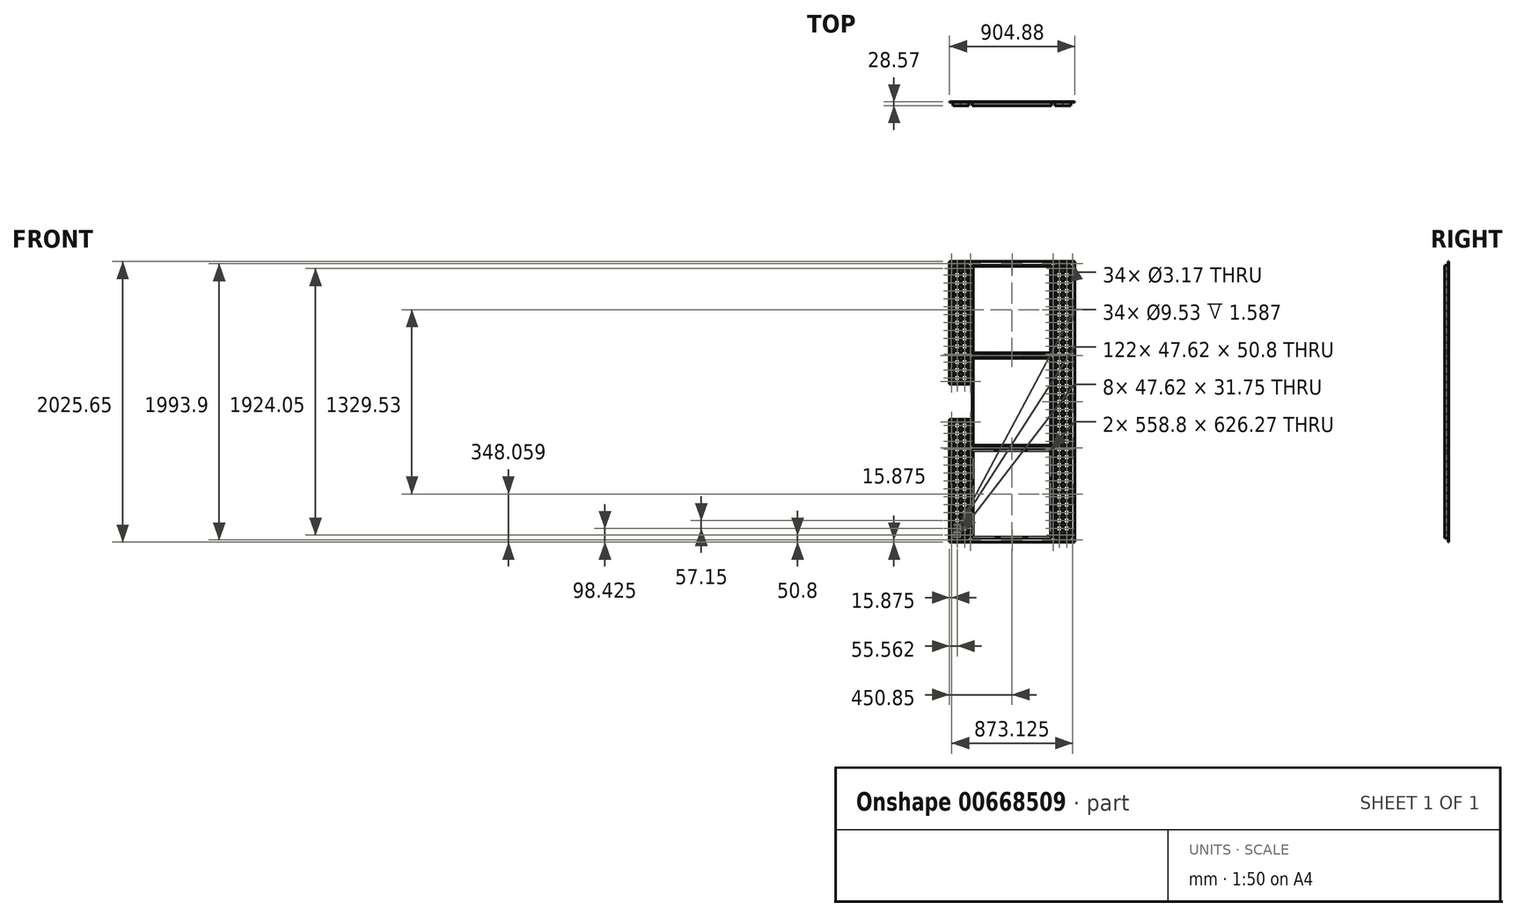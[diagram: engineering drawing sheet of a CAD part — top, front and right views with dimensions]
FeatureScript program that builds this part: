
annotation { "Feature Type Name" : "Feature", "Feature Type Description" : "" }
export const myFeature = defineFeature(function(context is Context, id is Id, definition is map)
    precondition{}
    {
        {
            var Q0;
            Q0=qCreatedBy(makeId("Front.planeOp"),FACE);
            var sketch = newSketch(context, id + "F0", { "sketchPlane" : qUnion([Q0])});
            skLineSegment(sketch, "E0.top", {"start": v(-285.75, 485.77) * mm, "end": v(285.75, 485.77) * mm});
            skPoint(sketch, "E0.middle", {"position": v(0, 0) * mm});
            skLineSegment(sketch, "E1.0", {"start": v(-285.75, -1482.73) * mm, "end": v(285.75, -1482.73) * mm});
            skLineSegment(sketch, "E2", {"start": v(311.15, 485.77) * mm, "end": v(311.15, -1482.73) * mm});
            skLineSegment(sketch, "E3", {"start": v(311.15, -1482.73) * mm, "end": v(425.45, -1482.73) * mm});
            skLineSegment(sketch, "E4", {"start": v(425.45, -1482.73) * mm, "end": v(425.45, 485.77) * mm});
            skLineSegment(sketch, "E5", {"start": v(425.45, 485.77) * mm, "end": v(311.15, 485.77) * mm});
            skLineSegment(sketch, "E6", {"start": v(-311.15, -1482.73) * mm, "end": v(-311.15, -638.18) * mm});
            skLineSegment(sketch, "E7", {"start": v(-311.15, -638.18) * mm, "end": v(-425.45, -638.18) * mm});
            skLineSegment(sketch, "E8", {"start": v(-425.45, -638.18) * mm, "end": v(-425.45, -1482.73) * mm});
            skLineSegment(sketch, "E9", {"start": v(-425.45, -1482.73) * mm, "end": v(-311.15, -1482.73) * mm});
            skLineSegment(sketch, "E10", {"start": v(-311.15, 485.77) * mm, "end": v(-425.45, 485.77) * mm});
            skLineSegment(sketch, "E11", {"start": v(-425.45, 485.77) * mm, "end": v(-425.45, -358.78) * mm});
            skLineSegment(sketch, "E12", {"start": v(-311.15, 485.77) * mm, "end": v(-311.15, -358.78) * mm});
            skLineSegment(sketch, "E13", {"start": v(-311.15, -358.78) * mm, "end": v(-425.45, -358.78) * mm});
            skLineSegment(sketch, "E14.0", {"start": v(450.85, -1508.13) * mm, "end": v(450.85, 511.17) * mm});
            skLineSegment(sketch, "E15", {"start": v(450.85, 511.17) * mm, "end": v(-450.85, 511.17) * mm});
            skLineSegment(sketch, "E16", {"start": v(-450.85, 511.17) * mm, "end": v(-450.85, -371.48) * mm});
            skLineSegment(sketch, "E17", {"start": v(-450.85, -371.48) * mm, "end": v(-298.45, -371.48) * mm});
            skLineSegment(sketch, "E18", {"start": v(-298.45, -371.48) * mm, "end": v(-298.45, -625.48) * mm});
            skLineSegment(sketch, "E19", {"start": v(-298.45, -625.48) * mm, "end": v(-450.85, -625.48) * mm});
            skLineSegment(sketch, "E20", {"start": v(-450.85, -625.48) * mm, "end": v(-450.85, -1508.13) * mm});
            skLineSegment(sketch, "E21", {"start": v(-450.85, -1508.13) * mm, "end": v(450.85, -1508.13) * mm});
            skLineSegment(sketch, "E22", {"start": v(-285.75, 485.77) * mm, "end": v(-285.75, -1482.73) * mm});
            skLineSegment(sketch, "E23", {"start": v(285.75, -1482.73) * mm, "end": v(285.75, 485.77) * mm});
            skLineSegment(sketch, "E24", {"start": v(-285.75, -818.36) * mm, "end": v(285.75, -818.36) * mm});
            skLineSegment(sketch, "E25", {"start": v(-285.75, -153.2) * mm, "end": v(285.75, -153.2) * mm});
            skLineSegment(sketch, "E26", {"start": v(-285.75, -178.6) * mm, "end": v(285.75, -178.6) * mm});
            skLineSegment(sketch, "E27", {"start": v(-285.75, -843.76) * mm, "end": v(285.75, -843.76) * mm});
            skLineSegment(sketch, "E28.2", {"start": v(-450.85, -1511.3) * mm, "end": v(454.02, -1511.3) * mm});
            skLineSegment(sketch, "E28.3", {"start": v(454.02, -1511.3) * mm, "end": v(454.02, 514.35) * mm});
            skLineSegment(sketch, "E28.4", {"start": v(454.02, 514.35) * mm, "end": v(-450.85, 514.35) * mm});
            skLineSegment(sketch, "E29", {"start": v(-450.85, 511.17) * mm, "end": v(-450.85, 514.35) * mm});
            skLineSegment(sketch, "E30", {"start": v(-450.85, -1511.3) * mm, "end": v(-450.85, -1508.13) * mm});
            skSolve(sketch);
        }
        {
            var Q0;
            Q0 = qSketchRegion(id + "F0", true);
            var Q1;
            {var subQ0=sQuery(id+"F0.wireOp",EDGE,"E24");Q1=makeQuery(id+"F0.imprint","IMPRINT",FACE,{"disambiguationData":[TD([[makeQuery(id+"F0.imprint","IMPRINT",EDGE,{"derivedFrom":subQ0}),-1.0]])]});}
            var Q2;
            {var subQ0=sQuery(id+"F0.wireOp",EDGE,"E25");Q2=makeQuery(id+"F0.imprint","IMPRINT",FACE,{"disambiguationData":[TD([[makeQuery(id+"F0.imprint","IMPRINT",EDGE,{"derivedFrom":subQ0}),-1.0]])]});}
            extrude(context, id + "F1", {"entities" : qUnion([Q0, Q1, Q2]), "depth" : 3.17 * mm, "offsetDistance" : 25.4 * mm});
        }
        {
            var Q0;
            Q0=qCreatedBy(makeId("Front.planeOp"),FACE);
            var sketch = newSketch(context, id + "F2", { "sketchPlane" : qUnion([Q0])});
            skLineSegment(sketch, "E31.0", {"start": v(-425.45, 485.77) * mm, "end": v(-425.45, -358.78) * mm});
            skLineSegment(sketch, "E32.0", {"start": v(-311.15, 485.77) * mm, "end": v(-425.45, 485.77) * mm});
            skLineSegment(sketch, "E33.0", {"start": v(-311.15, 485.77) * mm, "end": v(-311.15, -358.78) * mm});
            skLineSegment(sketch, "E34.0", {"start": v(-311.15, -358.78) * mm, "end": v(-425.45, -358.78) * mm});
            skLineSegment(sketch, "E35.0", {"start": v(-285.75, 485.77) * mm, "end": v(-285.75, 485.77) * mm});
            skPoint(sketch, "E36.0", {"position": v(368.3, 485.77) * mm});
            skLineSegment(sketch, "E37.0", {"start": v(425.45, 485.77) * mm, "end": v(311.15, 485.77) * mm});
            skLineSegment(sketch, "E38.0", {"start": v(-425.45, -1482.73) * mm, "end": v(-311.15, -1482.73) * mm});
            skLineSegment(sketch, "E39.0", {"start": v(-311.15, -1482.73) * mm, "end": v(-311.15, -638.18) * mm});
            skLineSegment(sketch, "E40.0", {"start": v(-425.45, -638.18) * mm, "end": v(-425.45, -1482.73) * mm});
            skLineSegment(sketch, "E41.0", {"start": v(-311.15, -638.18) * mm, "end": v(-425.45, -638.18) * mm});
            skLineSegment(sketch, "E42.0", {"start": v(-419.1, 479.42) * mm, "end": v(-419.1, -352.42) * mm});
            skLineSegment(sketch, "E42.1", {"start": v(-317.5, 479.42) * mm, "end": v(-419.1, 479.42) * mm});
            skLineSegment(sketch, "E42.2", {"start": v(-317.5, 479.42) * mm, "end": v(-317.5, -352.42) * mm});
            skLineSegment(sketch, "E42.3", {"start": v(-317.5, -352.42) * mm, "end": v(-419.1, -352.42) * mm});
            skLineSegment(sketch, "E43.0", {"start": v(-317.5, -644.52) * mm, "end": v(-419.1, -644.52) * mm});
            skLineSegment(sketch, "E43.1", {"start": v(-317.5, -1476.38) * mm, "end": v(-317.5, -644.52) * mm});
            skLineSegment(sketch, "E43.2", {"start": v(-419.1, -1476.38) * mm, "end": v(-317.5, -1476.38) * mm});
            skLineSegment(sketch, "E43.3", {"start": v(-419.1, -644.52) * mm, "end": v(-419.1, -1476.38) * mm});
            skLineSegment(sketch, "E44.0", {"start": v(-285.75, 485.77) * mm, "end": v(-285.75, -153.2) * mm});
            skLineSegment(sketch, "E45.0", {"start": v(-285.75, 485.77) * mm, "end": v(285.75, 485.77) * mm});
            skLineSegment(sketch, "E46.0", {"start": v(285.75, -153.2) * mm, "end": v(285.75, 485.77) * mm});
            skLineSegment(sketch, "E47.0", {"start": v(-285.75, -153.2) * mm, "end": v(285.75, -153.2) * mm});
            skLineSegment(sketch, "E48.0", {"start": v(-285.75, -178.6) * mm, "end": v(285.75, -178.6) * mm});
            skLineSegment(sketch, "E49.0", {"start": v(-285.75, -178.6) * mm, "end": v(-285.75, -818.36) * mm});
            skLineSegment(sketch, "E50.0", {"start": v(285.75, -818.36) * mm, "end": v(285.75, -178.6) * mm});
            skLineSegment(sketch, "E51.0", {"start": v(-285.75, -818.36) * mm, "end": v(285.75, -818.36) * mm});
            skLineSegment(sketch, "E52.0", {"start": v(-285.75, -843.76) * mm, "end": v(285.75, -843.76) * mm});
            skLineSegment(sketch, "E53.0", {"start": v(-285.75, -843.76) * mm, "end": v(-285.75, -1482.73) * mm});
            skLineSegment(sketch, "E54.0", {"start": v(285.75, -1482.73) * mm, "end": v(285.75, -843.76) * mm});
            skLineSegment(sketch, "E55.0", {"start": v(-285.75, -1482.73) * mm, "end": v(285.75, -1482.73) * mm});
            skLineSegment(sketch, "E56.0", {"start": v(-279.4, 479.43) * mm, "end": v(279.4, 479.43) * mm});
            skLineSegment(sketch, "E56.1", {"start": v(-279.4, 479.43) * mm, "end": v(-279.4, -146.84) * mm});
            skLineSegment(sketch, "E56.2", {"start": v(-279.4, -146.84) * mm, "end": v(279.4, -146.84) * mm});
            skLineSegment(sketch, "E56.3", {"start": v(279.4, -146.84) * mm, "end": v(279.4, 479.43) * mm});
            skLineSegment(sketch, "E57.0", {"start": v(-279.4, -184.94) * mm, "end": v(279.4, -184.94) * mm});
            skLineSegment(sketch, "E57.1", {"start": v(-279.4, -184.94) * mm, "end": v(-279.4, -812) * mm});
            skLineSegment(sketch, "E57.2", {"start": v(-279.4, -812) * mm, "end": v(279.4, -812) * mm});
            skLineSegment(sketch, "E57.3", {"start": v(279.4, -812) * mm, "end": v(279.4, -184.94) * mm});
            skLineSegment(sketch, "E58.0", {"start": v(-279.4, -850.1) * mm, "end": v(279.4, -850.1) * mm});
            skLineSegment(sketch, "E58.1", {"start": v(-279.4, -850.1) * mm, "end": v(-279.4, -1476.38) * mm});
            skLineSegment(sketch, "E58.2", {"start": v(-279.4, -1476.38) * mm, "end": v(279.4, -1476.38) * mm});
            skLineSegment(sketch, "E58.3", {"start": v(279.4, -1476.38) * mm, "end": v(279.4, -850.1) * mm});
            skLineSegment(sketch, "E59.0", {"start": v(425.45, -1482.73) * mm, "end": v(425.45, 485.77) * mm});
            skLineSegment(sketch, "E60.0", {"start": v(311.15, -1482.73) * mm, "end": v(425.45, -1482.73) * mm});
            skLineSegment(sketch, "E61.0", {"start": v(311.15, 485.77) * mm, "end": v(311.15, -1482.73) * mm});
            skLineSegment(sketch, "E62.0", {"start": v(419.1, 479.43) * mm, "end": v(317.5, 479.43) * mm});
            skLineSegment(sketch, "E62.1", {"start": v(419.1, -1476.38) * mm, "end": v(419.1, 479.43) * mm});
            skLineSegment(sketch, "E62.2", {"start": v(317.5, -1476.38) * mm, "end": v(419.1, -1476.38) * mm});
            skLineSegment(sketch, "E62.3", {"start": v(317.5, 479.43) * mm, "end": v(317.5, -1476.38) * mm});
            skSolve(sketch);
        }
        {
            var Q0;
            Q0=makeQuery(id+"F2.imprint","IMPRINT",FACE,{"disambiguationData":[TD([[makeQuery(id+"F2.imprint","IMPRINT",EDGE,{"derivedFrom":sQuery(id+"F2.wireOp",EDGE,"E37.0")}),1.0]])]});
            var Q1;
            Q1=makeQuery(id+"F2.imprint","IMPRINT",FACE,{"disambiguationData":[TD([[makeQuery(id+"F2.imprint","IMPRINT",EDGE,{"derivedFrom":sQuery(id+"F2.wireOp",EDGE,"E52.0")}),-1.0]])]});
            var Q2;
            Q2=makeQuery(id+"F2.imprint","IMPRINT",FACE,{"disambiguationData":[TD([[makeQuery(id+"F2.imprint","IMPRINT",EDGE,{"derivedFrom":sQuery(id+"F2.wireOp",EDGE,"E48.0")}),-1.0]])]});
            var Q3;
            Q3=makeQuery(id+"F2.imprint","IMPRINT",FACE,{"disambiguationData":[TD([[makeQuery(id+"F2.imprint","IMPRINT",EDGE,{"derivedFrom":sQuery(id+"F2.wireOp",EDGE,"E38.0")}),1.0]])]});
            var Q4;
            Q4=makeQuery(id+"F2.imprint","IMPRINT",FACE,{"disambiguationData":[TD([[makeQuery(id+"F2.imprint","IMPRINT",EDGE,{"derivedFrom":sQuery(id+"F2.wireOp",EDGE,"E31.0")}),1.0]])]});
            var Q5;
            Q5=makeQuery(id+"F2.imprint","IMPRINT",FACE,{"disambiguationData":[TD([[makeQuery(id+"F2.imprint","IMPRINT",EDGE,{"derivedFrom":sQuery(id+"F2.wireOp",EDGE,"E44.0")}),1.0]])]});
            extrude(context, id + "F3", {"entities" : qUnion([Q0, Q1, Q2, Q3, Q4, Q5]), "operationType" : NewBodyOperationType.ADD, "depth" : 28.57 * mm, "offsetDistance" : 25.4 * mm});
        }
        {
            var Q0;
            Q0=qCreatedBy(makeId("Front.planeOp"),FACE);
            var sketch = newSketch(context, id + "F4", { "sketchPlane" : qUnion([Q0])});
            skLineSegment(sketch, "E63.0", {"start": v(-279.4, -184.94) * mm, "end": v(-279.4, -812) * mm});
            skLineSegment(sketch, "E64.0", {"start": v(279.4, -812) * mm, "end": v(279.4, -184.94) * mm});
            skLineSegment(sketch, "E65.0", {"start": v(-279.4, -812) * mm, "end": v(279.4, -812) * mm});
            skLineSegment(sketch, "E66.0", {"start": v(-317.5, 479.42) * mm, "end": v(-419.1, 479.42) * mm});
            skLineSegment(sketch, "E67.0", {"start": v(-419.1, 479.42) * mm, "end": v(-419.1, -352.42) * mm});
            skLineSegment(sketch, "E68.0", {"start": v(-317.5, 479.42) * mm, "end": v(-317.5, -352.42) * mm});
            skLineSegment(sketch, "E69.0", {"start": v(-317.5, -352.42) * mm, "end": v(-419.1, -352.42) * mm});
            skLineSegment(sketch, "E70.0", {"start": v(-419.1, -644.52) * mm, "end": v(-419.1, -1476.38) * mm});
            skLineSegment(sketch, "E71.0", {"start": v(-317.5, -644.52) * mm, "end": v(-419.1, -644.52) * mm});
            skLineSegment(sketch, "E72.0", {"start": v(-317.5, -1476.38) * mm, "end": v(-317.5, -644.52) * mm});
            skLineSegment(sketch, "E73.0", {"start": v(-419.1, -1476.38) * mm, "end": v(-317.5, -1476.38) * mm});
            skLineSegment(sketch, "E74.0", {"start": v(317.5, -1476.38) * mm, "end": v(419.1, -1476.38) * mm});
            skLineSegment(sketch, "E75.0", {"start": v(317.5, 479.43) * mm, "end": v(317.5, -1476.38) * mm});
            skLineSegment(sketch, "E76.0", {"start": v(419.1, -1476.38) * mm, "end": v(419.1, 479.43) * mm});
            skLineSegment(sketch, "E77.0", {"start": v(419.1, 479.43) * mm, "end": v(317.5, 479.43) * mm});
            skLineSegment(sketch, "E78", {"start": v(-419.1, -1444.63) * mm, "end": v(-317.5, -1444.63) * mm});
            skLineSegment(sketch, "E79.0", {"start": v(-419.1, -1438.27) * mm, "end": v(-317.5, -1438.27) * mm});
            skLineSegment(sketch, "E80.0", {"start": v(-419.1, -1387.47) * mm, "end": v(-317.5, -1387.47) * mm});
            skLineSegment(sketch, "E81.0", {"start": v(-419.1, -1381.12) * mm, "end": v(-317.5, -1381.12) * mm});
            skLineSegment(sketch, "E82.0", {"start": v(-419.1, -1330.32) * mm, "end": v(-371.47, -1330.32) * mm});
            skLineSegment(sketch, "E83.0", {"start": v(-419.1, -1323.97) * mm, "end": v(-317.5, -1323.97) * mm});
            skLineSegment(sketch, "E84.0", {"start": v(-419.1, -1273.17) * mm, "end": v(-317.5, -1273.17) * mm});
            skLineSegment(sketch, "E85.0", {"start": v(-419.1, -1266.82) * mm, "end": v(-317.5, -1266.82) * mm});
            skLineSegment(sketch, "E86.0", {"start": v(-419.1, -1216.02) * mm, "end": v(-317.5, -1216.02) * mm});
            skLineSegment(sketch, "E87.0", {"start": v(-419.1, -1209.67) * mm, "end": v(-317.5, -1209.67) * mm});
            skLineSegment(sketch, "E88.0", {"start": v(-419.1, -1158.87) * mm, "end": v(-317.5, -1158.87) * mm});
            skLineSegment(sketch, "E89.0", {"start": v(-419.1, -1152.52) * mm, "end": v(-317.5, -1152.52) * mm});
            skLineSegment(sketch, "E90.0", {"start": v(-419.1, -1101.72) * mm, "end": v(-317.5, -1101.72) * mm});
            skLineSegment(sketch, "E91.0", {"start": v(-419.1, -1095.37) * mm, "end": v(-317.5, -1095.37) * mm});
            skLineSegment(sketch, "E92.0", {"start": v(-419.1, -1044.57) * mm, "end": v(-317.5, -1044.57) * mm});
            skLineSegment(sketch, "E93.0", {"start": v(-419.1, -1038.22) * mm, "end": v(-317.5, -1038.22) * mm});
            skLineSegment(sketch, "E94.0", {"start": v(-419.1, -987.42) * mm, "end": v(-317.5, -987.42) * mm});
            skLineSegment(sketch, "E95.0", {"start": v(-419.1, -981.07) * mm, "end": v(-317.5, -981.07) * mm});
            skLineSegment(sketch, "E96.0", {"start": v(-419.1, -930.27) * mm, "end": v(-317.5, -930.27) * mm});
            skLineSegment(sketch, "E97.0", {"start": v(-419.1, -923.92) * mm, "end": v(-317.5, -923.92) * mm});
            skLineSegment(sketch, "E98.0", {"start": v(-419.1, -873.12) * mm, "end": v(-317.5, -873.12) * mm});
            skLineSegment(sketch, "E99.0", {"start": v(-419.1, -866.77) * mm, "end": v(-317.5, -866.77) * mm});
            skLineSegment(sketch, "E100.0", {"start": v(-419.1, -815.97) * mm, "end": v(-317.5, -815.97) * mm});
            skLineSegment(sketch, "E101.0", {"start": v(-419.1, -809.62) * mm, "end": v(-279.4, -809.62) * mm});
            skLineSegment(sketch, "E102.0", {"start": v(-419.1, -758.82) * mm, "end": v(-279.4, -758.82) * mm});
            skLineSegment(sketch, "E103.0", {"start": v(-419.1, -752.47) * mm, "end": v(-279.4, -752.47) * mm});
            skLineSegment(sketch, "E104.0", {"start": v(-419.1, -701.67) * mm, "end": v(-317.5, -701.67) * mm});
            skLineSegment(sketch, "E105.0", {"start": v(-419.1, -695.32) * mm, "end": v(-317.5, -695.32) * mm});
            skLineSegment(sketch, "E106.0", {"start": v(-419.1, -644.52) * mm, "end": v(-279.4, -644.52) * mm});
            skLineSegment(sketch, "E107.0", {"start": v(-419.1, -638.17) * mm, "end": v(-279.4, -638.17) * mm});
            skLineSegment(sketch, "E108.0", {"start": v(-419.1, -587.37) * mm, "end": v(-279.4, -587.37) * mm});
            skLineSegment(sketch, "E109.0", {"start": v(-419.1, -581.02) * mm, "end": v(-279.4, -581.02) * mm});
            skLineSegment(sketch, "E110.0", {"start": v(-419.1, -530.22) * mm, "end": v(-279.4, -530.22) * mm});
            skLineSegment(sketch, "E111.0", {"start": v(-419.1, -523.87) * mm, "end": v(-279.4, -523.87) * mm});
            skLineSegment(sketch, "E112.0", {"start": v(-419.1, -473.07) * mm, "end": v(-279.4, -473.07) * mm});
            skLineSegment(sketch, "E113.0", {"start": v(-419.1, -466.72) * mm, "end": v(-279.4, -466.72) * mm});
            skLineSegment(sketch, "E114.0", {"start": v(-419.1, -415.92) * mm, "end": v(-279.4, -415.92) * mm});
            skLineSegment(sketch, "E115.0", {"start": v(-419.1, -409.57) * mm, "end": v(-279.4, -409.57) * mm});
            skLineSegment(sketch, "E116.0", {"start": v(-419.1, -358.77) * mm, "end": v(-279.4, -358.77) * mm});
            skLineSegment(sketch, "E117.0", {"start": v(-419.1, -352.42) * mm, "end": v(-279.4, -352.42) * mm});
            skLineSegment(sketch, "E118.0", {"start": v(-419.1, -301.62) * mm, "end": v(-279.4, -301.62) * mm});
            skLineSegment(sketch, "E119.trimOffspring", {"start": v(279.4, -695.32) * mm, "end": v(419.1, -695.32) * mm});
            skLineSegment(sketch, "E120.trimOffspring", {"start": v(279.4, -701.67) * mm, "end": v(419.1, -701.67) * mm});
            skLineSegment(sketch, "E121.0", {"start": v(-419.1, -295.27) * mm, "end": v(-279.4, -295.27) * mm});
            skLineSegment(sketch, "E122.0", {"start": v(-419.1, -244.47) * mm, "end": v(-279.4, -244.47) * mm});
            skLineSegment(sketch, "E123.0", {"start": v(-419.1, -238.12) * mm, "end": v(-279.4, -238.12) * mm});
            skLineSegment(sketch, "E124.0", {"start": v(-419.1, -187.32) * mm, "end": v(279.4, -187.32) * mm});
            skLineSegment(sketch, "E125.0", {"start": v(-419.1, -180.97) * mm, "end": v(-317.5, -180.97) * mm});
            skLineSegment(sketch, "E126.0", {"start": v(-419.1, -130.17) * mm, "end": v(-317.5, -130.17) * mm});
            skLineSegment(sketch, "E127.0", {"start": v(-419.1, -123.82) * mm, "end": v(-317.5, -123.82) * mm});
            skLineSegment(sketch, "E128.0", {"start": v(-419.1, -73.02) * mm, "end": v(-317.5, -73.02) * mm});
            skLineSegment(sketch, "E129.0", {"start": v(-419.1, -66.67) * mm, "end": v(-317.5, -66.67) * mm});
            skLineSegment(sketch, "E130.0", {"start": v(-419.1, -15.87) * mm, "end": v(-317.5, -15.87) * mm});
            skLineSegment(sketch, "E131.0", {"start": v(-419.1, -9.52) * mm, "end": v(-317.5, -9.52) * mm});
            skLineSegment(sketch, "E132.0", {"start": v(-419.1, 41.28) * mm, "end": v(-317.5, 41.28) * mm});
            skLineSegment(sketch, "E133.0", {"start": v(-419.1, 47.63) * mm, "end": v(-317.5, 47.63) * mm});
            skLineSegment(sketch, "E134.0", {"start": v(-419.1, 98.43) * mm, "end": v(-317.5, 98.43) * mm});
            skLineSegment(sketch, "E135.0", {"start": v(-419.1, 104.78) * mm, "end": v(-317.5, 104.78) * mm});
            skLineSegment(sketch, "E136.0", {"start": v(-419.1, 155.58) * mm, "end": v(-317.5, 155.58) * mm});
            skLineSegment(sketch, "E137.0", {"start": v(-419.1, 161.93) * mm, "end": v(-317.5, 161.93) * mm});
            skLineSegment(sketch, "E138.0", {"start": v(-419.1, 212.73) * mm, "end": v(-317.5, 212.73) * mm});
            skLineSegment(sketch, "E139.0", {"start": v(-419.1, 219.08) * mm, "end": v(-317.5, 219.08) * mm});
            skLineSegment(sketch, "E140.0", {"start": v(-419.1, 269.88) * mm, "end": v(-317.5, 269.88) * mm});
            skLineSegment(sketch, "E141.0", {"start": v(-419.1, 276.23) * mm, "end": v(-317.5, 276.23) * mm});
            skLineSegment(sketch, "E142.0", {"start": v(-419.1, 327.03) * mm, "end": v(-317.5, 327.03) * mm});
            skLineSegment(sketch, "E143.0", {"start": v(-419.1, 333.38) * mm, "end": v(-317.5, 333.38) * mm});
            skLineSegment(sketch, "E144.0", {"start": v(-419.1, 384.18) * mm, "end": v(-317.5, 384.18) * mm});
            skLineSegment(sketch, "E145.0", {"start": v(-419.1, 390.53) * mm, "end": v(-317.5, 390.53) * mm});
            skLineSegment(sketch, "E146.0", {"start": v(-419.1, 441.33) * mm, "end": v(-317.5, 441.33) * mm});
            skLineSegment(sketch, "E147.0", {"start": v(-419.1, 447.68) * mm, "end": v(-317.5, 447.68) * mm});
            skLineSegment(sketch, "E148.trimOffspring", {"start": v(317.5, -1444.63) * mm, "end": v(419.1, -1444.63) * mm});
            skLineSegment(sketch, "E149.trimOffspring", {"start": v(317.5, -1438.27) * mm, "end": v(419.1, -1438.27) * mm});
            skLineSegment(sketch, "E150.trimOffspring", {"start": v(317.5, -1387.47) * mm, "end": v(419.1, -1387.47) * mm});
            skLineSegment(sketch, "E151.trimOffspring", {"start": v(317.5, -1381.12) * mm, "end": v(419.1, -1381.12) * mm});
            skLineSegment(sketch, "E152.trimOffspring", {"start": v(317.5, -1330.32) * mm, "end": v(419.1, -1330.32) * mm});
            skLineSegment(sketch, "E153.trimOffspring", {"start": v(317.5, -1323.97) * mm, "end": v(419.1, -1323.97) * mm});
            skLineSegment(sketch, "E154.trimOffspring", {"start": v(317.5, -1273.17) * mm, "end": v(419.1, -1273.17) * mm});
            skLineSegment(sketch, "E155.trimOffspring", {"start": v(317.5, -1266.82) * mm, "end": v(419.1, -1266.82) * mm});
            skLineSegment(sketch, "E156.trimOffspring", {"start": v(317.5, -1216.02) * mm, "end": v(419.1, -1216.02) * mm});
            skLineSegment(sketch, "E157.trimOffspring", {"start": v(317.5, -1209.67) * mm, "end": v(419.1, -1209.67) * mm});
            skLineSegment(sketch, "E158.trimOffspring", {"start": v(317.5, -1152.52) * mm, "end": v(419.1, -1152.52) * mm});
            skLineSegment(sketch, "E159.trimOffspring", {"start": v(317.5, -1158.87) * mm, "end": v(419.1, -1158.87) * mm});
            skLineSegment(sketch, "E160.trimOffspring", {"start": v(317.5, -1095.37) * mm, "end": v(419.1, -1095.37) * mm});
            skLineSegment(sketch, "E161.trimOffspring", {"start": v(317.5, -1101.72) * mm, "end": v(419.1, -1101.72) * mm});
            skLineSegment(sketch, "E162.trimOffspring", {"start": v(317.5, -1044.57) * mm, "end": v(419.1, -1044.57) * mm});
            skLineSegment(sketch, "E163.trimOffspring", {"start": v(317.5, -1038.22) * mm, "end": v(419.1, -1038.22) * mm});
            skLineSegment(sketch, "E164.trimOffspring", {"start": v(317.5, -987.42) * mm, "end": v(419.1, -987.42) * mm});
            skLineSegment(sketch, "E165.trimOffspring", {"start": v(317.5, -981.07) * mm, "end": v(419.1, -981.07) * mm});
            skLineSegment(sketch, "E166.trimOffspring", {"start": v(317.5, -930.27) * mm, "end": v(419.1, -930.27) * mm});
            skLineSegment(sketch, "E167.trimOffspring", {"start": v(317.5, -923.92) * mm, "end": v(419.1, -923.92) * mm});
            skLineSegment(sketch, "E168.trimOffspring", {"start": v(317.5, -873.12) * mm, "end": v(419.1, -873.12) * mm});
            skLineSegment(sketch, "E169.trimOffspring", {"start": v(317.5, -866.77) * mm, "end": v(419.1, -866.77) * mm});
            skLineSegment(sketch, "E170.trimOffspring", {"start": v(317.5, -815.97) * mm, "end": v(419.1, -815.97) * mm});
            skLineSegment(sketch, "E171.trimOffspring", {"start": v(279.4, -809.62) * mm, "end": v(419.1, -809.62) * mm});
            skLineSegment(sketch, "E172.trimOffspring", {"start": v(279.4, -758.82) * mm, "end": v(419.1, -758.82) * mm});
            skLineSegment(sketch, "E173.trimOffspring", {"start": v(279.4, -752.47) * mm, "end": v(419.1, -752.47) * mm});
            skLineSegment(sketch, "E174.trimOffspring", {"start": v(279.4, -644.52) * mm, "end": v(419.1, -644.52) * mm});
            skLineSegment(sketch, "E175.trimOffspring", {"start": v(279.4, -638.17) * mm, "end": v(419.1, -638.17) * mm});
            skLineSegment(sketch, "E176.trimOffspring", {"start": v(279.4, -587.37) * mm, "end": v(419.1, -587.37) * mm});
            skLineSegment(sketch, "E177.trimOffspring", {"start": v(279.4, -581.02) * mm, "end": v(419.1, -581.02) * mm});
            skLineSegment(sketch, "E178.trimOffspring", {"start": v(279.4, -530.22) * mm, "end": v(419.1, -530.22) * mm});
            skLineSegment(sketch, "E179.trimOffspring", {"start": v(279.4, -523.87) * mm, "end": v(419.1, -523.87) * mm});
            skLineSegment(sketch, "E180.trimOffspring", {"start": v(279.4, -473.07) * mm, "end": v(419.1, -473.07) * mm});
            skLineSegment(sketch, "E181.trimOffspring", {"start": v(279.4, -466.72) * mm, "end": v(419.1, -466.72) * mm});
            skLineSegment(sketch, "E182.trimOffspring", {"start": v(279.4, -415.92) * mm, "end": v(419.1, -415.92) * mm});
            skLineSegment(sketch, "E183.trimOffspring", {"start": v(279.4, -409.57) * mm, "end": v(419.1, -409.57) * mm});
            skLineSegment(sketch, "E184.trimOffspring", {"start": v(279.4, -358.77) * mm, "end": v(419.1, -358.77) * mm});
            skLineSegment(sketch, "E185.trimOffspring", {"start": v(279.4, -352.42) * mm, "end": v(419.1, -352.42) * mm});
            skLineSegment(sketch, "E186.trimOffspring", {"start": v(279.4, -301.62) * mm, "end": v(419.1, -301.62) * mm});
            skLineSegment(sketch, "E187.trimOffspring", {"start": v(279.4, -295.27) * mm, "end": v(419.1, -295.27) * mm});
            skLineSegment(sketch, "E188.trimOffspring", {"start": v(279.4, -244.47) * mm, "end": v(419.1, -244.47) * mm});
            skLineSegment(sketch, "E189.trimOffspring", {"start": v(279.4, -238.12) * mm, "end": v(419.1, -238.12) * mm});
            skLineSegment(sketch, "E190.trimOffspring", {"start": v(317.5, -180.97) * mm, "end": v(419.1, -180.97) * mm});
            skLineSegment(sketch, "E191.trimOffspring", {"start": v(317.5, -187.32) * mm, "end": v(419.1, -187.32) * mm});
            skLineSegment(sketch, "E192.trimOffspring", {"start": v(317.5, -130.17) * mm, "end": v(419.1, -130.17) * mm});
            skLineSegment(sketch, "E193.trimOffspring", {"start": v(317.5, -123.82) * mm, "end": v(419.1, -123.82) * mm});
            skLineSegment(sketch, "E194.trimOffspring", {"start": v(317.5, -73.02) * mm, "end": v(419.1, -73.02) * mm});
            skLineSegment(sketch, "E195.trimOffspring", {"start": v(317.5, -66.67) * mm, "end": v(419.1, -66.67) * mm});
            skLineSegment(sketch, "E196.trimOffspring", {"start": v(317.5, -9.52) * mm, "end": v(419.1, -9.52) * mm});
            skLineSegment(sketch, "E197.trimOffspring", {"start": v(317.5, -15.87) * mm, "end": v(419.1, -15.87) * mm});
            skLineSegment(sketch, "E198.trimOffspring", {"start": v(317.5, 47.63) * mm, "end": v(419.1, 47.63) * mm});
            skLineSegment(sketch, "E199.trimOffspring", {"start": v(317.5, 41.28) * mm, "end": v(419.1, 41.28) * mm});
            skLineSegment(sketch, "E200.trimOffspring", {"start": v(317.5, 104.78) * mm, "end": v(419.1, 104.78) * mm});
            skLineSegment(sketch, "E201.trimOffspring", {"start": v(317.5, 98.43) * mm, "end": v(419.1, 98.43) * mm});
            skLineSegment(sketch, "E202.trimOffspring", {"start": v(317.5, 155.58) * mm, "end": v(419.1, 155.58) * mm});
            skLineSegment(sketch, "E203.trimOffspring", {"start": v(317.5, 161.93) * mm, "end": v(419.1, 161.93) * mm});
            skLineSegment(sketch, "E204.trimOffspring", {"start": v(317.5, 212.73) * mm, "end": v(419.1, 212.73) * mm});
            skLineSegment(sketch, "E205.trimOffspring", {"start": v(317.5, 219.08) * mm, "end": v(419.1, 219.08) * mm});
            skLineSegment(sketch, "E206.trimOffspring", {"start": v(317.5, 276.23) * mm, "end": v(419.1, 276.23) * mm});
            skLineSegment(sketch, "E207.trimOffspring", {"start": v(317.5, 269.88) * mm, "end": v(419.1, 269.88) * mm});
            skLineSegment(sketch, "E208.trimOffspring", {"start": v(317.5, 327.03) * mm, "end": v(419.1, 327.03) * mm});
            skLineSegment(sketch, "E209.trimOffspring", {"start": v(317.5, 333.38) * mm, "end": v(419.1, 333.38) * mm});
            skLineSegment(sketch, "E210.trimOffspring", {"start": v(317.5, 384.18) * mm, "end": v(419.1, 384.18) * mm});
            skLineSegment(sketch, "E211.trimOffspring", {"start": v(317.5, 390.53) * mm, "end": v(419.1, 390.53) * mm});
            skLineSegment(sketch, "E212.trimOffspring", {"start": v(317.5, 447.68) * mm, "end": v(419.1, 447.68) * mm});
            skLineSegment(sketch, "E213.trimOffspring", {"start": v(317.5, 441.33) * mm, "end": v(419.1, 441.33) * mm});
            skLineSegment(sketch, "E214", {"start": v(-368.3, -1476.38) * mm, "end": v(-368.3, -1209.67) * mm, "construction": true});
            skLineSegment(sketch, "E215.0", {"start": v(-365.12, -1476.38) * mm, "end": v(-365.12, -1438.27) * mm});
            skLineSegment(sketch, "E216.0", {"start": v(-371.47, -1476.38) * mm, "end": v(-371.47, -1438.27) * mm});
            skLineSegment(sketch, "E217.trimOffspring", {"start": v(-365.13, -695.32) * mm, "end": v(-365.13, -638.17) * mm});
            skLineSegment(sketch, "E218.trimOffspring", {"start": v(-371.47, -1381.12) * mm, "end": v(-371.47, -1330.32) * mm});
            skLineSegment(sketch, "E219.trimOffspring", {"start": v(-365.12, -1381.12) * mm, "end": v(-365.12, -1330.32) * mm});
            skLineSegment(sketch, "E220.trimOffspring", {"start": v(-371.48, -1273.17) * mm, "end": v(-371.48, -1209.67) * mm});
            skLineSegment(sketch, "E221.trimOffspring", {"start": v(-365.13, -1273.17) * mm, "end": v(-365.13, -1209.67) * mm});
            skLineSegment(sketch, "E222.trimOffspring", {"start": v(-365.12, -1330.32) * mm, "end": v(-317.5, -1330.32) * mm});
            skLineSegment(sketch, "E223", {"start": v(-371.47, -1330.32) * mm, "end": v(-365.12, -1330.32) * mm});
            skLineSegment(sketch, "E224.trimOffspring", {"start": v(-371.48, -1158.87) * mm, "end": v(-371.48, -1095.37) * mm});
            skLineSegment(sketch, "E225.trimOffspring", {"start": v(-368.3, -1158.87) * mm, "end": v(-368.3, 479.42) * mm, "construction": true});
            skLineSegment(sketch, "E226.trimOffspring", {"start": v(-365.13, -1158.87) * mm, "end": v(-365.13, -1095.37) * mm});
            skLineSegment(sketch, "E227.trimOffspring", {"start": v(-371.48, -1044.57) * mm, "end": v(-371.48, -981.07) * mm});
            skLineSegment(sketch, "E228.trimOffspring", {"start": v(-365.13, -1044.57) * mm, "end": v(-365.13, -981.07) * mm});
            skLineSegment(sketch, "E229.trimOffspring", {"start": v(-371.48, -930.27) * mm, "end": v(-371.48, -866.77) * mm});
            skLineSegment(sketch, "E230.trimOffspring", {"start": v(-365.13, -930.27) * mm, "end": v(-365.13, -866.77) * mm});
            skLineSegment(sketch, "E231.trimOffspring", {"start": v(-371.48, -815.97) * mm, "end": v(-371.48, -752.47) * mm});
            skLineSegment(sketch, "E232.trimOffspring", {"start": v(-365.13, -815.97) * mm, "end": v(-365.13, -752.47) * mm});
            skLineSegment(sketch, "E233.trimOffspring", {"start": v(-371.48, -695.32) * mm, "end": v(-371.48, -638.17) * mm});
            skLineSegment(sketch, "E234.trimOffspring", {"start": v(-365.13, -587.37) * mm, "end": v(-365.13, -409.57) * mm});
            skLineSegment(sketch, "E235.trimOffspring", {"start": v(-371.48, -587.37) * mm, "end": v(-371.48, -409.57) * mm});
            skLineSegment(sketch, "E236.trimOffspring", {"start": v(-365.13, -358.77) * mm, "end": v(-365.13, -295.27) * mm});
            skLineSegment(sketch, "E237.trimOffspring", {"start": v(-371.48, -358.77) * mm, "end": v(-371.48, -295.27) * mm});
            skLineSegment(sketch, "E238.trimOffspring", {"start": v(-371.48, -244.47) * mm, "end": v(-371.48, -180.97) * mm});
            skLineSegment(sketch, "E239.trimOffspring", {"start": v(-365.13, -244.47) * mm, "end": v(-365.13, -180.97) * mm});
            skLineSegment(sketch, "E240.trimOffspring", {"start": v(-371.48, -130.17) * mm, "end": v(-371.48, -66.67) * mm});
            skLineSegment(sketch, "E241.trimOffspring", {"start": v(-365.13, -130.17) * mm, "end": v(-365.13, -66.67) * mm});
            skLineSegment(sketch, "E242.trimOffspring", {"start": v(-371.48, -15.87) * mm, "end": v(-371.48, 47.63) * mm});
            skLineSegment(sketch, "E243.trimOffspring", {"start": v(-365.13, -15.87) * mm, "end": v(-365.13, 47.63) * mm});
            skLineSegment(sketch, "E244.trimOffspring", {"start": v(-371.48, 98.43) * mm, "end": v(-371.48, 161.93) * mm});
            skLineSegment(sketch, "E245.trimOffspring", {"start": v(-365.13, 98.43) * mm, "end": v(-365.13, 161.93) * mm});
            skLineSegment(sketch, "E246.trimOffspring", {"start": v(-371.48, 212.73) * mm, "end": v(-371.48, 276.23) * mm});
            skLineSegment(sketch, "E247.trimOffspring", {"start": v(-365.13, 212.73) * mm, "end": v(-365.13, 276.23) * mm});
            skLineSegment(sketch, "E248.trimOffspring", {"start": v(-371.48, 327.03) * mm, "end": v(-371.48, 390.53) * mm});
            skLineSegment(sketch, "E249.trimOffspring", {"start": v(-365.13, 327.03) * mm, "end": v(-365.13, 390.53) * mm});
            skLineSegment(sketch, "E250.trimOffspring", {"start": v(-371.48, 441.33) * mm, "end": v(-371.48, 479.42) * mm});
            skLineSegment(sketch, "E251.trimOffspring", {"start": v(-365.13, 441.33) * mm, "end": v(-365.13, 479.42) * mm});
            skLineSegment(sketch, "E252", {"start": v(368.3, -1476.38) * mm, "end": v(368.3, 479.43) * mm, "construction": true});
            skLineSegment(sketch, "E253.0", {"start": v(371.48, -1476.38) * mm, "end": v(371.48, -1438.27) * mm});
            skLineSegment(sketch, "E254.0", {"start": v(365.13, -1476.38) * mm, "end": v(365.13, -1438.27) * mm});
            skLineSegment(sketch, "E255.trimOffspring", {"start": v(371.48, -1387.47) * mm, "end": v(371.48, -1323.97) * mm});
            skLineSegment(sketch, "E256.trimOffspring", {"start": v(365.13, -1387.47) * mm, "end": v(365.13, -1323.97) * mm});
            skLineSegment(sketch, "E257.trimOffspring", {"start": v(371.48, -1273.17) * mm, "end": v(371.48, -1209.67) * mm});
            skLineSegment(sketch, "E258.trimOffspring", {"start": v(365.13, -1273.17) * mm, "end": v(365.13, -1209.67) * mm});
            skLineSegment(sketch, "E259.trimOffspring", {"start": v(365.13, -1158.87) * mm, "end": v(365.13, -1095.37) * mm});
            skLineSegment(sketch, "E260.trimOffspring", {"start": v(371.48, -1158.87) * mm, "end": v(371.48, -1095.37) * mm});
            skLineSegment(sketch, "E261.trimOffspring", {"start": v(371.48, -1044.57) * mm, "end": v(371.48, -981.07) * mm});
            skLineSegment(sketch, "E262.trimOffspring", {"start": v(365.13, -1044.57) * mm, "end": v(365.13, -981.07) * mm});
            skLineSegment(sketch, "E263.trimOffspring", {"start": v(365.13, -930.27) * mm, "end": v(365.13, -866.77) * mm});
            skLineSegment(sketch, "E264.trimOffspring", {"start": v(371.48, -930.27) * mm, "end": v(371.48, -866.77) * mm});
            skLineSegment(sketch, "E265.trimOffspring", {"start": v(365.13, -815.97) * mm, "end": v(365.13, -752.47) * mm});
            skLineSegment(sketch, "E266.trimOffspring", {"start": v(371.48, -815.97) * mm, "end": v(371.48, -752.47) * mm});
            skLineSegment(sketch, "E267.trimOffspring", {"start": v(365.13, -701.67) * mm, "end": v(365.13, -638.17) * mm});
            skLineSegment(sketch, "E268.trimOffspring", {"start": v(371.48, -701.67) * mm, "end": v(371.48, -638.17) * mm});
            skLineSegment(sketch, "E269.trimOffspring", {"start": v(371.48, -587.37) * mm, "end": v(371.48, -523.87) * mm});
            skLineSegment(sketch, "E270.trimOffspring", {"start": v(365.13, -587.37) * mm, "end": v(365.13, -523.87) * mm});
            skLineSegment(sketch, "E271.trimOffspring", {"start": v(365.13, -473.07) * mm, "end": v(365.13, -409.57) * mm});
            skLineSegment(sketch, "E272.trimOffspring", {"start": v(371.48, -473.07) * mm, "end": v(371.48, -409.57) * mm});
            skLineSegment(sketch, "E273.trimOffspring", {"start": v(365.13, -358.77) * mm, "end": v(365.13, -295.27) * mm});
            skLineSegment(sketch, "E274.trimOffspring", {"start": v(371.48, -358.77) * mm, "end": v(371.48, -295.27) * mm});
            skLineSegment(sketch, "E275.trimOffspring", {"start": v(365.13, -244.47) * mm, "end": v(365.13, -180.97) * mm});
            skLineSegment(sketch, "E276.trimOffspring", {"start": v(371.48, -244.47) * mm, "end": v(371.48, -180.97) * mm});
            skLineSegment(sketch, "E277.trimOffspring", {"start": v(365.13, -130.17) * mm, "end": v(365.13, -66.67) * mm});
            skLineSegment(sketch, "E278.trimOffspring", {"start": v(371.48, -130.17) * mm, "end": v(371.48, -66.67) * mm});
            skLineSegment(sketch, "E279.trimOffspring", {"start": v(365.13, -15.87) * mm, "end": v(365.13, 47.63) * mm});
            skLineSegment(sketch, "E280.trimOffspring", {"start": v(371.48, -15.87) * mm, "end": v(371.48, 47.63) * mm});
            skLineSegment(sketch, "E281.trimOffspring", {"start": v(365.13, 98.43) * mm, "end": v(365.13, 161.93) * mm});
            skLineSegment(sketch, "E282.trimOffspring", {"start": v(371.48, 98.43) * mm, "end": v(371.48, 161.93) * mm});
            skLineSegment(sketch, "E283.trimOffspring", {"start": v(365.13, 212.73) * mm, "end": v(365.13, 276.23) * mm});
            skLineSegment(sketch, "E284.trimOffspring", {"start": v(371.48, 212.73) * mm, "end": v(371.48, 276.23) * mm});
            skLineSegment(sketch, "E285.trimOffspring", {"start": v(365.13, 327.03) * mm, "end": v(365.13, 390.53) * mm});
            skLineSegment(sketch, "E286.trimOffspring", {"start": v(371.48, 327.03) * mm, "end": v(371.48, 390.53) * mm});
            skLineSegment(sketch, "E287.trimOffspring", {"start": v(365.13, 441.33) * mm, "end": v(365.13, 479.43) * mm});
            skLineSegment(sketch, "E288.trimOffspring", {"start": v(371.48, 441.33) * mm, "end": v(371.48, 479.43) * mm});
            skLineSegment(sketch, "E289", {"start": v(-371.47, -1438.27) * mm, "end": v(-371.48, -1387.47) * mm});
            skLineSegment(sketch, "E290", {"start": v(-365.12, -1438.27) * mm, "end": v(-365.12, -1387.47) * mm});
            skLineSegment(sketch, "E291", {"start": v(-371.48, -1323.97) * mm, "end": v(-371.48, -1273.17) * mm});
            skLineSegment(sketch, "E292", {"start": v(-365.13, -1273.17) * mm, "end": v(-365.13, -1323.97) * mm});
            skLineSegment(sketch, "E293", {"start": v(-371.48, -1209.67) * mm, "end": v(-371.48, -1158.87) * mm});
            skLineSegment(sketch, "E294", {"start": v(-365.13, -1158.87) * mm, "end": v(-365.13, -1209.67) * mm});
            skLineSegment(sketch, "E295", {"start": v(-371.48, -1095.37) * mm, "end": v(-371.48, -1044.57) * mm});
            skLineSegment(sketch, "E296", {"start": v(-365.13, -1044.57) * mm, "end": v(-365.13, -1095.37) * mm});
            skLineSegment(sketch, "E297", {"start": v(-365.13, -930.27) * mm, "end": v(-365.13, -981.07) * mm});
            skLineSegment(sketch, "E298", {"start": v(-371.48, -981.07) * mm, "end": v(-371.48, -930.27) * mm});
            skLineSegment(sketch, "E299", {"start": v(-371.48, -815.97) * mm, "end": v(-371.48, -866.77) * mm});
            skLineSegment(sketch, "E300", {"start": v(-365.13, -815.97) * mm, "end": v(-365.13, -866.77) * mm});
            skLineSegment(sketch, "E301", {"start": v(-371.48, -752.47) * mm, "end": v(-371.48, -701.67) * mm});
            skLineSegment(sketch, "E302", {"start": v(-371.48, -701.67) * mm, "end": v(-365.13, -701.67) * mm});
            skLineSegment(sketch, "E303", {"start": v(-365.13, -701.67) * mm, "end": v(-365.13, -752.47) * mm});
            skLineSegment(sketch, "E304", {"start": v(365.13, -1387.47) * mm, "end": v(365.13, -1438.27) * mm});
            skLineSegment(sketch, "E305", {"start": v(371.48, -1387.47) * mm, "end": v(371.48, -1438.27) * mm});
            skLineSegment(sketch, "E306", {"start": v(365.13, -1273.17) * mm, "end": v(365.13, -1323.97) * mm});
            skLineSegment(sketch, "E307", {"start": v(371.48, -1273.17) * mm, "end": v(371.48, -1323.97) * mm});
            skLineSegment(sketch, "E308", {"start": v(365.13, -1158.87) * mm, "end": v(365.13, -1209.67) * mm});
            skLineSegment(sketch, "E309", {"start": v(371.48, -1158.87) * mm, "end": v(371.48, -1209.67) * mm});
            skLineSegment(sketch, "E310", {"start": v(365.13, -1044.57) * mm, "end": v(365.13, -1095.37) * mm});
            skLineSegment(sketch, "E311", {"start": v(371.48, -1044.57) * mm, "end": v(371.48, -1095.37) * mm});
            skLineSegment(sketch, "E312", {"start": v(365.13, -930.27) * mm, "end": v(365.13, -981.07) * mm});
            skLineSegment(sketch, "E313", {"start": v(371.48, -930.27) * mm, "end": v(371.48, -981.07) * mm});
            skLineSegment(sketch, "E314", {"start": v(365.13, -815.97) * mm, "end": v(365.13, -866.77) * mm});
            skLineSegment(sketch, "E315", {"start": v(371.48, -815.97) * mm, "end": v(371.48, -866.77) * mm});
            skLineSegment(sketch, "E316", {"start": v(365.13, -701.67) * mm, "end": v(365.13, -752.47) * mm});
            skLineSegment(sketch, "E317", {"start": v(371.48, -701.67) * mm, "end": v(371.48, -752.47) * mm});
            skLineSegment(sketch, "E318", {"start": v(365.13, -587.37) * mm, "end": v(365.13, -638.17) * mm});
            skLineSegment(sketch, "E319", {"start": v(371.48, -587.37) * mm, "end": v(371.48, -638.17) * mm});
            skLineSegment(sketch, "E320", {"start": v(365.13, -473.07) * mm, "end": v(365.13, -523.87) * mm});
            skLineSegment(sketch, "E321", {"start": v(371.48, -473.07) * mm, "end": v(371.48, -523.87) * mm});
            skLineSegment(sketch, "E322", {"start": v(365.13, -358.77) * mm, "end": v(365.13, -409.57) * mm});
            skLineSegment(sketch, "E323", {"start": v(371.48, -358.77) * mm, "end": v(371.48, -409.57) * mm});
            skLineSegment(sketch, "E324", {"start": v(365.13, -244.47) * mm, "end": v(365.13, -295.27) * mm});
            skLineSegment(sketch, "E325", {"start": v(371.48, -244.47) * mm, "end": v(371.48, -295.27) * mm});
            skLineSegment(sketch, "E326", {"start": v(365.13, -130.17) * mm, "end": v(365.13, -180.97) * mm});
            skLineSegment(sketch, "E327", {"start": v(371.48, -130.17) * mm, "end": v(371.48, -180.97) * mm});
            skLineSegment(sketch, "E328", {"start": v(365.13, -15.87) * mm, "end": v(365.13, -66.67) * mm});
            skLineSegment(sketch, "E329", {"start": v(371.48, -15.87) * mm, "end": v(371.48, -66.67) * mm});
            skLineSegment(sketch, "E330", {"start": v(365.13, 98.43) * mm, "end": v(365.13, 47.63) * mm});
            skLineSegment(sketch, "E331", {"start": v(371.48, 98.43) * mm, "end": v(371.48, 47.63) * mm});
            skLineSegment(sketch, "E332", {"start": v(365.13, 161.93) * mm, "end": v(365.13, 212.73) * mm});
            skLineSegment(sketch, "E333", {"start": v(371.48, 212.73) * mm, "end": v(371.48, 161.93) * mm});
            skLineSegment(sketch, "E334", {"start": v(365.13, 276.23) * mm, "end": v(365.13, 327.03) * mm});
            skLineSegment(sketch, "E335", {"start": v(371.48, 276.23) * mm, "end": v(371.48, 327.03) * mm});
            skLineSegment(sketch, "E336", {"start": v(365.13, 390.53) * mm, "end": v(365.13, 441.33) * mm});
            skLineSegment(sketch, "E337", {"start": v(371.48, 390.53) * mm, "end": v(371.48, 441.33) * mm});
            skLineSegment(sketch, "E338", {"start": v(-371.48, -295.27) * mm, "end": v(-371.48, -244.47) * mm});
            skLineSegment(sketch, "E339", {"start": v(-365.13, -295.27) * mm, "end": v(-365.13, -244.47) * mm});
            skLineSegment(sketch, "E340", {"start": v(-371.48, -180.97) * mm, "end": v(-371.48, -130.17) * mm});
            skLineSegment(sketch, "E341", {"start": v(-365.13, -180.97) * mm, "end": v(-365.13, -130.17) * mm});
            skLineSegment(sketch, "E342", {"start": v(-371.48, -66.67) * mm, "end": v(-371.48, -15.87) * mm});
            skLineSegment(sketch, "E343", {"start": v(-365.13, -66.67) * mm, "end": v(-365.13, -15.87) * mm});
            skLineSegment(sketch, "E344", {"start": v(-371.48, 47.63) * mm, "end": v(-371.48, 98.43) * mm});
            skLineSegment(sketch, "E345", {"start": v(-365.13, 98.43) * mm, "end": v(-365.13, 47.63) * mm});
            skLineSegment(sketch, "E346", {"start": v(-371.48, 161.93) * mm, "end": v(-371.48, 212.73) * mm});
            skLineSegment(sketch, "E347", {"start": v(-365.13, 161.93) * mm, "end": v(-365.13, 212.73) * mm});
            skLineSegment(sketch, "E348", {"start": v(-371.48, 276.23) * mm, "end": v(-371.48, 327.03) * mm});
            skLineSegment(sketch, "E349", {"start": v(-365.13, 276.23) * mm, "end": v(-365.13, 327.03) * mm});
            skLineSegment(sketch, "E350", {"start": v(-371.48, 441.33) * mm, "end": v(-371.48, 390.53) * mm});
            skLineSegment(sketch, "E351", {"start": v(-365.13, 390.53) * mm, "end": v(-365.13, 441.33) * mm});
            skSolve(sketch);
        }
        {
            var Q0;
            {var subQ0=sQuery(id+"F4.wireOp",EDGE,"E90.0");var subQ1=sQuery(id+"F4.wireOp",EDGE,"E72.0");var subQ2=makeQuery(id+"F4.imprint","INTERSECT",VERTEX,{"derivedFrom":[subQ1,subQ0]});Q0=makeQuery(id+"F4.imprint","IMPRINT",FACE,{"disambiguationData":[TD([[makeQuery(id+"F4.imprint","IMPRINT",EDGE,{"disambiguationData":[TD([[subQ2,-1.0]])],"derivedFrom":subQ1}),1.0]])]});}
            var Q1;
            {var subQ0=sQuery(id+"F4.wireOp",EDGE,"E224.trimOffspring");var subQ1=sQuery(id+"F4.wireOp",EDGE,"E90.0");var subQ2=makeQuery(id+"F4.imprint","INTERSECT",VERTEX,{"derivedFrom":[subQ1,subQ0]});Q1=makeQuery(id+"F4.imprint","IMPRINT",FACE,{"disambiguationData":[TD([[makeQuery(id+"F4.imprint","IMPRINT",EDGE,{"disambiguationData":[TD([[subQ2,-1.0]])],"derivedFrom":subQ1}),1.0]])]});}
            var Q2;
            {var subQ0=sQuery(id+"F4.wireOp",EDGE,"E90.0");var subQ1=sQuery(id+"F4.wireOp",EDGE,"E70.0");var subQ2=makeQuery(id+"F4.imprint","INTERSECT",VERTEX,{"derivedFrom":[subQ1,subQ0]});Q2=makeQuery(id+"F4.imprint","IMPRINT",FACE,{"disambiguationData":[TD([[makeQuery(id+"F4.imprint","IMPRINT",EDGE,{"disambiguationData":[TD([[subQ2,1.0]])],"derivedFrom":subQ1}),1.0]])]});}
            var Q3;
            {var subQ0=sQuery(id+"F4.wireOp",EDGE,"E224.trimOffspring");var subQ1=sQuery(id+"F4.wireOp",EDGE,"E89.0");var subQ2=makeQuery(id+"F4.imprint","INTERSECT",VERTEX,{"derivedFrom":[subQ1,subQ0]});Q3=makeQuery(id+"F4.imprint","IMPRINT",FACE,{"disambiguationData":[TD([[makeQuery(id+"F4.imprint","IMPRINT",EDGE,{"disambiguationData":[TD([[subQ2,-1.0]])],"derivedFrom":subQ1}),1.0]])]});}
            var Q4;
            {var subQ0=sQuery(id+"F4.wireOp",EDGE,"E88.0");var subQ1=sQuery(id+"F4.wireOp",EDGE,"E70.0");var subQ2=makeQuery(id+"F4.imprint","INTERSECT",VERTEX,{"derivedFrom":[subQ1,subQ0]});Q4=makeQuery(id+"F4.imprint","IMPRINT",FACE,{"disambiguationData":[TD([[makeQuery(id+"F4.imprint","IMPRINT",EDGE,{"disambiguationData":[TD([[subQ2,1.0]])],"derivedFrom":subQ1}),1.0]])]});}
            var Q5;
            {var subQ0=sQuery(id+"F4.wireOp",EDGE,"E224.trimOffspring");var subQ1=sQuery(id+"F4.wireOp",EDGE,"E88.0");var subQ2=makeQuery(id+"F4.imprint","INTERSECT",VERTEX,{"derivedFrom":[subQ1,subQ0]});Q5=makeQuery(id+"F4.imprint","IMPRINT",FACE,{"disambiguationData":[TD([[makeQuery(id+"F4.imprint","IMPRINT",EDGE,{"disambiguationData":[TD([[subQ2,-1.0]])],"derivedFrom":subQ1}),1.0]])]});}
            var Q6;
            {var subQ0=sQuery(id+"F4.wireOp",EDGE,"E88.0");var subQ1=sQuery(id+"F4.wireOp",EDGE,"E72.0");var subQ2=makeQuery(id+"F4.imprint","INTERSECT",VERTEX,{"derivedFrom":[subQ1,subQ0]});Q6=makeQuery(id+"F4.imprint","IMPRINT",FACE,{"disambiguationData":[TD([[makeQuery(id+"F4.imprint","IMPRINT",EDGE,{"disambiguationData":[TD([[subQ2,-1.0]])],"derivedFrom":subQ1}),1.0]])]});}
            var Q7;
            {var subQ0=sQuery(id+"F4.wireOp",EDGE,"E86.0");var subQ1=sQuery(id+"F4.wireOp",EDGE,"E70.0");var subQ2=makeQuery(id+"F4.imprint","INTERSECT",VERTEX,{"derivedFrom":[subQ1,subQ0]});Q7=makeQuery(id+"F4.imprint","IMPRINT",FACE,{"disambiguationData":[TD([[makeQuery(id+"F4.imprint","IMPRINT",EDGE,{"disambiguationData":[TD([[subQ2,1.0]])],"derivedFrom":subQ1}),1.0]])]});}
            var Q8;
            {var subQ0=sQuery(id+"F4.wireOp",EDGE,"E220.trimOffspring");var subQ1=sQuery(id+"F4.wireOp",EDGE,"E86.0");var subQ2=makeQuery(id+"F4.imprint","INTERSECT",VERTEX,{"derivedFrom":[subQ1,subQ0]});Q8=makeQuery(id+"F4.imprint","IMPRINT",FACE,{"disambiguationData":[TD([[makeQuery(id+"F4.imprint","IMPRINT",EDGE,{"disambiguationData":[TD([[subQ2,-1.0]])],"derivedFrom":subQ1}),1.0]])]});}
            var Q9;
            {var subQ0=sQuery(id+"F4.wireOp",EDGE,"E86.0");var subQ1=sQuery(id+"F4.wireOp",EDGE,"E72.0");var subQ2=makeQuery(id+"F4.imprint","INTERSECT",VERTEX,{"derivedFrom":[subQ1,subQ0]});Q9=makeQuery(id+"F4.imprint","IMPRINT",FACE,{"disambiguationData":[TD([[makeQuery(id+"F4.imprint","IMPRINT",EDGE,{"disambiguationData":[TD([[subQ2,-1.0]])],"derivedFrom":subQ1}),1.0]])]});}
            var Q10;
            {var subQ0=sQuery(id+"F4.wireOp",EDGE,"E220.trimOffspring");var subQ1=sQuery(id+"F4.wireOp",EDGE,"E85.0");var subQ2=makeQuery(id+"F4.imprint","INTERSECT",VERTEX,{"derivedFrom":[subQ1,subQ0]});Q10=makeQuery(id+"F4.imprint","IMPRINT",FACE,{"disambiguationData":[TD([[makeQuery(id+"F4.imprint","IMPRINT",EDGE,{"disambiguationData":[TD([[subQ2,-1.0]])],"derivedFrom":subQ1}),1.0]])]});}
            var Q11;
            {var subQ0=sQuery(id+"F4.wireOp",EDGE,"E220.trimOffspring");var subQ1=sQuery(id+"F4.wireOp",EDGE,"E84.0");var subQ2=makeQuery(id+"F4.imprint","INTERSECT",VERTEX,{"derivedFrom":[subQ1,subQ0]});Q11=makeQuery(id+"F4.imprint","IMPRINT",FACE,{"disambiguationData":[TD([[makeQuery(id+"F4.imprint","IMPRINT",EDGE,{"disambiguationData":[TD([[subQ2,-1.0]])],"derivedFrom":subQ1}),1.0]])]});}
            var Q12;
            {var subQ0=sQuery(id+"F4.wireOp",EDGE,"E84.0");var subQ1=sQuery(id+"F4.wireOp",EDGE,"E70.0");var subQ2=makeQuery(id+"F4.imprint","INTERSECT",VERTEX,{"derivedFrom":[subQ1,subQ0]});Q12=makeQuery(id+"F4.imprint","IMPRINT",FACE,{"disambiguationData":[TD([[makeQuery(id+"F4.imprint","IMPRINT",EDGE,{"disambiguationData":[TD([[subQ2,1.0]])],"derivedFrom":subQ1}),1.0]])]});}
            var Q13;
            {var subQ0=sQuery(id+"F4.wireOp",EDGE,"E84.0");var subQ1=sQuery(id+"F4.wireOp",EDGE,"E72.0");var subQ2=makeQuery(id+"F4.imprint","INTERSECT",VERTEX,{"derivedFrom":[subQ1,subQ0]});Q13=makeQuery(id+"F4.imprint","IMPRINT",FACE,{"disambiguationData":[TD([[makeQuery(id+"F4.imprint","IMPRINT",EDGE,{"disambiguationData":[TD([[subQ2,-1.0]])],"derivedFrom":subQ1}),1.0]])]});}
            var Q14;
            {var subQ3=sQuery(id+"F4.wireOp",EDGE,"E82.0");Q14=makeQuery(id+"F4.imprint","IMPRINT",FACE,{"disambiguationData":[TD([[makeQuery(id+"F4.imprint","IMPRINT",EDGE,{"derivedFrom":subQ3}),1.0]])]});}
            var Q15;
            {var subQ0=sQuery(id+"F4.wireOp",EDGE,"E218.trimOffspring");Q15=makeQuery(id+"F4.imprint","IMPRINT",FACE,{"disambiguationData":[TD([[makeQuery(id+"F4.imprint","IMPRINT",EDGE,{"derivedFrom":subQ0}),-1.0]])]});}
            var Q16;
            {var subQ0=sQuery(id+"F4.wireOp",EDGE,"E80.0");Q16=makeQuery(id+"F4.imprint","IMPRINT",FACE,{"disambiguationData":[TD([[makeQuery(id+"F4.imprint","IMPRINT",EDGE,{"derivedFrom":subQ0}),1.0]])]});}
            var Q17;
            {var subQ0=sQuery(id+"F4.wireOp",EDGE,"E78");var subQ1=sQuery(id+"F4.wireOp",EDGE,"E70.0");var subQ2=makeQuery(id+"F4.imprint","INTERSECT",VERTEX,{"derivedFrom":[subQ1,subQ0]});Q17=makeQuery(id+"F4.imprint","IMPRINT",FACE,{"disambiguationData":[TD([[makeQuery(id+"F4.imprint","IMPRINT",EDGE,{"disambiguationData":[TD([[subQ2,1.0]])],"derivedFrom":subQ1}),1.0]])]});}
            var Q18;
            {var subQ0=sQuery(id+"F4.wireOp",EDGE,"E78");var subQ1=sQuery(id+"F4.wireOp",EDGE,"E72.0");var subQ2=makeQuery(id+"F4.imprint","INTERSECT",VERTEX,{"derivedFrom":[subQ1,subQ0]});Q18=makeQuery(id+"F4.imprint","IMPRINT",FACE,{"disambiguationData":[TD([[makeQuery(id+"F4.imprint","IMPRINT",EDGE,{"disambiguationData":[TD([[subQ2,-1.0]])],"derivedFrom":subQ1}),1.0]])]});}
            var Q19;
            {var subQ0=sQuery(id+"F4.wireOp",EDGE,"E216.0");var subQ1=sQuery(id+"F4.wireOp",EDGE,"E78");var subQ2=makeQuery(id+"F4.imprint","INTERSECT",VERTEX,{"derivedFrom":[subQ1,subQ0]});Q19=makeQuery(id+"F4.imprint","IMPRINT",FACE,{"disambiguationData":[TD([[makeQuery(id+"F4.imprint","IMPRINT",EDGE,{"disambiguationData":[TD([[subQ2,-1.0]])],"derivedFrom":subQ1}),1.0]])]});}
            var Q20;
            {var subQ0=sQuery(id+"F4.wireOp",EDGE,"E215.0");var subQ1=sQuery(id+"F4.wireOp",EDGE,"E73.0");var subQ2=makeQuery(id+"F4.imprint","INTERSECT",VERTEX,{"derivedFrom":[subQ1,subQ0]});Q20=makeQuery(id+"F4.imprint","IMPRINT",FACE,{"disambiguationData":[TD([[makeQuery(id+"F4.imprint","IMPRINT",EDGE,{"disambiguationData":[TD([[subQ2,1.0]])],"derivedFrom":subQ1}),1.0]])]});}
            var Q21;
            {var subQ0=sQuery(id+"F4.wireOp",EDGE,"E227.trimOffspring");var subQ1=sQuery(id+"F4.wireOp",EDGE,"E92.0");var subQ2=makeQuery(id+"F4.imprint","INTERSECT",VERTEX,{"derivedFrom":[subQ1,subQ0]});Q21=makeQuery(id+"F4.imprint","IMPRINT",FACE,{"disambiguationData":[TD([[makeQuery(id+"F4.imprint","IMPRINT",EDGE,{"disambiguationData":[TD([[subQ2,-1.0]])],"derivedFrom":subQ1}),1.0]])]});}
            var Q22;
            {var subQ0=sQuery(id+"F4.wireOp",EDGE,"E92.0");var subQ1=sQuery(id+"F4.wireOp",EDGE,"E70.0");var subQ2=makeQuery(id+"F4.imprint","INTERSECT",VERTEX,{"derivedFrom":[subQ1,subQ0]});Q22=makeQuery(id+"F4.imprint","IMPRINT",FACE,{"disambiguationData":[TD([[makeQuery(id+"F4.imprint","IMPRINT",EDGE,{"disambiguationData":[TD([[subQ2,1.0]])],"derivedFrom":subQ1}),1.0]])]});}
            var Q23;
            {var subQ0=sQuery(id+"F4.wireOp",EDGE,"E92.0");var subQ1=sQuery(id+"F4.wireOp",EDGE,"E72.0");var subQ2=makeQuery(id+"F4.imprint","INTERSECT",VERTEX,{"derivedFrom":[subQ1,subQ0]});Q23=makeQuery(id+"F4.imprint","IMPRINT",FACE,{"disambiguationData":[TD([[makeQuery(id+"F4.imprint","IMPRINT",EDGE,{"disambiguationData":[TD([[subQ2,-1.0]])],"derivedFrom":subQ1}),1.0]])]});}
            var Q24;
            {var subQ0=sQuery(id+"F4.wireOp",EDGE,"E227.trimOffspring");var subQ1=sQuery(id+"F4.wireOp",EDGE,"E93.0");var subQ2=makeQuery(id+"F4.imprint","INTERSECT",VERTEX,{"derivedFrom":[subQ1,subQ0]});Q24=makeQuery(id+"F4.imprint","IMPRINT",FACE,{"disambiguationData":[TD([[makeQuery(id+"F4.imprint","IMPRINT",EDGE,{"disambiguationData":[TD([[subQ2,-1.0]])],"derivedFrom":subQ1}),1.0]])]});}
            var Q25;
            {var subQ0=sQuery(id+"F4.wireOp",EDGE,"E94.0");var subQ1=sQuery(id+"F4.wireOp",EDGE,"E70.0");var subQ2=makeQuery(id+"F4.imprint","INTERSECT",VERTEX,{"derivedFrom":[subQ1,subQ0]});Q25=makeQuery(id+"F4.imprint","IMPRINT",FACE,{"disambiguationData":[TD([[makeQuery(id+"F4.imprint","IMPRINT",EDGE,{"disambiguationData":[TD([[subQ2,1.0]])],"derivedFrom":subQ1}),1.0]])]});}
            var Q26;
            {var subQ0=sQuery(id+"F4.wireOp",EDGE,"E227.trimOffspring");var subQ1=sQuery(id+"F4.wireOp",EDGE,"E94.0");var subQ2=makeQuery(id+"F4.imprint","INTERSECT",VERTEX,{"derivedFrom":[subQ1,subQ0]});Q26=makeQuery(id+"F4.imprint","IMPRINT",FACE,{"disambiguationData":[TD([[makeQuery(id+"F4.imprint","IMPRINT",EDGE,{"disambiguationData":[TD([[subQ2,-1.0]])],"derivedFrom":subQ1}),1.0]])]});}
            var Q27;
            {var subQ0=sQuery(id+"F4.wireOp",EDGE,"E94.0");var subQ1=sQuery(id+"F4.wireOp",EDGE,"E72.0");var subQ2=makeQuery(id+"F4.imprint","INTERSECT",VERTEX,{"derivedFrom":[subQ1,subQ0]});Q27=makeQuery(id+"F4.imprint","IMPRINT",FACE,{"disambiguationData":[TD([[makeQuery(id+"F4.imprint","IMPRINT",EDGE,{"disambiguationData":[TD([[subQ2,-1.0]])],"derivedFrom":subQ1}),1.0]])]});}
            var Q28;
            {var subQ0=sQuery(id+"F4.wireOp",EDGE,"E98.0");var subQ1=sQuery(id+"F4.wireOp",EDGE,"E72.0");var subQ2=makeQuery(id+"F4.imprint","INTERSECT",VERTEX,{"derivedFrom":[subQ1,subQ0]});Q28=makeQuery(id+"F4.imprint","IMPRINT",FACE,{"disambiguationData":[TD([[makeQuery(id+"F4.imprint","IMPRINT",EDGE,{"disambiguationData":[TD([[subQ2,-1.0]])],"derivedFrom":subQ1}),1.0]])]});}
            var Q29;
            {var subQ0=sQuery(id+"F4.wireOp",EDGE,"E98.0");var subQ1=sQuery(id+"F4.wireOp",EDGE,"E70.0");var subQ2=makeQuery(id+"F4.imprint","INTERSECT",VERTEX,{"derivedFrom":[subQ1,subQ0]});Q29=makeQuery(id+"F4.imprint","IMPRINT",FACE,{"disambiguationData":[TD([[makeQuery(id+"F4.imprint","IMPRINT",EDGE,{"disambiguationData":[TD([[subQ2,1.0]])],"derivedFrom":subQ1}),1.0]])]});}
            var Q30;
            {var subQ0=sQuery(id+"F4.wireOp",EDGE,"E229.trimOffspring");var subQ1=sQuery(id+"F4.wireOp",EDGE,"E98.0");var subQ2=makeQuery(id+"F4.imprint","INTERSECT",VERTEX,{"derivedFrom":[subQ1,subQ0]});Q30=makeQuery(id+"F4.imprint","IMPRINT",FACE,{"disambiguationData":[TD([[makeQuery(id+"F4.imprint","IMPRINT",EDGE,{"disambiguationData":[TD([[subQ2,-1.0]])],"derivedFrom":subQ1}),1.0]])]});}
            var Q31;
            {var subQ0=sQuery(id+"F4.wireOp",EDGE,"E229.trimOffspring");var subQ1=sQuery(id+"F4.wireOp",EDGE,"E96.0");var subQ2=makeQuery(id+"F4.imprint","INTERSECT",VERTEX,{"derivedFrom":[subQ1,subQ0]});Q31=makeQuery(id+"F4.imprint","IMPRINT",FACE,{"disambiguationData":[TD([[makeQuery(id+"F4.imprint","IMPRINT",EDGE,{"disambiguationData":[TD([[subQ2,-1.0]])],"derivedFrom":subQ1}),1.0]])]});}
            var Q32;
            {var subQ0=sQuery(id+"F4.wireOp",EDGE,"E96.0");var subQ1=sQuery(id+"F4.wireOp",EDGE,"E72.0");var subQ2=makeQuery(id+"F4.imprint","INTERSECT",VERTEX,{"derivedFrom":[subQ1,subQ0]});Q32=makeQuery(id+"F4.imprint","IMPRINT",FACE,{"disambiguationData":[TD([[makeQuery(id+"F4.imprint","IMPRINT",EDGE,{"disambiguationData":[TD([[subQ2,-1.0]])],"derivedFrom":subQ1}),1.0]])]});}
            var Q33;
            {var subQ0=sQuery(id+"F4.wireOp",EDGE,"E229.trimOffspring");var subQ1=sQuery(id+"F4.wireOp",EDGE,"E97.0");var subQ2=makeQuery(id+"F4.imprint","INTERSECT",VERTEX,{"derivedFrom":[subQ1,subQ0]});Q33=makeQuery(id+"F4.imprint","IMPRINT",FACE,{"disambiguationData":[TD([[makeQuery(id+"F4.imprint","IMPRINT",EDGE,{"disambiguationData":[TD([[subQ2,-1.0]])],"derivedFrom":subQ1}),1.0]])]});}
            var Q34;
            {var subQ0=sQuery(id+"F4.wireOp",EDGE,"E96.0");var subQ1=sQuery(id+"F4.wireOp",EDGE,"E70.0");var subQ2=makeQuery(id+"F4.imprint","INTERSECT",VERTEX,{"derivedFrom":[subQ1,subQ0]});Q34=makeQuery(id+"F4.imprint","IMPRINT",FACE,{"disambiguationData":[TD([[makeQuery(id+"F4.imprint","IMPRINT",EDGE,{"disambiguationData":[TD([[subQ2,1.0]])],"derivedFrom":subQ1}),1.0]])]});}
            var Q35;
            {var subQ0=sQuery(id+"F4.wireOp",EDGE,"E231.trimOffspring");var subQ1=sQuery(id+"F4.wireOp",EDGE,"E100.0");var subQ2=makeQuery(id+"F4.imprint","INTERSECT",VERTEX,{"derivedFrom":[subQ1,subQ0]});Q35=makeQuery(id+"F4.imprint","IMPRINT",FACE,{"disambiguationData":[TD([[makeQuery(id+"F4.imprint","IMPRINT",EDGE,{"disambiguationData":[TD([[subQ2,-1.0]])],"derivedFrom":subQ1}),1.0]])]});}
            var Q36;
            {var subQ0=sQuery(id+"F4.wireOp",EDGE,"E100.0");var subQ1=sQuery(id+"F4.wireOp",EDGE,"E70.0");var subQ2=makeQuery(id+"F4.imprint","INTERSECT",VERTEX,{"derivedFrom":[subQ1,subQ0]});Q36=makeQuery(id+"F4.imprint","IMPRINT",FACE,{"disambiguationData":[TD([[makeQuery(id+"F4.imprint","IMPRINT",EDGE,{"disambiguationData":[TD([[subQ2,1.0]])],"derivedFrom":subQ1}),1.0]])]});}
            var Q37;
            {var subQ0=sQuery(id+"F4.wireOp",EDGE,"E100.0");var subQ1=sQuery(id+"F4.wireOp",EDGE,"E72.0");var subQ2=makeQuery(id+"F4.imprint","INTERSECT",VERTEX,{"derivedFrom":[subQ1,subQ0]});Q37=makeQuery(id+"F4.imprint","IMPRINT",FACE,{"disambiguationData":[TD([[makeQuery(id+"F4.imprint","IMPRINT",EDGE,{"disambiguationData":[TD([[subQ2,-1.0]])],"derivedFrom":subQ1}),1.0]])]});}
            var Q38;
            {var subQ0=sQuery(id+"F4.wireOp",EDGE,"E231.trimOffspring");var subQ1=sQuery(id+"F4.wireOp",EDGE,"E101.0");var subQ2=makeQuery(id+"F4.imprint","INTERSECT",VERTEX,{"derivedFrom":[subQ1,subQ0]});Q38=makeQuery(id+"F4.imprint","IMPRINT",FACE,{"disambiguationData":[TD([[makeQuery(id+"F4.imprint","IMPRINT",EDGE,{"disambiguationData":[TD([[subQ2,-1.0]])],"derivedFrom":subQ1}),1.0]])]});}
            var Q39;
            {var subQ0=sQuery(id+"F4.wireOp",EDGE,"E231.trimOffspring");var subQ1=sQuery(id+"F4.wireOp",EDGE,"E102.0");var subQ2=makeQuery(id+"F4.imprint","INTERSECT",VERTEX,{"derivedFrom":[subQ1,subQ0]});Q39=makeQuery(id+"F4.imprint","IMPRINT",FACE,{"disambiguationData":[TD([[makeQuery(id+"F4.imprint","IMPRINT",EDGE,{"disambiguationData":[TD([[subQ2,-1.0]])],"derivedFrom":subQ1}),1.0]])]});}
            var Q40;
            {var subQ0=sQuery(id+"F4.wireOp",EDGE,"E102.0");var subQ1=sQuery(id+"F4.wireOp",EDGE,"E70.0");var subQ2=makeQuery(id+"F4.imprint","INTERSECT",VERTEX,{"derivedFrom":[subQ1,subQ0]});Q40=makeQuery(id+"F4.imprint","IMPRINT",FACE,{"disambiguationData":[TD([[makeQuery(id+"F4.imprint","IMPRINT",EDGE,{"disambiguationData":[TD([[subQ2,1.0]])],"derivedFrom":subQ1}),1.0]])]});}
            var Q41;
            {var subQ0=sQuery(id+"F4.wireOp",EDGE,"E102.0");var subQ1=sQuery(id+"F4.wireOp",EDGE,"E72.0");var subQ2=makeQuery(id+"F4.imprint","INTERSECT",VERTEX,{"derivedFrom":[subQ1,subQ0]});Q41=makeQuery(id+"F4.imprint","IMPRINT",FACE,{"disambiguationData":[TD([[makeQuery(id+"F4.imprint","IMPRINT",EDGE,{"disambiguationData":[TD([[subQ2,-1.0]])],"derivedFrom":subQ1}),1.0]])]});}
            var Q42;
            {var subQ0=sQuery(id+"F4.wireOp",EDGE,"E104.0");Q42=makeQuery(id+"F4.imprint","IMPRINT",FACE,{"disambiguationData":[TD([[makeQuery(id+"F4.imprint","IMPRINT",EDGE,{"derivedFrom":subQ0}),1.0]])]});}
            var Q43;
            {var subQ0=sQuery(id+"F4.wireOp",EDGE,"E217.trimOffspring");var subQ1=sQuery(id+"F4.wireOp",EDGE,"E71.0");var subQ2=makeQuery(id+"F4.imprint","INTERSECT",VERTEX,{"derivedFrom":[subQ1,subQ0]});Q43=makeQuery(id+"F4.imprint","IMPRINT",FACE,{"disambiguationData":[TD([[makeQuery(id+"F4.imprint","IMPRINT",EDGE,{"disambiguationData":[TD([[subQ2,-1.0]])],"derivedFrom":subQ1}),1.0]])]});}
            extrude(context, id + "F5", {"entities" : qUnion([Q0, Q1, Q2, Q3, Q4, Q5, Q6, Q7, Q8, Q9, Q10, Q11, Q12, Q13, Q14, Q15, Q16, Q17, Q18, Q19, Q20, Q21, Q22, Q23, Q24, Q25, Q26, Q27, Q28, Q29, Q30, Q31, Q32, Q33, Q34, Q35, Q36, Q37, Q38, Q39, Q40, Q41, Q42, Q43]), "operationType" : NewBodyOperationType.ADD, "depth" : 28.57 * mm, "offsetDistance" : 25.4 * mm});
        }
        {
            var Q0;
            {var subQ0=sQuery(id+"F4.wireOp",EDGE,"E237.trimOffspring");var subQ1=sQuery(id+"F4.wireOp",EDGE,"E117.0");var subQ2=makeQuery(id+"F4.imprint","INTERSECT",VERTEX,{"derivedFrom":[subQ1,subQ0]});Q0=makeQuery(id+"F4.imprint","IMPRINT",FACE,{"disambiguationData":[TD([[makeQuery(id+"F4.imprint","IMPRINT",EDGE,{"disambiguationData":[TD([[subQ2,-1.0]])],"derivedFrom":subQ1}),1.0]])]});}
            var Q1;
            {var subQ0=sQuery(id+"F4.wireOp",EDGE,"E237.trimOffspring");var subQ1=sQuery(id+"F4.wireOp",EDGE,"E118.0");var subQ2=makeQuery(id+"F4.imprint","INTERSECT",VERTEX,{"derivedFrom":[subQ1,subQ0]});Q1=makeQuery(id+"F4.imprint","IMPRINT",FACE,{"disambiguationData":[TD([[makeQuery(id+"F4.imprint","IMPRINT",EDGE,{"disambiguationData":[TD([[subQ2,-1.0]])],"derivedFrom":subQ1}),1.0]])]});}
            var Q2;
            {var subQ0=sQuery(id+"F4.wireOp",EDGE,"E118.0");var subQ1=sQuery(id+"F4.wireOp",EDGE,"E67.0");var subQ2=makeQuery(id+"F4.imprint","INTERSECT",VERTEX,{"derivedFrom":[subQ1,subQ0]});Q2=makeQuery(id+"F4.imprint","IMPRINT",FACE,{"disambiguationData":[TD([[makeQuery(id+"F4.imprint","IMPRINT",EDGE,{"disambiguationData":[TD([[subQ2,1.0]])],"derivedFrom":subQ1}),1.0]])]});}
            var Q3;
            {var subQ0=sQuery(id+"F4.wireOp",EDGE,"E121.0");var subQ1=sQuery(id+"F4.wireOp",EDGE,"E68.0");var subQ2=makeQuery(id+"F4.imprint","INTERSECT",VERTEX,{"derivedFrom":[subQ1,subQ0]});Q3=makeQuery(id+"F4.imprint","IMPRINT",FACE,{"disambiguationData":[TD([[makeQuery(id+"F4.imprint","IMPRINT",EDGE,{"disambiguationData":[TD([[subQ2,-1.0]])],"derivedFrom":subQ1}),-1.0]])]});}
            var Q4;
            {var subQ0=sQuery(id+"F4.wireOp",EDGE,"E123.0");var subQ1=sQuery(id+"F4.wireOp",EDGE,"E68.0");var subQ2=makeQuery(id+"F4.imprint","INTERSECT",VERTEX,{"derivedFrom":[subQ1,subQ0]});Q4=makeQuery(id+"F4.imprint","IMPRINT",FACE,{"disambiguationData":[TD([[makeQuery(id+"F4.imprint","IMPRINT",EDGE,{"disambiguationData":[TD([[subQ2,-1.0]])],"derivedFrom":subQ1}),-1.0]])]});}
            var Q5;
            {var subQ0=sQuery(id+"F4.wireOp",EDGE,"E238.trimOffspring");var subQ1=sQuery(id+"F4.wireOp",EDGE,"E122.0");var subQ2=makeQuery(id+"F4.imprint","INTERSECT",VERTEX,{"derivedFrom":[subQ1,subQ0]});Q5=makeQuery(id+"F4.imprint","IMPRINT",FACE,{"disambiguationData":[TD([[makeQuery(id+"F4.imprint","IMPRINT",EDGE,{"disambiguationData":[TD([[subQ2,-1.0]])],"derivedFrom":subQ1}),1.0]])]});}
            var Q6;
            {var subQ0=sQuery(id+"F4.wireOp",EDGE,"E122.0");var subQ1=sQuery(id+"F4.wireOp",EDGE,"E67.0");var subQ2=makeQuery(id+"F4.imprint","INTERSECT",VERTEX,{"derivedFrom":[subQ1,subQ0]});Q6=makeQuery(id+"F4.imprint","IMPRINT",FACE,{"disambiguationData":[TD([[makeQuery(id+"F4.imprint","IMPRINT",EDGE,{"disambiguationData":[TD([[subQ2,1.0]])],"derivedFrom":subQ1}),1.0]])]});}
            var Q7;
            {var subQ0=sQuery(id+"F4.wireOp",EDGE,"E238.trimOffspring");var subQ1=sQuery(id+"F4.wireOp",EDGE,"E123.0");var subQ2=makeQuery(id+"F4.imprint","INTERSECT",VERTEX,{"derivedFrom":[subQ1,subQ0]});Q7=makeQuery(id+"F4.imprint","IMPRINT",FACE,{"disambiguationData":[TD([[makeQuery(id+"F4.imprint","IMPRINT",EDGE,{"disambiguationData":[TD([[subQ2,-1.0]])],"derivedFrom":subQ1}),1.0]])]});}
            var Q8;
            {var subQ0=sQuery(id+"F4.wireOp",EDGE,"E238.trimOffspring");var subQ1=sQuery(id+"F4.wireOp",EDGE,"E124.0");var subQ2=makeQuery(id+"F4.imprint","INTERSECT",VERTEX,{"derivedFrom":[subQ1,subQ0]});Q8=makeQuery(id+"F4.imprint","IMPRINT",FACE,{"disambiguationData":[TD([[makeQuery(id+"F4.imprint","IMPRINT",EDGE,{"disambiguationData":[TD([[subQ2,-1.0]])],"derivedFrom":subQ1}),1.0]])]});}
            var Q9;
            {var subQ0=sQuery(id+"F4.wireOp",EDGE,"E124.0");var subQ1=sQuery(id+"F4.wireOp",EDGE,"E67.0");var subQ2=makeQuery(id+"F4.imprint","INTERSECT",VERTEX,{"derivedFrom":[subQ1,subQ0]});Q9=makeQuery(id+"F4.imprint","IMPRINT",FACE,{"disambiguationData":[TD([[makeQuery(id+"F4.imprint","IMPRINT",EDGE,{"disambiguationData":[TD([[subQ2,1.0]])],"derivedFrom":subQ1}),1.0]])]});}
            var Q10;
            {var subQ0=sQuery(id+"F4.wireOp",EDGE,"E125.0");var subQ1=sQuery(id+"F4.wireOp",EDGE,"E68.0");var subQ2=makeQuery(id+"F4.imprint","INTERSECT",VERTEX,{"derivedFrom":[subQ1,subQ0]});Q10=makeQuery(id+"F4.imprint","IMPRINT",FACE,{"disambiguationData":[TD([[makeQuery(id+"F4.imprint","IMPRINT",EDGE,{"disambiguationData":[TD([[subQ2,-1.0]])],"derivedFrom":subQ1}),-1.0]])]});}
            var Q11;
            {var subQ0=sQuery(id+"F4.wireOp",EDGE,"E126.0");var subQ1=sQuery(id+"F4.wireOp",EDGE,"E67.0");var subQ2=makeQuery(id+"F4.imprint","INTERSECT",VERTEX,{"derivedFrom":[subQ1,subQ0]});Q11=makeQuery(id+"F4.imprint","IMPRINT",FACE,{"disambiguationData":[TD([[makeQuery(id+"F4.imprint","IMPRINT",EDGE,{"disambiguationData":[TD([[subQ2,1.0]])],"derivedFrom":subQ1}),1.0]])]});}
            var Q12;
            {var subQ0=sQuery(id+"F4.wireOp",EDGE,"E126.0");var subQ1=sQuery(id+"F4.wireOp",EDGE,"E68.0");var subQ2=makeQuery(id+"F4.imprint","INTERSECT",VERTEX,{"derivedFrom":[subQ1,subQ0]});Q12=makeQuery(id+"F4.imprint","IMPRINT",FACE,{"disambiguationData":[TD([[makeQuery(id+"F4.imprint","IMPRINT",EDGE,{"disambiguationData":[TD([[subQ2,1.0]])],"derivedFrom":subQ1}),-1.0]])]});}
            var Q13;
            {var subQ0=sQuery(id+"F4.wireOp",EDGE,"E240.trimOffspring");var subQ1=sQuery(id+"F4.wireOp",EDGE,"E127.0");var subQ2=makeQuery(id+"F4.imprint","INTERSECT",VERTEX,{"derivedFrom":[subQ1,subQ0]});Q13=makeQuery(id+"F4.imprint","IMPRINT",FACE,{"disambiguationData":[TD([[makeQuery(id+"F4.imprint","IMPRINT",EDGE,{"disambiguationData":[TD([[subQ2,-1.0]])],"derivedFrom":subQ1}),1.0]])]});}
            var Q14;
            {var subQ0=sQuery(id+"F4.wireOp",EDGE,"E240.trimOffspring");var subQ1=sQuery(id+"F4.wireOp",EDGE,"E126.0");var subQ2=makeQuery(id+"F4.imprint","INTERSECT",VERTEX,{"derivedFrom":[subQ1,subQ0]});Q14=makeQuery(id+"F4.imprint","IMPRINT",FACE,{"disambiguationData":[TD([[makeQuery(id+"F4.imprint","IMPRINT",EDGE,{"disambiguationData":[TD([[subQ2,-1.0]])],"derivedFrom":subQ1}),1.0]])]});}
            var Q15;
            {var subQ0=sQuery(id+"F4.wireOp",EDGE,"E240.trimOffspring");var subQ1=sQuery(id+"F4.wireOp",EDGE,"E128.0");var subQ2=makeQuery(id+"F4.imprint","INTERSECT",VERTEX,{"derivedFrom":[subQ1,subQ0]});Q15=makeQuery(id+"F4.imprint","IMPRINT",FACE,{"disambiguationData":[TD([[makeQuery(id+"F4.imprint","IMPRINT",EDGE,{"disambiguationData":[TD([[subQ2,-1.0]])],"derivedFrom":subQ1}),1.0]])]});}
            var Q16;
            {var subQ0=sQuery(id+"F4.wireOp",EDGE,"E128.0");var subQ1=sQuery(id+"F4.wireOp",EDGE,"E67.0");var subQ2=makeQuery(id+"F4.imprint","INTERSECT",VERTEX,{"derivedFrom":[subQ1,subQ0]});Q16=makeQuery(id+"F4.imprint","IMPRINT",FACE,{"disambiguationData":[TD([[makeQuery(id+"F4.imprint","IMPRINT",EDGE,{"disambiguationData":[TD([[subQ2,1.0]])],"derivedFrom":subQ1}),1.0]])]});}
            var Q17;
            {var subQ0=sQuery(id+"F4.wireOp",EDGE,"E128.0");var subQ1=sQuery(id+"F4.wireOp",EDGE,"E68.0");var subQ2=makeQuery(id+"F4.imprint","INTERSECT",VERTEX,{"derivedFrom":[subQ1,subQ0]});Q17=makeQuery(id+"F4.imprint","IMPRINT",FACE,{"disambiguationData":[TD([[makeQuery(id+"F4.imprint","IMPRINT",EDGE,{"disambiguationData":[TD([[subQ2,1.0]])],"derivedFrom":subQ1}),-1.0]])]});}
            var Q18;
            {var subQ0=sQuery(id+"F4.wireOp",EDGE,"E130.0");var subQ1=sQuery(id+"F4.wireOp",EDGE,"E67.0");var subQ2=makeQuery(id+"F4.imprint","INTERSECT",VERTEX,{"derivedFrom":[subQ1,subQ0]});Q18=makeQuery(id+"F4.imprint","IMPRINT",FACE,{"disambiguationData":[TD([[makeQuery(id+"F4.imprint","IMPRINT",EDGE,{"disambiguationData":[TD([[subQ2,1.0]])],"derivedFrom":subQ1}),1.0]])]});}
            var Q19;
            {var subQ0=sQuery(id+"F4.wireOp",EDGE,"E242.trimOffspring");var subQ1=sQuery(id+"F4.wireOp",EDGE,"E130.0");var subQ2=makeQuery(id+"F4.imprint","INTERSECT",VERTEX,{"derivedFrom":[subQ1,subQ0]});Q19=makeQuery(id+"F4.imprint","IMPRINT",FACE,{"disambiguationData":[TD([[makeQuery(id+"F4.imprint","IMPRINT",EDGE,{"disambiguationData":[TD([[subQ2,-1.0]])],"derivedFrom":subQ1}),1.0]])]});}
            var Q20;
            {var subQ0=sQuery(id+"F4.wireOp",EDGE,"E130.0");var subQ1=sQuery(id+"F4.wireOp",EDGE,"E68.0");var subQ2=makeQuery(id+"F4.imprint","INTERSECT",VERTEX,{"derivedFrom":[subQ1,subQ0]});Q20=makeQuery(id+"F4.imprint","IMPRINT",FACE,{"disambiguationData":[TD([[makeQuery(id+"F4.imprint","IMPRINT",EDGE,{"disambiguationData":[TD([[subQ2,1.0]])],"derivedFrom":subQ1}),-1.0]])]});}
            var Q21;
            {var subQ0=sQuery(id+"F4.wireOp",EDGE,"E242.trimOffspring");var subQ1=sQuery(id+"F4.wireOp",EDGE,"E131.0");var subQ2=makeQuery(id+"F4.imprint","INTERSECT",VERTEX,{"derivedFrom":[subQ1,subQ0]});Q21=makeQuery(id+"F4.imprint","IMPRINT",FACE,{"disambiguationData":[TD([[makeQuery(id+"F4.imprint","IMPRINT",EDGE,{"disambiguationData":[TD([[subQ2,-1.0]])],"derivedFrom":subQ1}),1.0]])]});}
            var Q22;
            {var subQ0=sQuery(id+"F4.wireOp",EDGE,"E242.trimOffspring");var subQ1=sQuery(id+"F4.wireOp",EDGE,"E132.0");var subQ2=makeQuery(id+"F4.imprint","INTERSECT",VERTEX,{"derivedFrom":[subQ1,subQ0]});Q22=makeQuery(id+"F4.imprint","IMPRINT",FACE,{"disambiguationData":[TD([[makeQuery(id+"F4.imprint","IMPRINT",EDGE,{"disambiguationData":[TD([[subQ2,-1.0]])],"derivedFrom":subQ1}),1.0]])]});}
            var Q23;
            {var subQ0=sQuery(id+"F4.wireOp",EDGE,"E132.0");var subQ1=sQuery(id+"F4.wireOp",EDGE,"E67.0");var subQ2=makeQuery(id+"F4.imprint","INTERSECT",VERTEX,{"derivedFrom":[subQ1,subQ0]});Q23=makeQuery(id+"F4.imprint","IMPRINT",FACE,{"disambiguationData":[TD([[makeQuery(id+"F4.imprint","IMPRINT",EDGE,{"disambiguationData":[TD([[subQ2,1.0]])],"derivedFrom":subQ1}),1.0]])]});}
            var Q24;
            {var subQ0=sQuery(id+"F4.wireOp",EDGE,"E132.0");var subQ1=sQuery(id+"F4.wireOp",EDGE,"E68.0");var subQ2=makeQuery(id+"F4.imprint","INTERSECT",VERTEX,{"derivedFrom":[subQ1,subQ0]});Q24=makeQuery(id+"F4.imprint","IMPRINT",FACE,{"disambiguationData":[TD([[makeQuery(id+"F4.imprint","IMPRINT",EDGE,{"disambiguationData":[TD([[subQ2,1.0]])],"derivedFrom":subQ1}),-1.0]])]});}
            var Q25;
            {var subQ0=sQuery(id+"F4.wireOp",EDGE,"E134.0");var subQ1=sQuery(id+"F4.wireOp",EDGE,"E67.0");var subQ2=makeQuery(id+"F4.imprint","INTERSECT",VERTEX,{"derivedFrom":[subQ1,subQ0]});Q25=makeQuery(id+"F4.imprint","IMPRINT",FACE,{"disambiguationData":[TD([[makeQuery(id+"F4.imprint","IMPRINT",EDGE,{"disambiguationData":[TD([[subQ2,1.0]])],"derivedFrom":subQ1}),1.0]])]});}
            var Q26;
            {var subQ0=sQuery(id+"F4.wireOp",EDGE,"E244.trimOffspring");var subQ1=sQuery(id+"F4.wireOp",EDGE,"E134.0");var subQ2=makeQuery(id+"F4.imprint","INTERSECT",VERTEX,{"derivedFrom":[subQ1,subQ0]});Q26=makeQuery(id+"F4.imprint","IMPRINT",FACE,{"disambiguationData":[TD([[makeQuery(id+"F4.imprint","IMPRINT",EDGE,{"disambiguationData":[TD([[subQ2,-1.0]])],"derivedFrom":subQ1}),1.0]])]});}
            var Q27;
            {var subQ0=sQuery(id+"F4.wireOp",EDGE,"E134.0");var subQ1=sQuery(id+"F4.wireOp",EDGE,"E68.0");var subQ2=makeQuery(id+"F4.imprint","INTERSECT",VERTEX,{"derivedFrom":[subQ1,subQ0]});Q27=makeQuery(id+"F4.imprint","IMPRINT",FACE,{"disambiguationData":[TD([[makeQuery(id+"F4.imprint","IMPRINT",EDGE,{"disambiguationData":[TD([[subQ2,1.0]])],"derivedFrom":subQ1}),-1.0]])]});}
            var Q28;
            {var subQ0=sQuery(id+"F4.wireOp",EDGE,"E244.trimOffspring");var subQ1=sQuery(id+"F4.wireOp",EDGE,"E135.0");var subQ2=makeQuery(id+"F4.imprint","INTERSECT",VERTEX,{"derivedFrom":[subQ1,subQ0]});Q28=makeQuery(id+"F4.imprint","IMPRINT",FACE,{"disambiguationData":[TD([[makeQuery(id+"F4.imprint","IMPRINT",EDGE,{"disambiguationData":[TD([[subQ2,-1.0]])],"derivedFrom":subQ1}),1.0]])]});}
            var Q29;
            {var subQ0=sQuery(id+"F4.wireOp",EDGE,"E244.trimOffspring");var subQ1=sQuery(id+"F4.wireOp",EDGE,"E136.0");var subQ2=makeQuery(id+"F4.imprint","INTERSECT",VERTEX,{"derivedFrom":[subQ1,subQ0]});Q29=makeQuery(id+"F4.imprint","IMPRINT",FACE,{"disambiguationData":[TD([[makeQuery(id+"F4.imprint","IMPRINT",EDGE,{"disambiguationData":[TD([[subQ2,-1.0]])],"derivedFrom":subQ1}),1.0]])]});}
            var Q30;
            {var subQ0=sQuery(id+"F4.wireOp",EDGE,"E136.0");var subQ1=sQuery(id+"F4.wireOp",EDGE,"E67.0");var subQ2=makeQuery(id+"F4.imprint","INTERSECT",VERTEX,{"derivedFrom":[subQ1,subQ0]});Q30=makeQuery(id+"F4.imprint","IMPRINT",FACE,{"disambiguationData":[TD([[makeQuery(id+"F4.imprint","IMPRINT",EDGE,{"disambiguationData":[TD([[subQ2,1.0]])],"derivedFrom":subQ1}),1.0]])]});}
            var Q31;
            {var subQ0=sQuery(id+"F4.wireOp",EDGE,"E136.0");var subQ1=sQuery(id+"F4.wireOp",EDGE,"E68.0");var subQ2=makeQuery(id+"F4.imprint","INTERSECT",VERTEX,{"derivedFrom":[subQ1,subQ0]});Q31=makeQuery(id+"F4.imprint","IMPRINT",FACE,{"disambiguationData":[TD([[makeQuery(id+"F4.imprint","IMPRINT",EDGE,{"disambiguationData":[TD([[subQ2,1.0]])],"derivedFrom":subQ1}),-1.0]])]});}
            var Q32;
            {var subQ0=sQuery(id+"F4.wireOp",EDGE,"E246.trimOffspring");var subQ1=sQuery(id+"F4.wireOp",EDGE,"E138.0");var subQ2=makeQuery(id+"F4.imprint","INTERSECT",VERTEX,{"derivedFrom":[subQ1,subQ0]});Q32=makeQuery(id+"F4.imprint","IMPRINT",FACE,{"disambiguationData":[TD([[makeQuery(id+"F4.imprint","IMPRINT",EDGE,{"disambiguationData":[TD([[subQ2,-1.0]])],"derivedFrom":subQ1}),1.0]])]});}
            var Q33;
            {var subQ0=sQuery(id+"F4.wireOp",EDGE,"E138.0");var subQ1=sQuery(id+"F4.wireOp",EDGE,"E67.0");var subQ2=makeQuery(id+"F4.imprint","INTERSECT",VERTEX,{"derivedFrom":[subQ1,subQ0]});Q33=makeQuery(id+"F4.imprint","IMPRINT",FACE,{"disambiguationData":[TD([[makeQuery(id+"F4.imprint","IMPRINT",EDGE,{"disambiguationData":[TD([[subQ2,1.0]])],"derivedFrom":subQ1}),1.0]])]});}
            var Q34;
            {var subQ0=sQuery(id+"F4.wireOp",EDGE,"E138.0");var subQ1=sQuery(id+"F4.wireOp",EDGE,"E68.0");var subQ2=makeQuery(id+"F4.imprint","INTERSECT",VERTEX,{"derivedFrom":[subQ1,subQ0]});Q34=makeQuery(id+"F4.imprint","IMPRINT",FACE,{"disambiguationData":[TD([[makeQuery(id+"F4.imprint","IMPRINT",EDGE,{"disambiguationData":[TD([[subQ2,1.0]])],"derivedFrom":subQ1}),-1.0]])]});}
            var Q35;
            {var subQ0=sQuery(id+"F4.wireOp",EDGE,"E246.trimOffspring");var subQ1=sQuery(id+"F4.wireOp",EDGE,"E139.0");var subQ2=makeQuery(id+"F4.imprint","INTERSECT",VERTEX,{"derivedFrom":[subQ1,subQ0]});Q35=makeQuery(id+"F4.imprint","IMPRINT",FACE,{"disambiguationData":[TD([[makeQuery(id+"F4.imprint","IMPRINT",EDGE,{"disambiguationData":[TD([[subQ2,-1.0]])],"derivedFrom":subQ1}),1.0]])]});}
            var Q36;
            {var subQ0=sQuery(id+"F4.wireOp",EDGE,"E246.trimOffspring");var subQ1=sQuery(id+"F4.wireOp",EDGE,"E140.0");var subQ2=makeQuery(id+"F4.imprint","INTERSECT",VERTEX,{"derivedFrom":[subQ1,subQ0]});Q36=makeQuery(id+"F4.imprint","IMPRINT",FACE,{"disambiguationData":[TD([[makeQuery(id+"F4.imprint","IMPRINT",EDGE,{"disambiguationData":[TD([[subQ2,-1.0]])],"derivedFrom":subQ1}),1.0]])]});}
            var Q37;
            {var subQ0=sQuery(id+"F4.wireOp",EDGE,"E140.0");var subQ1=sQuery(id+"F4.wireOp",EDGE,"E67.0");var subQ2=makeQuery(id+"F4.imprint","INTERSECT",VERTEX,{"derivedFrom":[subQ1,subQ0]});Q37=makeQuery(id+"F4.imprint","IMPRINT",FACE,{"disambiguationData":[TD([[makeQuery(id+"F4.imprint","IMPRINT",EDGE,{"disambiguationData":[TD([[subQ2,1.0]])],"derivedFrom":subQ1}),1.0]])]});}
            var Q38;
            {var subQ0=sQuery(id+"F4.wireOp",EDGE,"E140.0");var subQ1=sQuery(id+"F4.wireOp",EDGE,"E68.0");var subQ2=makeQuery(id+"F4.imprint","INTERSECT",VERTEX,{"derivedFrom":[subQ1,subQ0]});Q38=makeQuery(id+"F4.imprint","IMPRINT",FACE,{"disambiguationData":[TD([[makeQuery(id+"F4.imprint","IMPRINT",EDGE,{"disambiguationData":[TD([[subQ2,1.0]])],"derivedFrom":subQ1}),-1.0]])]});}
            var Q39;
            {var subQ0=sQuery(id+"F4.wireOp",EDGE,"E248.trimOffspring");var subQ1=sQuery(id+"F4.wireOp",EDGE,"E142.0");var subQ2=makeQuery(id+"F4.imprint","INTERSECT",VERTEX,{"derivedFrom":[subQ1,subQ0]});Q39=makeQuery(id+"F4.imprint","IMPRINT",FACE,{"disambiguationData":[TD([[makeQuery(id+"F4.imprint","IMPRINT",EDGE,{"disambiguationData":[TD([[subQ2,-1.0]])],"derivedFrom":subQ1}),1.0]])]});}
            var Q40;
            {var subQ0=sQuery(id+"F4.wireOp",EDGE,"E142.0");var subQ1=sQuery(id+"F4.wireOp",EDGE,"E67.0");var subQ2=makeQuery(id+"F4.imprint","INTERSECT",VERTEX,{"derivedFrom":[subQ1,subQ0]});Q40=makeQuery(id+"F4.imprint","IMPRINT",FACE,{"disambiguationData":[TD([[makeQuery(id+"F4.imprint","IMPRINT",EDGE,{"disambiguationData":[TD([[subQ2,1.0]])],"derivedFrom":subQ1}),1.0]])]});}
            var Q41;
            {var subQ0=sQuery(id+"F4.wireOp",EDGE,"E142.0");var subQ1=sQuery(id+"F4.wireOp",EDGE,"E68.0");var subQ2=makeQuery(id+"F4.imprint","INTERSECT",VERTEX,{"derivedFrom":[subQ1,subQ0]});Q41=makeQuery(id+"F4.imprint","IMPRINT",FACE,{"disambiguationData":[TD([[makeQuery(id+"F4.imprint","IMPRINT",EDGE,{"disambiguationData":[TD([[subQ2,1.0]])],"derivedFrom":subQ1}),-1.0]])]});}
            var Q42;
            {var subQ0=sQuery(id+"F4.wireOp",EDGE,"E248.trimOffspring");var subQ1=sQuery(id+"F4.wireOp",EDGE,"E143.0");var subQ2=makeQuery(id+"F4.imprint","INTERSECT",VERTEX,{"derivedFrom":[subQ1,subQ0]});Q42=makeQuery(id+"F4.imprint","IMPRINT",FACE,{"disambiguationData":[TD([[makeQuery(id+"F4.imprint","IMPRINT",EDGE,{"disambiguationData":[TD([[subQ2,-1.0]])],"derivedFrom":subQ1}),1.0]])]});}
            var Q43;
            {var subQ0=sQuery(id+"F4.wireOp",EDGE,"E248.trimOffspring");var subQ1=sQuery(id+"F4.wireOp",EDGE,"E144.0");var subQ2=makeQuery(id+"F4.imprint","INTERSECT",VERTEX,{"derivedFrom":[subQ1,subQ0]});Q43=makeQuery(id+"F4.imprint","IMPRINT",FACE,{"disambiguationData":[TD([[makeQuery(id+"F4.imprint","IMPRINT",EDGE,{"disambiguationData":[TD([[subQ2,-1.0]])],"derivedFrom":subQ1}),1.0]])]});}
            var Q44;
            {var subQ0=sQuery(id+"F4.wireOp",EDGE,"E144.0");var subQ1=sQuery(id+"F4.wireOp",EDGE,"E67.0");var subQ2=makeQuery(id+"F4.imprint","INTERSECT",VERTEX,{"derivedFrom":[subQ1,subQ0]});Q44=makeQuery(id+"F4.imprint","IMPRINT",FACE,{"disambiguationData":[TD([[makeQuery(id+"F4.imprint","IMPRINT",EDGE,{"disambiguationData":[TD([[subQ2,1.0]])],"derivedFrom":subQ1}),1.0]])]});}
            var Q45;
            {var subQ0=sQuery(id+"F4.wireOp",EDGE,"E144.0");var subQ1=sQuery(id+"F4.wireOp",EDGE,"E68.0");var subQ2=makeQuery(id+"F4.imprint","INTERSECT",VERTEX,{"derivedFrom":[subQ1,subQ0]});Q45=makeQuery(id+"F4.imprint","IMPRINT",FACE,{"disambiguationData":[TD([[makeQuery(id+"F4.imprint","IMPRINT",EDGE,{"disambiguationData":[TD([[subQ2,1.0]])],"derivedFrom":subQ1}),-1.0]])]});}
            var Q46;
            {var subQ0=sQuery(id+"F4.wireOp",EDGE,"E146.0");var subQ1=sQuery(id+"F4.wireOp",EDGE,"E67.0");var subQ2=makeQuery(id+"F4.imprint","INTERSECT",VERTEX,{"derivedFrom":[subQ1,subQ0]});Q46=makeQuery(id+"F4.imprint","IMPRINT",FACE,{"disambiguationData":[TD([[makeQuery(id+"F4.imprint","IMPRINT",EDGE,{"disambiguationData":[TD([[subQ2,1.0]])],"derivedFrom":subQ1}),1.0]])]});}
            var Q47;
            {var subQ0=sQuery(id+"F4.wireOp",EDGE,"E250.trimOffspring");var subQ1=sQuery(id+"F4.wireOp",EDGE,"E146.0");var subQ2=makeQuery(id+"F4.imprint","INTERSECT",VERTEX,{"derivedFrom":[subQ1,subQ0]});Q47=makeQuery(id+"F4.imprint","IMPRINT",FACE,{"disambiguationData":[TD([[makeQuery(id+"F4.imprint","IMPRINT",EDGE,{"disambiguationData":[TD([[subQ2,-1.0]])],"derivedFrom":subQ1}),1.0]])]});}
            var Q48;
            {var subQ0=sQuery(id+"F4.wireOp",EDGE,"E146.0");var subQ1=sQuery(id+"F4.wireOp",EDGE,"E68.0");var subQ2=makeQuery(id+"F4.imprint","INTERSECT",VERTEX,{"derivedFrom":[subQ1,subQ0]});Q48=makeQuery(id+"F4.imprint","IMPRINT",FACE,{"disambiguationData":[TD([[makeQuery(id+"F4.imprint","IMPRINT",EDGE,{"disambiguationData":[TD([[subQ2,1.0]])],"derivedFrom":subQ1}),-1.0]])]});}
            var Q49;
            {var subQ0=sQuery(id+"F4.wireOp",EDGE,"E250.trimOffspring");var subQ1=sQuery(id+"F4.wireOp",EDGE,"E66.0");var subQ2=makeQuery(id+"F4.imprint","INTERSECT",VERTEX,{"derivedFrom":[subQ1,subQ0]});Q49=makeQuery(id+"F4.imprint","IMPRINT",FACE,{"disambiguationData":[TD([[makeQuery(id+"F4.imprint","IMPRINT",EDGE,{"disambiguationData":[TD([[subQ2,1.0]])],"derivedFrom":subQ1}),1.0]])]});}
            extrude(context, id + "F6", {"entities" : qUnion([Q0, Q1, Q2, Q3, Q4, Q5, Q6, Q7, Q8, Q9, Q10, Q11, Q12, Q13, Q14, Q15, Q16, Q17, Q18, Q19, Q20, Q21, Q22, Q23, Q24, Q25, Q26, Q27, Q28, Q29, Q30, Q31, Q32, Q33, Q34, Q35, Q36, Q37, Q38, Q39, Q40, Q41, Q42, Q43, Q44, Q45, Q46, Q47, Q48, Q49]), "operationType" : NewBodyOperationType.ADD, "depth" : 28.57 * mm, "offsetDistance" : 25.4 * mm});
        }
        {
            var Q0;
            {var subQ0=sQuery(id+"F4.wireOp",EDGE,"E253.0");var subQ1=sQuery(id+"F4.wireOp",EDGE,"E74.0");var subQ2=makeQuery(id+"F4.imprint","INTERSECT",VERTEX,{"derivedFrom":[subQ1,subQ0]});Q0=makeQuery(id+"F4.imprint","IMPRINT",FACE,{"disambiguationData":[TD([[makeQuery(id+"F4.imprint","IMPRINT",EDGE,{"disambiguationData":[TD([[subQ2,1.0]])],"derivedFrom":subQ1}),1.0]])]});}
            var Q1;
            {var subQ0=sQuery(id+"F4.wireOp",EDGE,"E254.0");var subQ1=sQuery(id+"F4.wireOp",EDGE,"E148.trimOffspring");var subQ2=makeQuery(id+"F4.imprint","INTERSECT",VERTEX,{"derivedFrom":[subQ1,subQ0]});Q1=makeQuery(id+"F4.imprint","IMPRINT",FACE,{"disambiguationData":[TD([[makeQuery(id+"F4.imprint","IMPRINT",EDGE,{"disambiguationData":[TD([[subQ2,-1.0]])],"derivedFrom":subQ1}),1.0]])]});}
            var Q2;
            {var subQ0=sQuery(id+"F4.wireOp",EDGE,"E148.trimOffspring");var subQ1=sQuery(id+"F4.wireOp",EDGE,"E75.0");var subQ2=makeQuery(id+"F4.imprint","INTERSECT",VERTEX,{"derivedFrom":[subQ1,subQ0]});Q2=makeQuery(id+"F4.imprint","IMPRINT",FACE,{"disambiguationData":[TD([[makeQuery(id+"F4.imprint","IMPRINT",EDGE,{"disambiguationData":[TD([[subQ2,1.0]])],"derivedFrom":subQ1}),1.0]])]});}
            var Q3;
            {var subQ0=sQuery(id+"F4.wireOp",EDGE,"E148.trimOffspring");var subQ1=sQuery(id+"F4.wireOp",EDGE,"E76.0");var subQ2=makeQuery(id+"F4.imprint","INTERSECT",VERTEX,{"derivedFrom":[subQ1,subQ0]});Q3=makeQuery(id+"F4.imprint","IMPRINT",FACE,{"disambiguationData":[TD([[makeQuery(id+"F4.imprint","IMPRINT",EDGE,{"disambiguationData":[TD([[subQ2,-1.0]])],"derivedFrom":subQ1}),1.0]])]});}
            var Q4;
            {var subQ0=sQuery(id+"F4.wireOp",EDGE,"E255.trimOffspring");var subQ1=sQuery(id+"F4.wireOp",EDGE,"E150.trimOffspring");var subQ2=makeQuery(id+"F4.imprint","INTERSECT",VERTEX,{"derivedFrom":[subQ1,subQ0]});Q4=makeQuery(id+"F4.imprint","IMPRINT",FACE,{"disambiguationData":[TD([[makeQuery(id+"F4.imprint","IMPRINT",EDGE,{"disambiguationData":[TD([[subQ2,1.0]])],"derivedFrom":subQ1}),1.0]])]});}
            var Q5;
            {var subQ0=sQuery(id+"F4.wireOp",EDGE,"E150.trimOffspring");var subQ1=sQuery(id+"F4.wireOp",EDGE,"E75.0");var subQ2=makeQuery(id+"F4.imprint","INTERSECT",VERTEX,{"derivedFrom":[subQ1,subQ0]});Q5=makeQuery(id+"F4.imprint","IMPRINT",FACE,{"disambiguationData":[TD([[makeQuery(id+"F4.imprint","IMPRINT",EDGE,{"disambiguationData":[TD([[subQ2,1.0]])],"derivedFrom":subQ1}),1.0]])]});}
            var Q6;
            {var subQ0=sQuery(id+"F4.wireOp",EDGE,"E150.trimOffspring");var subQ1=sQuery(id+"F4.wireOp",EDGE,"E76.0");var subQ2=makeQuery(id+"F4.imprint","INTERSECT",VERTEX,{"derivedFrom":[subQ1,subQ0]});Q6=makeQuery(id+"F4.imprint","IMPRINT",FACE,{"disambiguationData":[TD([[makeQuery(id+"F4.imprint","IMPRINT",EDGE,{"disambiguationData":[TD([[subQ2,-1.0]])],"derivedFrom":subQ1}),1.0]])]});}
            var Q7;
            {var subQ0=sQuery(id+"F4.wireOp",EDGE,"E256.trimOffspring");var subQ1=sQuery(id+"F4.wireOp",EDGE,"E151.trimOffspring");var subQ2=makeQuery(id+"F4.imprint","INTERSECT",VERTEX,{"derivedFrom":[subQ1,subQ0]});Q7=makeQuery(id+"F4.imprint","IMPRINT",FACE,{"disambiguationData":[TD([[makeQuery(id+"F4.imprint","IMPRINT",EDGE,{"disambiguationData":[TD([[subQ2,-1.0]])],"derivedFrom":subQ1}),1.0]])]});}
            var Q8;
            {var subQ0=sQuery(id+"F4.wireOp",EDGE,"E152.trimOffspring");var subQ1=sQuery(id+"F4.wireOp",EDGE,"E75.0");var subQ2=makeQuery(id+"F4.imprint","INTERSECT",VERTEX,{"derivedFrom":[subQ1,subQ0]});Q8=makeQuery(id+"F4.imprint","IMPRINT",FACE,{"disambiguationData":[TD([[makeQuery(id+"F4.imprint","IMPRINT",EDGE,{"disambiguationData":[TD([[subQ2,1.0]])],"derivedFrom":subQ1}),1.0]])]});}
            var Q9;
            {var subQ0=sQuery(id+"F4.wireOp",EDGE,"E256.trimOffspring");var subQ1=sQuery(id+"F4.wireOp",EDGE,"E152.trimOffspring");var subQ2=makeQuery(id+"F4.imprint","INTERSECT",VERTEX,{"derivedFrom":[subQ1,subQ0]});Q9=makeQuery(id+"F4.imprint","IMPRINT",FACE,{"disambiguationData":[TD([[makeQuery(id+"F4.imprint","IMPRINT",EDGE,{"disambiguationData":[TD([[subQ2,-1.0]])],"derivedFrom":subQ1}),1.0]])]});}
            var Q10;
            {var subQ0=sQuery(id+"F4.wireOp",EDGE,"E152.trimOffspring");var subQ1=sQuery(id+"F4.wireOp",EDGE,"E76.0");var subQ2=makeQuery(id+"F4.imprint","INTERSECT",VERTEX,{"derivedFrom":[subQ1,subQ0]});Q10=makeQuery(id+"F4.imprint","IMPRINT",FACE,{"disambiguationData":[TD([[makeQuery(id+"F4.imprint","IMPRINT",EDGE,{"disambiguationData":[TD([[subQ2,-1.0]])],"derivedFrom":subQ1}),1.0]])]});}
            var Q11;
            {var subQ0=sQuery(id+"F4.wireOp",EDGE,"E257.trimOffspring");var subQ1=sQuery(id+"F4.wireOp",EDGE,"E154.trimOffspring");var subQ2=makeQuery(id+"F4.imprint","INTERSECT",VERTEX,{"derivedFrom":[subQ1,subQ0]});Q11=makeQuery(id+"F4.imprint","IMPRINT",FACE,{"disambiguationData":[TD([[makeQuery(id+"F4.imprint","IMPRINT",EDGE,{"disambiguationData":[TD([[subQ2,1.0]])],"derivedFrom":subQ1}),1.0]])]});}
            var Q12;
            {var subQ0=sQuery(id+"F4.wireOp",EDGE,"E154.trimOffspring");var subQ1=sQuery(id+"F4.wireOp",EDGE,"E75.0");var subQ2=makeQuery(id+"F4.imprint","INTERSECT",VERTEX,{"derivedFrom":[subQ1,subQ0]});Q12=makeQuery(id+"F4.imprint","IMPRINT",FACE,{"disambiguationData":[TD([[makeQuery(id+"F4.imprint","IMPRINT",EDGE,{"disambiguationData":[TD([[subQ2,1.0]])],"derivedFrom":subQ1}),1.0]])]});}
            var Q13;
            {var subQ0=sQuery(id+"F4.wireOp",EDGE,"E154.trimOffspring");var subQ1=sQuery(id+"F4.wireOp",EDGE,"E76.0");var subQ2=makeQuery(id+"F4.imprint","INTERSECT",VERTEX,{"derivedFrom":[subQ1,subQ0]});Q13=makeQuery(id+"F4.imprint","IMPRINT",FACE,{"disambiguationData":[TD([[makeQuery(id+"F4.imprint","IMPRINT",EDGE,{"disambiguationData":[TD([[subQ2,-1.0]])],"derivedFrom":subQ1}),1.0]])]});}
            var Q14;
            {var subQ0=sQuery(id+"F4.wireOp",EDGE,"E258.trimOffspring");var subQ1=sQuery(id+"F4.wireOp",EDGE,"E155.trimOffspring");var subQ2=makeQuery(id+"F4.imprint","INTERSECT",VERTEX,{"derivedFrom":[subQ1,subQ0]});Q14=makeQuery(id+"F4.imprint","IMPRINT",FACE,{"disambiguationData":[TD([[makeQuery(id+"F4.imprint","IMPRINT",EDGE,{"disambiguationData":[TD([[subQ2,-1.0]])],"derivedFrom":subQ1}),1.0]])]});}
            var Q15;
            {var subQ0=sQuery(id+"F4.wireOp",EDGE,"E258.trimOffspring");var subQ1=sQuery(id+"F4.wireOp",EDGE,"E156.trimOffspring");var subQ2=makeQuery(id+"F4.imprint","INTERSECT",VERTEX,{"derivedFrom":[subQ1,subQ0]});Q15=makeQuery(id+"F4.imprint","IMPRINT",FACE,{"disambiguationData":[TD([[makeQuery(id+"F4.imprint","IMPRINT",EDGE,{"disambiguationData":[TD([[subQ2,-1.0]])],"derivedFrom":subQ1}),1.0]])]});}
            var Q16;
            {var subQ0=sQuery(id+"F4.wireOp",EDGE,"E156.trimOffspring");var subQ1=sQuery(id+"F4.wireOp",EDGE,"E75.0");var subQ2=makeQuery(id+"F4.imprint","INTERSECT",VERTEX,{"derivedFrom":[subQ1,subQ0]});Q16=makeQuery(id+"F4.imprint","IMPRINT",FACE,{"disambiguationData":[TD([[makeQuery(id+"F4.imprint","IMPRINT",EDGE,{"disambiguationData":[TD([[subQ2,1.0]])],"derivedFrom":subQ1}),1.0]])]});}
            var Q17;
            {var subQ0=sQuery(id+"F4.wireOp",EDGE,"E156.trimOffspring");var subQ1=sQuery(id+"F4.wireOp",EDGE,"E76.0");var subQ2=makeQuery(id+"F4.imprint","INTERSECT",VERTEX,{"derivedFrom":[subQ1,subQ0]});Q17=makeQuery(id+"F4.imprint","IMPRINT",FACE,{"disambiguationData":[TD([[makeQuery(id+"F4.imprint","IMPRINT",EDGE,{"disambiguationData":[TD([[subQ2,-1.0]])],"derivedFrom":subQ1}),1.0]])]});}
            var Q18;
            {var subQ0=sQuery(id+"F4.wireOp",EDGE,"E259.trimOffspring");var subQ1=sQuery(id+"F4.wireOp",EDGE,"E158.trimOffspring");var subQ2=makeQuery(id+"F4.imprint","INTERSECT",VERTEX,{"derivedFrom":[subQ1,subQ0]});Q18=makeQuery(id+"F4.imprint","IMPRINT",FACE,{"disambiguationData":[TD([[makeQuery(id+"F4.imprint","IMPRINT",EDGE,{"disambiguationData":[TD([[subQ2,-1.0]])],"derivedFrom":subQ1}),1.0]])]});}
            var Q19;
            {var subQ0=sQuery(id+"F4.wireOp",EDGE,"E259.trimOffspring");var subQ1=sQuery(id+"F4.wireOp",EDGE,"E160.trimOffspring");var subQ2=makeQuery(id+"F4.imprint","INTERSECT",VERTEX,{"derivedFrom":[subQ1,subQ0]});Q19=makeQuery(id+"F4.imprint","IMPRINT",FACE,{"disambiguationData":[TD([[makeQuery(id+"F4.imprint","IMPRINT",EDGE,{"disambiguationData":[TD([[subQ2,-1.0]])],"derivedFrom":subQ1}),-1.0]])]});}
            var Q20;
            {var subQ0=sQuery(id+"F4.wireOp",EDGE,"E160.trimOffspring");var subQ1=sQuery(id+"F4.wireOp",EDGE,"E75.0");var subQ2=makeQuery(id+"F4.imprint","INTERSECT",VERTEX,{"derivedFrom":[subQ1,subQ0]});Q20=makeQuery(id+"F4.imprint","IMPRINT",FACE,{"disambiguationData":[TD([[makeQuery(id+"F4.imprint","IMPRINT",EDGE,{"disambiguationData":[TD([[subQ2,-1.0]])],"derivedFrom":subQ1}),1.0]])]});}
            var Q21;
            {var subQ0=sQuery(id+"F4.wireOp",EDGE,"E160.trimOffspring");var subQ1=sQuery(id+"F4.wireOp",EDGE,"E76.0");var subQ2=makeQuery(id+"F4.imprint","INTERSECT",VERTEX,{"derivedFrom":[subQ1,subQ0]});Q21=makeQuery(id+"F4.imprint","IMPRINT",FACE,{"disambiguationData":[TD([[makeQuery(id+"F4.imprint","IMPRINT",EDGE,{"disambiguationData":[TD([[subQ2,1.0]])],"derivedFrom":subQ1}),1.0]])]});}
            var Q22;
            {var subQ0=sQuery(id+"F4.wireOp",EDGE,"E158.trimOffspring");var subQ1=sQuery(id+"F4.wireOp",EDGE,"E76.0");var subQ2=makeQuery(id+"F4.imprint","INTERSECT",VERTEX,{"derivedFrom":[subQ1,subQ0]});Q22=makeQuery(id+"F4.imprint","IMPRINT",FACE,{"disambiguationData":[TD([[makeQuery(id+"F4.imprint","IMPRINT",EDGE,{"disambiguationData":[TD([[subQ2,1.0]])],"derivedFrom":subQ1}),1.0]])]});}
            var Q23;
            {var subQ0=sQuery(id+"F4.wireOp",EDGE,"E259.trimOffspring");var subQ1=sQuery(id+"F4.wireOp",EDGE,"E158.trimOffspring");var subQ2=makeQuery(id+"F4.imprint","INTERSECT",VERTEX,{"derivedFrom":[subQ1,subQ0]});Q23=makeQuery(id+"F4.imprint","IMPRINT",FACE,{"disambiguationData":[TD([[makeQuery(id+"F4.imprint","IMPRINT",EDGE,{"disambiguationData":[TD([[subQ2,-1.0]])],"derivedFrom":subQ1}),-1.0]])]});}
            var Q24;
            {var subQ0=sQuery(id+"F4.wireOp",EDGE,"E158.trimOffspring");var subQ1=sQuery(id+"F4.wireOp",EDGE,"E75.0");var subQ2=makeQuery(id+"F4.imprint","INTERSECT",VERTEX,{"derivedFrom":[subQ1,subQ0]});Q24=makeQuery(id+"F4.imprint","IMPRINT",FACE,{"disambiguationData":[TD([[makeQuery(id+"F4.imprint","IMPRINT",EDGE,{"disambiguationData":[TD([[subQ2,-1.0]])],"derivedFrom":subQ1}),1.0]])]});}
            var Q25;
            {var subQ0=sQuery(id+"F4.wireOp",EDGE,"E162.trimOffspring");var subQ1=sQuery(id+"F4.wireOp",EDGE,"E75.0");var subQ2=makeQuery(id+"F4.imprint","INTERSECT",VERTEX,{"derivedFrom":[subQ1,subQ0]});Q25=makeQuery(id+"F4.imprint","IMPRINT",FACE,{"disambiguationData":[TD([[makeQuery(id+"F4.imprint","IMPRINT",EDGE,{"disambiguationData":[TD([[subQ2,1.0]])],"derivedFrom":subQ1}),1.0]])]});}
            var Q26;
            {var subQ0=sQuery(id+"F4.wireOp",EDGE,"E162.trimOffspring");var subQ1=sQuery(id+"F4.wireOp",EDGE,"E76.0");var subQ2=makeQuery(id+"F4.imprint","INTERSECT",VERTEX,{"derivedFrom":[subQ1,subQ0]});Q26=makeQuery(id+"F4.imprint","IMPRINT",FACE,{"disambiguationData":[TD([[makeQuery(id+"F4.imprint","IMPRINT",EDGE,{"disambiguationData":[TD([[subQ2,-1.0]])],"derivedFrom":subQ1}),1.0]])]});}
            var Q27;
            {var subQ0=sQuery(id+"F4.wireOp",EDGE,"E261.trimOffspring");var subQ1=sQuery(id+"F4.wireOp",EDGE,"E162.trimOffspring");var subQ2=makeQuery(id+"F4.imprint","INTERSECT",VERTEX,{"derivedFrom":[subQ1,subQ0]});Q27=makeQuery(id+"F4.imprint","IMPRINT",FACE,{"disambiguationData":[TD([[makeQuery(id+"F4.imprint","IMPRINT",EDGE,{"disambiguationData":[TD([[subQ2,1.0]])],"derivedFrom":subQ1}),1.0]])]});}
            var Q28;
            {var subQ0=sQuery(id+"F4.wireOp",EDGE,"E262.trimOffspring");var subQ1=sQuery(id+"F4.wireOp",EDGE,"E163.trimOffspring");var subQ2=makeQuery(id+"F4.imprint","INTERSECT",VERTEX,{"derivedFrom":[subQ1,subQ0]});Q28=makeQuery(id+"F4.imprint","IMPRINT",FACE,{"disambiguationData":[TD([[makeQuery(id+"F4.imprint","IMPRINT",EDGE,{"disambiguationData":[TD([[subQ2,-1.0]])],"derivedFrom":subQ1}),1.0]])]});}
            var Q29;
            {var subQ0=sQuery(id+"F4.wireOp",EDGE,"E262.trimOffspring");var subQ1=sQuery(id+"F4.wireOp",EDGE,"E164.trimOffspring");var subQ2=makeQuery(id+"F4.imprint","INTERSECT",VERTEX,{"derivedFrom":[subQ1,subQ0]});Q29=makeQuery(id+"F4.imprint","IMPRINT",FACE,{"disambiguationData":[TD([[makeQuery(id+"F4.imprint","IMPRINT",EDGE,{"disambiguationData":[TD([[subQ2,-1.0]])],"derivedFrom":subQ1}),1.0]])]});}
            var Q30;
            {var subQ0=sQuery(id+"F4.wireOp",EDGE,"E164.trimOffspring");var subQ1=sQuery(id+"F4.wireOp",EDGE,"E75.0");var subQ2=makeQuery(id+"F4.imprint","INTERSECT",VERTEX,{"derivedFrom":[subQ1,subQ0]});Q30=makeQuery(id+"F4.imprint","IMPRINT",FACE,{"disambiguationData":[TD([[makeQuery(id+"F4.imprint","IMPRINT",EDGE,{"disambiguationData":[TD([[subQ2,1.0]])],"derivedFrom":subQ1}),1.0]])]});}
            var Q31;
            {var subQ0=sQuery(id+"F4.wireOp",EDGE,"E164.trimOffspring");var subQ1=sQuery(id+"F4.wireOp",EDGE,"E76.0");var subQ2=makeQuery(id+"F4.imprint","INTERSECT",VERTEX,{"derivedFrom":[subQ1,subQ0]});Q31=makeQuery(id+"F4.imprint","IMPRINT",FACE,{"disambiguationData":[TD([[makeQuery(id+"F4.imprint","IMPRINT",EDGE,{"disambiguationData":[TD([[subQ2,-1.0]])],"derivedFrom":subQ1}),1.0]])]});}
            var Q32;
            {var subQ0=sQuery(id+"F4.wireOp",EDGE,"E263.trimOffspring");var subQ1=sQuery(id+"F4.wireOp",EDGE,"E166.trimOffspring");var subQ2=makeQuery(id+"F4.imprint","INTERSECT",VERTEX,{"derivedFrom":[subQ1,subQ0]});Q32=makeQuery(id+"F4.imprint","IMPRINT",FACE,{"disambiguationData":[TD([[makeQuery(id+"F4.imprint","IMPRINT",EDGE,{"disambiguationData":[TD([[subQ2,-1.0]])],"derivedFrom":subQ1}),1.0]])]});}
            var Q33;
            {var subQ0=sQuery(id+"F4.wireOp",EDGE,"E166.trimOffspring");var subQ1=sQuery(id+"F4.wireOp",EDGE,"E75.0");var subQ2=makeQuery(id+"F4.imprint","INTERSECT",VERTEX,{"derivedFrom":[subQ1,subQ0]});Q33=makeQuery(id+"F4.imprint","IMPRINT",FACE,{"disambiguationData":[TD([[makeQuery(id+"F4.imprint","IMPRINT",EDGE,{"disambiguationData":[TD([[subQ2,1.0]])],"derivedFrom":subQ1}),1.0]])]});}
            var Q34;
            {var subQ0=sQuery(id+"F4.wireOp",EDGE,"E263.trimOffspring");var subQ1=sQuery(id+"F4.wireOp",EDGE,"E167.trimOffspring");var subQ2=makeQuery(id+"F4.imprint","INTERSECT",VERTEX,{"derivedFrom":[subQ1,subQ0]});Q34=makeQuery(id+"F4.imprint","IMPRINT",FACE,{"disambiguationData":[TD([[makeQuery(id+"F4.imprint","IMPRINT",EDGE,{"disambiguationData":[TD([[subQ2,-1.0]])],"derivedFrom":subQ1}),1.0]])]});}
            var Q35;
            {var subQ0=sQuery(id+"F4.wireOp",EDGE,"E166.trimOffspring");var subQ1=sQuery(id+"F4.wireOp",EDGE,"E76.0");var subQ2=makeQuery(id+"F4.imprint","INTERSECT",VERTEX,{"derivedFrom":[subQ1,subQ0]});Q35=makeQuery(id+"F4.imprint","IMPRINT",FACE,{"disambiguationData":[TD([[makeQuery(id+"F4.imprint","IMPRINT",EDGE,{"disambiguationData":[TD([[subQ2,-1.0]])],"derivedFrom":subQ1}),1.0]])]});}
            var Q36;
            {var subQ0=sQuery(id+"F4.wireOp",EDGE,"E263.trimOffspring");var subQ1=sQuery(id+"F4.wireOp",EDGE,"E168.trimOffspring");var subQ2=makeQuery(id+"F4.imprint","INTERSECT",VERTEX,{"derivedFrom":[subQ1,subQ0]});Q36=makeQuery(id+"F4.imprint","IMPRINT",FACE,{"disambiguationData":[TD([[makeQuery(id+"F4.imprint","IMPRINT",EDGE,{"disambiguationData":[TD([[subQ2,-1.0]])],"derivedFrom":subQ1}),1.0]])]});}
            var Q37;
            {var subQ0=sQuery(id+"F4.wireOp",EDGE,"E168.trimOffspring");var subQ1=sQuery(id+"F4.wireOp",EDGE,"E76.0");var subQ2=makeQuery(id+"F4.imprint","INTERSECT",VERTEX,{"derivedFrom":[subQ1,subQ0]});Q37=makeQuery(id+"F4.imprint","IMPRINT",FACE,{"disambiguationData":[TD([[makeQuery(id+"F4.imprint","IMPRINT",EDGE,{"disambiguationData":[TD([[subQ2,-1.0]])],"derivedFrom":subQ1}),1.0]])]});}
            var Q38;
            {var subQ0=sQuery(id+"F4.wireOp",EDGE,"E168.trimOffspring");var subQ1=sQuery(id+"F4.wireOp",EDGE,"E75.0");var subQ2=makeQuery(id+"F4.imprint","INTERSECT",VERTEX,{"derivedFrom":[subQ1,subQ0]});Q38=makeQuery(id+"F4.imprint","IMPRINT",FACE,{"disambiguationData":[TD([[makeQuery(id+"F4.imprint","IMPRINT",EDGE,{"disambiguationData":[TD([[subQ2,1.0]])],"derivedFrom":subQ1}),1.0]])]});}
            var Q39;
            {var subQ0=sQuery(id+"F4.wireOp",EDGE,"E170.trimOffspring");var subQ1=sQuery(id+"F4.wireOp",EDGE,"E75.0");var subQ2=makeQuery(id+"F4.imprint","INTERSECT",VERTEX,{"derivedFrom":[subQ1,subQ0]});Q39=makeQuery(id+"F4.imprint","IMPRINT",FACE,{"disambiguationData":[TD([[makeQuery(id+"F4.imprint","IMPRINT",EDGE,{"disambiguationData":[TD([[subQ2,1.0]])],"derivedFrom":subQ1}),1.0]])]});}
            var Q40;
            {var subQ0=sQuery(id+"F4.wireOp",EDGE,"E170.trimOffspring");var subQ1=sQuery(id+"F4.wireOp",EDGE,"E76.0");var subQ2=makeQuery(id+"F4.imprint","INTERSECT",VERTEX,{"derivedFrom":[subQ1,subQ0]});Q40=makeQuery(id+"F4.imprint","IMPRINT",FACE,{"disambiguationData":[TD([[makeQuery(id+"F4.imprint","IMPRINT",EDGE,{"disambiguationData":[TD([[subQ2,-1.0]])],"derivedFrom":subQ1}),1.0]])]});}
            var Q41;
            {var subQ0=sQuery(id+"F4.wireOp",EDGE,"E265.trimOffspring");var subQ1=sQuery(id+"F4.wireOp",EDGE,"E172.trimOffspring");var subQ2=makeQuery(id+"F4.imprint","INTERSECT",VERTEX,{"derivedFrom":[subQ1,subQ0]});Q41=makeQuery(id+"F4.imprint","IMPRINT",FACE,{"disambiguationData":[TD([[makeQuery(id+"F4.imprint","IMPRINT",EDGE,{"disambiguationData":[TD([[subQ2,-1.0]])],"derivedFrom":subQ1}),1.0]])]});}
            var Q42;
            {var subQ0=sQuery(id+"F4.wireOp",EDGE,"E173.trimOffspring");var subQ1=sQuery(id+"F4.wireOp",EDGE,"E75.0");var subQ2=makeQuery(id+"F4.imprint","INTERSECT",VERTEX,{"derivedFrom":[subQ1,subQ0]});Q42=makeQuery(id+"F4.imprint","IMPRINT",FACE,{"disambiguationData":[TD([[makeQuery(id+"F4.imprint","IMPRINT",EDGE,{"disambiguationData":[TD([[subQ2,-1.0]])],"derivedFrom":subQ1}),1.0]])]});}
            var Q43;
            {var subQ0=sQuery(id+"F4.wireOp",EDGE,"E172.trimOffspring");var subQ1=sQuery(id+"F4.wireOp",EDGE,"E76.0");var subQ2=makeQuery(id+"F4.imprint","INTERSECT",VERTEX,{"derivedFrom":[subQ1,subQ0]});Q43=makeQuery(id+"F4.imprint","IMPRINT",FACE,{"disambiguationData":[TD([[makeQuery(id+"F4.imprint","IMPRINT",EDGE,{"disambiguationData":[TD([[subQ2,-1.0]])],"derivedFrom":subQ1}),1.0]])]});}
            var Q44;
            {var subQ0=sQuery(id+"F4.wireOp",EDGE,"E265.trimOffspring");var subQ1=sQuery(id+"F4.wireOp",EDGE,"E171.trimOffspring");var subQ2=makeQuery(id+"F4.imprint","INTERSECT",VERTEX,{"derivedFrom":[subQ1,subQ0]});Q44=makeQuery(id+"F4.imprint","IMPRINT",FACE,{"disambiguationData":[TD([[makeQuery(id+"F4.imprint","IMPRINT",EDGE,{"disambiguationData":[TD([[subQ2,-1.0]])],"derivedFrom":subQ1}),1.0]])]});}
            var Q45;
            {var subQ0=sQuery(id+"F4.wireOp",EDGE,"E265.trimOffspring");var subQ1=sQuery(id+"F4.wireOp",EDGE,"E170.trimOffspring");var subQ2=makeQuery(id+"F4.imprint","INTERSECT",VERTEX,{"derivedFrom":[subQ1,subQ0]});Q45=makeQuery(id+"F4.imprint","IMPRINT",FACE,{"disambiguationData":[TD([[makeQuery(id+"F4.imprint","IMPRINT",EDGE,{"disambiguationData":[TD([[subQ2,-1.0]])],"derivedFrom":subQ1}),1.0]])]});}
            var Q46;
            {var subQ0=sQuery(id+"F4.wireOp",EDGE,"E267.trimOffspring");var subQ1=sQuery(id+"F4.wireOp",EDGE,"E119.trimOffspring");var subQ2=makeQuery(id+"F4.imprint","INTERSECT",VERTEX,{"derivedFrom":[subQ1,subQ0]});Q46=makeQuery(id+"F4.imprint","IMPRINT",FACE,{"disambiguationData":[TD([[makeQuery(id+"F4.imprint","IMPRINT",EDGE,{"disambiguationData":[TD([[subQ2,-1.0]])],"derivedFrom":subQ1}),-1.0]])]});}
            var Q47;
            {var subQ0=sQuery(id+"F4.wireOp",EDGE,"E119.trimOffspring");var subQ1=sQuery(id+"F4.wireOp",EDGE,"E75.0");var subQ2=makeQuery(id+"F4.imprint","INTERSECT",VERTEX,{"derivedFrom":[subQ1,subQ0]});Q47=makeQuery(id+"F4.imprint","IMPRINT",FACE,{"disambiguationData":[TD([[makeQuery(id+"F4.imprint","IMPRINT",EDGE,{"disambiguationData":[TD([[subQ2,-1.0]])],"derivedFrom":subQ1}),1.0]])]});}
            var Q48;
            {var subQ0=sQuery(id+"F4.wireOp",EDGE,"E119.trimOffspring");var subQ1=sQuery(id+"F4.wireOp",EDGE,"E76.0");var subQ2=makeQuery(id+"F4.imprint","INTERSECT",VERTEX,{"derivedFrom":[subQ1,subQ0]});Q48=makeQuery(id+"F4.imprint","IMPRINT",FACE,{"disambiguationData":[TD([[makeQuery(id+"F4.imprint","IMPRINT",EDGE,{"disambiguationData":[TD([[subQ2,1.0]])],"derivedFrom":subQ1}),1.0]])]});}
            var Q49;
            {var subQ0=sQuery(id+"F4.wireOp",EDGE,"E267.trimOffspring");var subQ1=sQuery(id+"F4.wireOp",EDGE,"E119.trimOffspring");var subQ2=makeQuery(id+"F4.imprint","INTERSECT",VERTEX,{"derivedFrom":[subQ1,subQ0]});Q49=makeQuery(id+"F4.imprint","IMPRINT",FACE,{"disambiguationData":[TD([[makeQuery(id+"F4.imprint","IMPRINT",EDGE,{"disambiguationData":[TD([[subQ2,-1.0]])],"derivedFrom":subQ1}),1.0]])]});}
            var Q50;
            {var subQ0=sQuery(id+"F4.wireOp",EDGE,"E267.trimOffspring");var subQ1=sQuery(id+"F4.wireOp",EDGE,"E174.trimOffspring");var subQ2=makeQuery(id+"F4.imprint","INTERSECT",VERTEX,{"derivedFrom":[subQ1,subQ0]});Q50=makeQuery(id+"F4.imprint","IMPRINT",FACE,{"disambiguationData":[TD([[makeQuery(id+"F4.imprint","IMPRINT",EDGE,{"disambiguationData":[TD([[subQ2,-1.0]])],"derivedFrom":subQ1}),1.0]])]});}
            var Q51;
            {var subQ0=sQuery(id+"F4.wireOp",EDGE,"E175.trimOffspring");var subQ1=sQuery(id+"F4.wireOp",EDGE,"E75.0");var subQ2=makeQuery(id+"F4.imprint","INTERSECT",VERTEX,{"derivedFrom":[subQ1,subQ0]});Q51=makeQuery(id+"F4.imprint","IMPRINT",FACE,{"disambiguationData":[TD([[makeQuery(id+"F4.imprint","IMPRINT",EDGE,{"disambiguationData":[TD([[subQ2,-1.0]])],"derivedFrom":subQ1}),1.0]])]});}
            var Q52;
            {var subQ0=sQuery(id+"F4.wireOp",EDGE,"E174.trimOffspring");var subQ1=sQuery(id+"F4.wireOp",EDGE,"E76.0");var subQ2=makeQuery(id+"F4.imprint","INTERSECT",VERTEX,{"derivedFrom":[subQ1,subQ0]});Q52=makeQuery(id+"F4.imprint","IMPRINT",FACE,{"disambiguationData":[TD([[makeQuery(id+"F4.imprint","IMPRINT",EDGE,{"disambiguationData":[TD([[subQ2,-1.0]])],"derivedFrom":subQ1}),1.0]])]});}
            var Q53;
            {var subQ0=sQuery(id+"F4.wireOp",EDGE,"E269.trimOffspring");var subQ1=sQuery(id+"F4.wireOp",EDGE,"E176.trimOffspring");var subQ2=makeQuery(id+"F4.imprint","INTERSECT",VERTEX,{"derivedFrom":[subQ1,subQ0]});Q53=makeQuery(id+"F4.imprint","IMPRINT",FACE,{"disambiguationData":[TD([[makeQuery(id+"F4.imprint","IMPRINT",EDGE,{"disambiguationData":[TD([[subQ2,1.0]])],"derivedFrom":subQ1}),1.0]])]});}
            var Q54;
            {var subQ0=sQuery(id+"F4.wireOp",EDGE,"E176.trimOffspring");var subQ1=sQuery(id+"F4.wireOp",EDGE,"E76.0");var subQ2=makeQuery(id+"F4.imprint","INTERSECT",VERTEX,{"derivedFrom":[subQ1,subQ0]});Q54=makeQuery(id+"F4.imprint","IMPRINT",FACE,{"disambiguationData":[TD([[makeQuery(id+"F4.imprint","IMPRINT",EDGE,{"disambiguationData":[TD([[subQ2,-1.0]])],"derivedFrom":subQ1}),1.0]])]});}
            var Q55;
            {var subQ0=sQuery(id+"F4.wireOp",EDGE,"E270.trimOffspring");var subQ1=sQuery(id+"F4.wireOp",EDGE,"E177.trimOffspring");var subQ2=makeQuery(id+"F4.imprint","INTERSECT",VERTEX,{"derivedFrom":[subQ1,subQ0]});Q55=makeQuery(id+"F4.imprint","IMPRINT",FACE,{"disambiguationData":[TD([[makeQuery(id+"F4.imprint","IMPRINT",EDGE,{"disambiguationData":[TD([[subQ2,-1.0]])],"derivedFrom":subQ1}),1.0]])]});}
            var Q56;
            {var subQ0=sQuery(id+"F4.wireOp",EDGE,"E270.trimOffspring");var subQ1=sQuery(id+"F4.wireOp",EDGE,"E178.trimOffspring");var subQ2=makeQuery(id+"F4.imprint","INTERSECT",VERTEX,{"derivedFrom":[subQ1,subQ0]});Q56=makeQuery(id+"F4.imprint","IMPRINT",FACE,{"disambiguationData":[TD([[makeQuery(id+"F4.imprint","IMPRINT",EDGE,{"disambiguationData":[TD([[subQ2,-1.0]])],"derivedFrom":subQ1}),1.0]])]});}
            var Q57;
            {var subQ0=sQuery(id+"F4.wireOp",EDGE,"E179.trimOffspring");var subQ1=sQuery(id+"F4.wireOp",EDGE,"E75.0");var subQ2=makeQuery(id+"F4.imprint","INTERSECT",VERTEX,{"derivedFrom":[subQ1,subQ0]});Q57=makeQuery(id+"F4.imprint","IMPRINT",FACE,{"disambiguationData":[TD([[makeQuery(id+"F4.imprint","IMPRINT",EDGE,{"disambiguationData":[TD([[subQ2,-1.0]])],"derivedFrom":subQ1}),1.0]])]});}
            var Q58;
            {var subQ0=sQuery(id+"F4.wireOp",EDGE,"E178.trimOffspring");var subQ1=sQuery(id+"F4.wireOp",EDGE,"E76.0");var subQ2=makeQuery(id+"F4.imprint","INTERSECT",VERTEX,{"derivedFrom":[subQ1,subQ0]});Q58=makeQuery(id+"F4.imprint","IMPRINT",FACE,{"disambiguationData":[TD([[makeQuery(id+"F4.imprint","IMPRINT",EDGE,{"disambiguationData":[TD([[subQ2,-1.0]])],"derivedFrom":subQ1}),1.0]])]});}
            var Q59;
            {var subQ0=sQuery(id+"F4.wireOp",EDGE,"E177.trimOffspring");var subQ1=sQuery(id+"F4.wireOp",EDGE,"E75.0");var subQ2=makeQuery(id+"F4.imprint","INTERSECT",VERTEX,{"derivedFrom":[subQ1,subQ0]});Q59=makeQuery(id+"F4.imprint","IMPRINT",FACE,{"disambiguationData":[TD([[makeQuery(id+"F4.imprint","IMPRINT",EDGE,{"disambiguationData":[TD([[subQ2,-1.0]])],"derivedFrom":subQ1}),1.0]])]});}
            var Q60;
            {var subQ0=sQuery(id+"F4.wireOp",EDGE,"E181.trimOffspring");var subQ1=sQuery(id+"F4.wireOp",EDGE,"E75.0");var subQ2=makeQuery(id+"F4.imprint","INTERSECT",VERTEX,{"derivedFrom":[subQ1,subQ0]});Q60=makeQuery(id+"F4.imprint","IMPRINT",FACE,{"disambiguationData":[TD([[makeQuery(id+"F4.imprint","IMPRINT",EDGE,{"disambiguationData":[TD([[subQ2,-1.0]])],"derivedFrom":subQ1}),1.0]])]});}
            var Q61;
            {var subQ0=sQuery(id+"F4.wireOp",EDGE,"E180.trimOffspring");var subQ1=sQuery(id+"F4.wireOp",EDGE,"E76.0");var subQ2=makeQuery(id+"F4.imprint","INTERSECT",VERTEX,{"derivedFrom":[subQ1,subQ0]});Q61=makeQuery(id+"F4.imprint","IMPRINT",FACE,{"disambiguationData":[TD([[makeQuery(id+"F4.imprint","IMPRINT",EDGE,{"disambiguationData":[TD([[subQ2,-1.0]])],"derivedFrom":subQ1}),1.0]])]});}
            var Q62;
            {var subQ0=sQuery(id+"F4.wireOp",EDGE,"E271.trimOffspring");var subQ1=sQuery(id+"F4.wireOp",EDGE,"E181.trimOffspring");var subQ2=makeQuery(id+"F4.imprint","INTERSECT",VERTEX,{"derivedFrom":[subQ1,subQ0]});Q62=makeQuery(id+"F4.imprint","IMPRINT",FACE,{"disambiguationData":[TD([[makeQuery(id+"F4.imprint","IMPRINT",EDGE,{"disambiguationData":[TD([[subQ2,-1.0]])],"derivedFrom":subQ1}),1.0]])]});}
            var Q63;
            {var subQ0=sQuery(id+"F4.wireOp",EDGE,"E271.trimOffspring");var subQ1=sQuery(id+"F4.wireOp",EDGE,"E180.trimOffspring");var subQ2=makeQuery(id+"F4.imprint","INTERSECT",VERTEX,{"derivedFrom":[subQ1,subQ0]});Q63=makeQuery(id+"F4.imprint","IMPRINT",FACE,{"disambiguationData":[TD([[makeQuery(id+"F4.imprint","IMPRINT",EDGE,{"disambiguationData":[TD([[subQ2,-1.0]])],"derivedFrom":subQ1}),1.0]])]});}
            var Q64;
            {var subQ0=sQuery(id+"F4.wireOp",EDGE,"E182.trimOffspring");var subQ1=sQuery(id+"F4.wireOp",EDGE,"E76.0");var subQ2=makeQuery(id+"F4.imprint","INTERSECT",VERTEX,{"derivedFrom":[subQ1,subQ0]});Q64=makeQuery(id+"F4.imprint","IMPRINT",FACE,{"disambiguationData":[TD([[makeQuery(id+"F4.imprint","IMPRINT",EDGE,{"disambiguationData":[TD([[subQ2,-1.0]])],"derivedFrom":subQ1}),1.0]])]});}
            var Q65;
            {var subQ0=sQuery(id+"F4.wireOp",EDGE,"E183.trimOffspring");var subQ1=sQuery(id+"F4.wireOp",EDGE,"E75.0");var subQ2=makeQuery(id+"F4.imprint","INTERSECT",VERTEX,{"derivedFrom":[subQ1,subQ0]});Q65=makeQuery(id+"F4.imprint","IMPRINT",FACE,{"disambiguationData":[TD([[makeQuery(id+"F4.imprint","IMPRINT",EDGE,{"disambiguationData":[TD([[subQ2,-1.0]])],"derivedFrom":subQ1}),1.0]])]});}
            var Q66;
            {var subQ0=sQuery(id+"F4.wireOp",EDGE,"E271.trimOffspring");var subQ1=sQuery(id+"F4.wireOp",EDGE,"E182.trimOffspring");var subQ2=makeQuery(id+"F4.imprint","INTERSECT",VERTEX,{"derivedFrom":[subQ1,subQ0]});Q66=makeQuery(id+"F4.imprint","IMPRINT",FACE,{"disambiguationData":[TD([[makeQuery(id+"F4.imprint","IMPRINT",EDGE,{"disambiguationData":[TD([[subQ2,-1.0]])],"derivedFrom":subQ1}),1.0]])]});}
            var Q67;
            {var subQ0=sQuery(id+"F4.wireOp",EDGE,"E273.trimOffspring");var subQ1=sQuery(id+"F4.wireOp",EDGE,"E184.trimOffspring");var subQ2=makeQuery(id+"F4.imprint","INTERSECT",VERTEX,{"derivedFrom":[subQ1,subQ0]});Q67=makeQuery(id+"F4.imprint","IMPRINT",FACE,{"disambiguationData":[TD([[makeQuery(id+"F4.imprint","IMPRINT",EDGE,{"disambiguationData":[TD([[subQ2,-1.0]])],"derivedFrom":subQ1}),1.0]])]});}
            var Q68;
            {var subQ0=sQuery(id+"F4.wireOp",EDGE,"E185.trimOffspring");var subQ1=sQuery(id+"F4.wireOp",EDGE,"E75.0");var subQ2=makeQuery(id+"F4.imprint","INTERSECT",VERTEX,{"derivedFrom":[subQ1,subQ0]});Q68=makeQuery(id+"F4.imprint","IMPRINT",FACE,{"disambiguationData":[TD([[makeQuery(id+"F4.imprint","IMPRINT",EDGE,{"disambiguationData":[TD([[subQ2,-1.0]])],"derivedFrom":subQ1}),1.0]])]});}
            var Q69;
            {var subQ0=sQuery(id+"F4.wireOp",EDGE,"E184.trimOffspring");var subQ1=sQuery(id+"F4.wireOp",EDGE,"E76.0");var subQ2=makeQuery(id+"F4.imprint","INTERSECT",VERTEX,{"derivedFrom":[subQ1,subQ0]});Q69=makeQuery(id+"F4.imprint","IMPRINT",FACE,{"disambiguationData":[TD([[makeQuery(id+"F4.imprint","IMPRINT",EDGE,{"disambiguationData":[TD([[subQ2,-1.0]])],"derivedFrom":subQ1}),1.0]])]});}
            var Q70;
            {var subQ0=sQuery(id+"F4.wireOp",EDGE,"E273.trimOffspring");var subQ1=sQuery(id+"F4.wireOp",EDGE,"E185.trimOffspring");var subQ2=makeQuery(id+"F4.imprint","INTERSECT",VERTEX,{"derivedFrom":[subQ1,subQ0]});Q70=makeQuery(id+"F4.imprint","IMPRINT",FACE,{"disambiguationData":[TD([[makeQuery(id+"F4.imprint","IMPRINT",EDGE,{"disambiguationData":[TD([[subQ2,-1.0]])],"derivedFrom":subQ1}),1.0]])]});}
            var Q71;
            {var subQ0=sQuery(id+"F4.wireOp",EDGE,"E273.trimOffspring");var subQ1=sQuery(id+"F4.wireOp",EDGE,"E186.trimOffspring");var subQ2=makeQuery(id+"F4.imprint","INTERSECT",VERTEX,{"derivedFrom":[subQ1,subQ0]});Q71=makeQuery(id+"F4.imprint","IMPRINT",FACE,{"disambiguationData":[TD([[makeQuery(id+"F4.imprint","IMPRINT",EDGE,{"disambiguationData":[TD([[subQ2,-1.0]])],"derivedFrom":subQ1}),1.0]])]});}
            var Q72;
            {var subQ0=sQuery(id+"F4.wireOp",EDGE,"E187.trimOffspring");var subQ1=sQuery(id+"F4.wireOp",EDGE,"E75.0");var subQ2=makeQuery(id+"F4.imprint","INTERSECT",VERTEX,{"derivedFrom":[subQ1,subQ0]});Q72=makeQuery(id+"F4.imprint","IMPRINT",FACE,{"disambiguationData":[TD([[makeQuery(id+"F4.imprint","IMPRINT",EDGE,{"disambiguationData":[TD([[subQ2,-1.0]])],"derivedFrom":subQ1}),1.0]])]});}
            var Q73;
            {var subQ0=sQuery(id+"F4.wireOp",EDGE,"E186.trimOffspring");var subQ1=sQuery(id+"F4.wireOp",EDGE,"E76.0");var subQ2=makeQuery(id+"F4.imprint","INTERSECT",VERTEX,{"derivedFrom":[subQ1,subQ0]});Q73=makeQuery(id+"F4.imprint","IMPRINT",FACE,{"disambiguationData":[TD([[makeQuery(id+"F4.imprint","IMPRINT",EDGE,{"disambiguationData":[TD([[subQ2,-1.0]])],"derivedFrom":subQ1}),1.0]])]});}
            var Q74;
            {var subQ0=sQuery(id+"F4.wireOp",EDGE,"E275.trimOffspring");var subQ1=sQuery(id+"F4.wireOp",EDGE,"E188.trimOffspring");var subQ2=makeQuery(id+"F4.imprint","INTERSECT",VERTEX,{"derivedFrom":[subQ1,subQ0]});Q74=makeQuery(id+"F4.imprint","IMPRINT",FACE,{"disambiguationData":[TD([[makeQuery(id+"F4.imprint","IMPRINT",EDGE,{"disambiguationData":[TD([[subQ2,-1.0]])],"derivedFrom":subQ1}),1.0]])]});}
            var Q75;
            {var subQ0=sQuery(id+"F4.wireOp",EDGE,"E189.trimOffspring");var subQ1=sQuery(id+"F4.wireOp",EDGE,"E75.0");var subQ2=makeQuery(id+"F4.imprint","INTERSECT",VERTEX,{"derivedFrom":[subQ1,subQ0]});Q75=makeQuery(id+"F4.imprint","IMPRINT",FACE,{"disambiguationData":[TD([[makeQuery(id+"F4.imprint","IMPRINT",EDGE,{"disambiguationData":[TD([[subQ2,-1.0]])],"derivedFrom":subQ1}),1.0]])]});}
            var Q76;
            {var subQ0=sQuery(id+"F4.wireOp",EDGE,"E188.trimOffspring");var subQ1=sQuery(id+"F4.wireOp",EDGE,"E76.0");var subQ2=makeQuery(id+"F4.imprint","INTERSECT",VERTEX,{"derivedFrom":[subQ1,subQ0]});Q76=makeQuery(id+"F4.imprint","IMPRINT",FACE,{"disambiguationData":[TD([[makeQuery(id+"F4.imprint","IMPRINT",EDGE,{"disambiguationData":[TD([[subQ2,-1.0]])],"derivedFrom":subQ1}),1.0]])]});}
            var Q77;
            {var subQ0=sQuery(id+"F4.wireOp",EDGE,"E275.trimOffspring");var subQ1=sQuery(id+"F4.wireOp",EDGE,"E189.trimOffspring");var subQ2=makeQuery(id+"F4.imprint","INTERSECT",VERTEX,{"derivedFrom":[subQ1,subQ0]});Q77=makeQuery(id+"F4.imprint","IMPRINT",FACE,{"disambiguationData":[TD([[makeQuery(id+"F4.imprint","IMPRINT",EDGE,{"disambiguationData":[TD([[subQ2,-1.0]])],"derivedFrom":subQ1}),1.0]])]});}
            var Q78;
            {var subQ0=sQuery(id+"F4.wireOp",EDGE,"E275.trimOffspring");var subQ1=sQuery(id+"F4.wireOp",EDGE,"E190.trimOffspring");var subQ2=makeQuery(id+"F4.imprint","INTERSECT",VERTEX,{"derivedFrom":[subQ1,subQ0]});Q78=makeQuery(id+"F4.imprint","IMPRINT",FACE,{"disambiguationData":[TD([[makeQuery(id+"F4.imprint","IMPRINT",EDGE,{"disambiguationData":[TD([[subQ2,-1.0]])],"derivedFrom":subQ1}),-1.0]])]});}
            var Q79;
            {var subQ0=sQuery(id+"F4.wireOp",EDGE,"E190.trimOffspring");var subQ1=sQuery(id+"F4.wireOp",EDGE,"E75.0");var subQ2=makeQuery(id+"F4.imprint","INTERSECT",VERTEX,{"derivedFrom":[subQ1,subQ0]});Q79=makeQuery(id+"F4.imprint","IMPRINT",FACE,{"disambiguationData":[TD([[makeQuery(id+"F4.imprint","IMPRINT",EDGE,{"disambiguationData":[TD([[subQ2,-1.0]])],"derivedFrom":subQ1}),1.0]])]});}
            var Q80;
            {var subQ0=sQuery(id+"F4.wireOp",EDGE,"E190.trimOffspring");var subQ1=sQuery(id+"F4.wireOp",EDGE,"E76.0");var subQ2=makeQuery(id+"F4.imprint","INTERSECT",VERTEX,{"derivedFrom":[subQ1,subQ0]});Q80=makeQuery(id+"F4.imprint","IMPRINT",FACE,{"disambiguationData":[TD([[makeQuery(id+"F4.imprint","IMPRINT",EDGE,{"disambiguationData":[TD([[subQ2,1.0]])],"derivedFrom":subQ1}),1.0]])]});}
            var Q81;
            {var subQ0=sQuery(id+"F4.wireOp",EDGE,"E277.trimOffspring");var subQ1=sQuery(id+"F4.wireOp",EDGE,"E192.trimOffspring");var subQ2=makeQuery(id+"F4.imprint","INTERSECT",VERTEX,{"derivedFrom":[subQ1,subQ0]});Q81=makeQuery(id+"F4.imprint","IMPRINT",FACE,{"disambiguationData":[TD([[makeQuery(id+"F4.imprint","IMPRINT",EDGE,{"disambiguationData":[TD([[subQ2,-1.0]])],"derivedFrom":subQ1}),1.0]])]});}
            var Q82;
            {var subQ0=sQuery(id+"F4.wireOp",EDGE,"E192.trimOffspring");var subQ1=sQuery(id+"F4.wireOp",EDGE,"E75.0");var subQ2=makeQuery(id+"F4.imprint","INTERSECT",VERTEX,{"derivedFrom":[subQ1,subQ0]});Q82=makeQuery(id+"F4.imprint","IMPRINT",FACE,{"disambiguationData":[TD([[makeQuery(id+"F4.imprint","IMPRINT",EDGE,{"disambiguationData":[TD([[subQ2,1.0]])],"derivedFrom":subQ1}),1.0]])]});}
            var Q83;
            {var subQ0=sQuery(id+"F4.wireOp",EDGE,"E192.trimOffspring");var subQ1=sQuery(id+"F4.wireOp",EDGE,"E76.0");var subQ2=makeQuery(id+"F4.imprint","INTERSECT",VERTEX,{"derivedFrom":[subQ1,subQ0]});Q83=makeQuery(id+"F4.imprint","IMPRINT",FACE,{"disambiguationData":[TD([[makeQuery(id+"F4.imprint","IMPRINT",EDGE,{"disambiguationData":[TD([[subQ2,-1.0]])],"derivedFrom":subQ1}),1.0]])]});}
            var Q84;
            {var subQ0=sQuery(id+"F4.wireOp",EDGE,"E277.trimOffspring");var subQ1=sQuery(id+"F4.wireOp",EDGE,"E193.trimOffspring");var subQ2=makeQuery(id+"F4.imprint","INTERSECT",VERTEX,{"derivedFrom":[subQ1,subQ0]});Q84=makeQuery(id+"F4.imprint","IMPRINT",FACE,{"disambiguationData":[TD([[makeQuery(id+"F4.imprint","IMPRINT",EDGE,{"disambiguationData":[TD([[subQ2,-1.0]])],"derivedFrom":subQ1}),1.0]])]});}
            var Q85;
            {var subQ0=sQuery(id+"F4.wireOp",EDGE,"E277.trimOffspring");var subQ1=sQuery(id+"F4.wireOp",EDGE,"E194.trimOffspring");var subQ2=makeQuery(id+"F4.imprint","INTERSECT",VERTEX,{"derivedFrom":[subQ1,subQ0]});Q85=makeQuery(id+"F4.imprint","IMPRINT",FACE,{"disambiguationData":[TD([[makeQuery(id+"F4.imprint","IMPRINT",EDGE,{"disambiguationData":[TD([[subQ2,-1.0]])],"derivedFrom":subQ1}),1.0]])]});}
            var Q86;
            {var subQ0=sQuery(id+"F4.wireOp",EDGE,"E194.trimOffspring");var subQ1=sQuery(id+"F4.wireOp",EDGE,"E76.0");var subQ2=makeQuery(id+"F4.imprint","INTERSECT",VERTEX,{"derivedFrom":[subQ1,subQ0]});Q86=makeQuery(id+"F4.imprint","IMPRINT",FACE,{"disambiguationData":[TD([[makeQuery(id+"F4.imprint","IMPRINT",EDGE,{"disambiguationData":[TD([[subQ2,-1.0]])],"derivedFrom":subQ1}),1.0]])]});}
            var Q87;
            {var subQ0=sQuery(id+"F4.wireOp",EDGE,"E194.trimOffspring");var subQ1=sQuery(id+"F4.wireOp",EDGE,"E75.0");var subQ2=makeQuery(id+"F4.imprint","INTERSECT",VERTEX,{"derivedFrom":[subQ1,subQ0]});Q87=makeQuery(id+"F4.imprint","IMPRINT",FACE,{"disambiguationData":[TD([[makeQuery(id+"F4.imprint","IMPRINT",EDGE,{"disambiguationData":[TD([[subQ2,1.0]])],"derivedFrom":subQ1}),1.0]])]});}
            extrude(context, id + "F7", {"entities" : qUnion([Q0, Q1, Q2, Q3, Q4, Q5, Q6, Q7, Q8, Q9, Q10, Q11, Q12, Q13, Q14, Q15, Q16, Q17, Q18, Q19, Q20, Q21, Q22, Q23, Q24, Q25, Q26, Q27, Q28, Q29, Q30, Q31, Q32, Q33, Q34, Q35, Q36, Q37, Q38, Q39, Q40, Q41, Q42, Q43, Q44, Q45, Q46, Q47, Q48, Q49, Q50, Q51, Q52, Q53, Q54, Q55, Q56, Q57, Q58, Q59, Q60, Q61, Q62, Q63, Q64, Q65, Q66, Q67, Q68, Q69, Q70, Q71, Q72, Q73, Q74, Q75, Q76, Q77, Q78, Q79, Q80, Q81, Q82, Q83, Q84, Q85, Q86, Q87]), "operationType" : NewBodyOperationType.ADD, "depth" : 28.57 * mm, "offsetDistance" : 25.4 * mm});
        }
        {
            var Q0;
            {var subQ0=sQuery(id+"F4.wireOp",EDGE,"E279.trimOffspring");var subQ1=sQuery(id+"F4.wireOp",EDGE,"E196.trimOffspring");var subQ2=makeQuery(id+"F4.imprint","INTERSECT",VERTEX,{"derivedFrom":[subQ1,subQ0]});Q0=makeQuery(id+"F4.imprint","IMPRINT",FACE,{"disambiguationData":[TD([[makeQuery(id+"F4.imprint","IMPRINT",EDGE,{"disambiguationData":[TD([[subQ2,-1.0]])],"derivedFrom":subQ1}),-1.0]])]});}
            var Q1;
            {var subQ0=sQuery(id+"F4.wireOp",EDGE,"E196.trimOffspring");var subQ1=sQuery(id+"F4.wireOp",EDGE,"E75.0");var subQ2=makeQuery(id+"F4.imprint","INTERSECT",VERTEX,{"derivedFrom":[subQ1,subQ0]});Q1=makeQuery(id+"F4.imprint","IMPRINT",FACE,{"disambiguationData":[TD([[makeQuery(id+"F4.imprint","IMPRINT",EDGE,{"disambiguationData":[TD([[subQ2,-1.0]])],"derivedFrom":subQ1}),1.0]])]});}
            var Q2;
            {var subQ0=sQuery(id+"F4.wireOp",EDGE,"E196.trimOffspring");var subQ1=sQuery(id+"F4.wireOp",EDGE,"E76.0");var subQ2=makeQuery(id+"F4.imprint","INTERSECT",VERTEX,{"derivedFrom":[subQ1,subQ0]});Q2=makeQuery(id+"F4.imprint","IMPRINT",FACE,{"disambiguationData":[TD([[makeQuery(id+"F4.imprint","IMPRINT",EDGE,{"disambiguationData":[TD([[subQ2,1.0]])],"derivedFrom":subQ1}),1.0]])]});}
            var Q3;
            {var subQ0=sQuery(id+"F4.wireOp",EDGE,"E279.trimOffspring");var subQ1=sQuery(id+"F4.wireOp",EDGE,"E196.trimOffspring");var subQ2=makeQuery(id+"F4.imprint","INTERSECT",VERTEX,{"derivedFrom":[subQ1,subQ0]});Q3=makeQuery(id+"F4.imprint","IMPRINT",FACE,{"disambiguationData":[TD([[makeQuery(id+"F4.imprint","IMPRINT",EDGE,{"disambiguationData":[TD([[subQ2,-1.0]])],"derivedFrom":subQ1}),1.0]])]});}
            var Q4;
            {var subQ0=sQuery(id+"F4.wireOp",EDGE,"E279.trimOffspring");var subQ1=sQuery(id+"F4.wireOp",EDGE,"E198.trimOffspring");var subQ2=makeQuery(id+"F4.imprint","INTERSECT",VERTEX,{"derivedFrom":[subQ1,subQ0]});Q4=makeQuery(id+"F4.imprint","IMPRINT",FACE,{"disambiguationData":[TD([[makeQuery(id+"F4.imprint","IMPRINT",EDGE,{"disambiguationData":[TD([[subQ2,-1.0]])],"derivedFrom":subQ1}),-1.0]])]});}
            var Q5;
            {var subQ0=sQuery(id+"F4.wireOp",EDGE,"E198.trimOffspring");var subQ1=sQuery(id+"F4.wireOp",EDGE,"E75.0");var subQ2=makeQuery(id+"F4.imprint","INTERSECT",VERTEX,{"derivedFrom":[subQ1,subQ0]});Q5=makeQuery(id+"F4.imprint","IMPRINT",FACE,{"disambiguationData":[TD([[makeQuery(id+"F4.imprint","IMPRINT",EDGE,{"disambiguationData":[TD([[subQ2,-1.0]])],"derivedFrom":subQ1}),1.0]])]});}
            var Q6;
            {var subQ0=sQuery(id+"F4.wireOp",EDGE,"E198.trimOffspring");var subQ1=sQuery(id+"F4.wireOp",EDGE,"E76.0");var subQ2=makeQuery(id+"F4.imprint","INTERSECT",VERTEX,{"derivedFrom":[subQ1,subQ0]});Q6=makeQuery(id+"F4.imprint","IMPRINT",FACE,{"disambiguationData":[TD([[makeQuery(id+"F4.imprint","IMPRINT",EDGE,{"disambiguationData":[TD([[subQ2,1.0]])],"derivedFrom":subQ1}),1.0]])]});}
            var Q7;
            {var subQ0=sQuery(id+"F4.wireOp",EDGE,"E281.trimOffspring");var subQ1=sQuery(id+"F4.wireOp",EDGE,"E200.trimOffspring");var subQ2=makeQuery(id+"F4.imprint","INTERSECT",VERTEX,{"derivedFrom":[subQ1,subQ0]});Q7=makeQuery(id+"F4.imprint","IMPRINT",FACE,{"disambiguationData":[TD([[makeQuery(id+"F4.imprint","IMPRINT",EDGE,{"disambiguationData":[TD([[subQ2,-1.0]])],"derivedFrom":subQ1}),-1.0]])]});}
            var Q8;
            {var subQ0=sQuery(id+"F4.wireOp",EDGE,"E200.trimOffspring");var subQ1=sQuery(id+"F4.wireOp",EDGE,"E75.0");var subQ2=makeQuery(id+"F4.imprint","INTERSECT",VERTEX,{"derivedFrom":[subQ1,subQ0]});Q8=makeQuery(id+"F4.imprint","IMPRINT",FACE,{"disambiguationData":[TD([[makeQuery(id+"F4.imprint","IMPRINT",EDGE,{"disambiguationData":[TD([[subQ2,-1.0]])],"derivedFrom":subQ1}),1.0]])]});}
            var Q9;
            {var subQ0=sQuery(id+"F4.wireOp",EDGE,"E200.trimOffspring");var subQ1=sQuery(id+"F4.wireOp",EDGE,"E76.0");var subQ2=makeQuery(id+"F4.imprint","INTERSECT",VERTEX,{"derivedFrom":[subQ1,subQ0]});Q9=makeQuery(id+"F4.imprint","IMPRINT",FACE,{"disambiguationData":[TD([[makeQuery(id+"F4.imprint","IMPRINT",EDGE,{"disambiguationData":[TD([[subQ2,1.0]])],"derivedFrom":subQ1}),1.0]])]});}
            var Q10;
            {var subQ0=sQuery(id+"F4.wireOp",EDGE,"E281.trimOffspring");var subQ1=sQuery(id+"F4.wireOp",EDGE,"E200.trimOffspring");var subQ2=makeQuery(id+"F4.imprint","INTERSECT",VERTEX,{"derivedFrom":[subQ1,subQ0]});Q10=makeQuery(id+"F4.imprint","IMPRINT",FACE,{"disambiguationData":[TD([[makeQuery(id+"F4.imprint","IMPRINT",EDGE,{"disambiguationData":[TD([[subQ2,-1.0]])],"derivedFrom":subQ1}),1.0]])]});}
            var Q11;
            {var subQ0=sQuery(id+"F4.wireOp",EDGE,"E281.trimOffspring");var subQ1=sQuery(id+"F4.wireOp",EDGE,"E202.trimOffspring");var subQ2=makeQuery(id+"F4.imprint","INTERSECT",VERTEX,{"derivedFrom":[subQ1,subQ0]});Q11=makeQuery(id+"F4.imprint","IMPRINT",FACE,{"disambiguationData":[TD([[makeQuery(id+"F4.imprint","IMPRINT",EDGE,{"disambiguationData":[TD([[subQ2,-1.0]])],"derivedFrom":subQ1}),1.0]])]});}
            var Q12;
            {var subQ0=sQuery(id+"F4.wireOp",EDGE,"E202.trimOffspring");var subQ1=sQuery(id+"F4.wireOp",EDGE,"E75.0");var subQ2=makeQuery(id+"F4.imprint","INTERSECT",VERTEX,{"derivedFrom":[subQ1,subQ0]});Q12=makeQuery(id+"F4.imprint","IMPRINT",FACE,{"disambiguationData":[TD([[makeQuery(id+"F4.imprint","IMPRINT",EDGE,{"disambiguationData":[TD([[subQ2,1.0]])],"derivedFrom":subQ1}),1.0]])]});}
            var Q13;
            {var subQ0=sQuery(id+"F4.wireOp",EDGE,"E202.trimOffspring");var subQ1=sQuery(id+"F4.wireOp",EDGE,"E76.0");var subQ2=makeQuery(id+"F4.imprint","INTERSECT",VERTEX,{"derivedFrom":[subQ1,subQ0]});Q13=makeQuery(id+"F4.imprint","IMPRINT",FACE,{"disambiguationData":[TD([[makeQuery(id+"F4.imprint","IMPRINT",EDGE,{"disambiguationData":[TD([[subQ2,-1.0]])],"derivedFrom":subQ1}),1.0]])]});}
            var Q14;
            {var subQ0=sQuery(id+"F4.wireOp",EDGE,"E283.trimOffspring");var subQ1=sQuery(id+"F4.wireOp",EDGE,"E204.trimOffspring");var subQ2=makeQuery(id+"F4.imprint","INTERSECT",VERTEX,{"derivedFrom":[subQ1,subQ0]});Q14=makeQuery(id+"F4.imprint","IMPRINT",FACE,{"disambiguationData":[TD([[makeQuery(id+"F4.imprint","IMPRINT",EDGE,{"disambiguationData":[TD([[subQ2,-1.0]])],"derivedFrom":subQ1}),1.0]])]});}
            var Q15;
            {var subQ0=sQuery(id+"F4.wireOp",EDGE,"E204.trimOffspring");var subQ1=sQuery(id+"F4.wireOp",EDGE,"E75.0");var subQ2=makeQuery(id+"F4.imprint","INTERSECT",VERTEX,{"derivedFrom":[subQ1,subQ0]});Q15=makeQuery(id+"F4.imprint","IMPRINT",FACE,{"disambiguationData":[TD([[makeQuery(id+"F4.imprint","IMPRINT",EDGE,{"disambiguationData":[TD([[subQ2,1.0]])],"derivedFrom":subQ1}),1.0]])]});}
            var Q16;
            {var subQ0=sQuery(id+"F4.wireOp",EDGE,"E283.trimOffspring");var subQ1=sQuery(id+"F4.wireOp",EDGE,"E205.trimOffspring");var subQ2=makeQuery(id+"F4.imprint","INTERSECT",VERTEX,{"derivedFrom":[subQ1,subQ0]});Q16=makeQuery(id+"F4.imprint","IMPRINT",FACE,{"disambiguationData":[TD([[makeQuery(id+"F4.imprint","IMPRINT",EDGE,{"disambiguationData":[TD([[subQ2,-1.0]])],"derivedFrom":subQ1}),1.0]])]});}
            var Q17;
            {var subQ0=sQuery(id+"F4.wireOp",EDGE,"E204.trimOffspring");var subQ1=sQuery(id+"F4.wireOp",EDGE,"E76.0");var subQ2=makeQuery(id+"F4.imprint","INTERSECT",VERTEX,{"derivedFrom":[subQ1,subQ0]});Q17=makeQuery(id+"F4.imprint","IMPRINT",FACE,{"disambiguationData":[TD([[makeQuery(id+"F4.imprint","IMPRINT",EDGE,{"disambiguationData":[TD([[subQ2,-1.0]])],"derivedFrom":subQ1}),1.0]])]});}
            var Q18;
            {var subQ0=sQuery(id+"F4.wireOp",EDGE,"E283.trimOffspring");var subQ1=sQuery(id+"F4.wireOp",EDGE,"E206.trimOffspring");var subQ2=makeQuery(id+"F4.imprint","INTERSECT",VERTEX,{"derivedFrom":[subQ1,subQ0]});Q18=makeQuery(id+"F4.imprint","IMPRINT",FACE,{"disambiguationData":[TD([[makeQuery(id+"F4.imprint","IMPRINT",EDGE,{"disambiguationData":[TD([[subQ2,-1.0]])],"derivedFrom":subQ1}),-1.0]])]});}
            var Q19;
            {var subQ0=sQuery(id+"F4.wireOp",EDGE,"E206.trimOffspring");var subQ1=sQuery(id+"F4.wireOp",EDGE,"E75.0");var subQ2=makeQuery(id+"F4.imprint","INTERSECT",VERTEX,{"derivedFrom":[subQ1,subQ0]});Q19=makeQuery(id+"F4.imprint","IMPRINT",FACE,{"disambiguationData":[TD([[makeQuery(id+"F4.imprint","IMPRINT",EDGE,{"disambiguationData":[TD([[subQ2,-1.0]])],"derivedFrom":subQ1}),1.0]])]});}
            var Q20;
            {var subQ0=sQuery(id+"F4.wireOp",EDGE,"E206.trimOffspring");var subQ1=sQuery(id+"F4.wireOp",EDGE,"E76.0");var subQ2=makeQuery(id+"F4.imprint","INTERSECT",VERTEX,{"derivedFrom":[subQ1,subQ0]});Q20=makeQuery(id+"F4.imprint","IMPRINT",FACE,{"disambiguationData":[TD([[makeQuery(id+"F4.imprint","IMPRINT",EDGE,{"disambiguationData":[TD([[subQ2,1.0]])],"derivedFrom":subQ1}),1.0]])]});}
            var Q21;
            {var subQ0=sQuery(id+"F4.wireOp",EDGE,"E285.trimOffspring");var subQ1=sQuery(id+"F4.wireOp",EDGE,"E208.trimOffspring");var subQ2=makeQuery(id+"F4.imprint","INTERSECT",VERTEX,{"derivedFrom":[subQ1,subQ0]});Q21=makeQuery(id+"F4.imprint","IMPRINT",FACE,{"disambiguationData":[TD([[makeQuery(id+"F4.imprint","IMPRINT",EDGE,{"disambiguationData":[TD([[subQ2,-1.0]])],"derivedFrom":subQ1}),1.0]])]});}
            var Q22;
            {var subQ0=sQuery(id+"F4.wireOp",EDGE,"E208.trimOffspring");var subQ1=sQuery(id+"F4.wireOp",EDGE,"E75.0");var subQ2=makeQuery(id+"F4.imprint","INTERSECT",VERTEX,{"derivedFrom":[subQ1,subQ0]});Q22=makeQuery(id+"F4.imprint","IMPRINT",FACE,{"disambiguationData":[TD([[makeQuery(id+"F4.imprint","IMPRINT",EDGE,{"disambiguationData":[TD([[subQ2,1.0]])],"derivedFrom":subQ1}),1.0]])]});}
            var Q23;
            {var subQ0=sQuery(id+"F4.wireOp",EDGE,"E208.trimOffspring");var subQ1=sQuery(id+"F4.wireOp",EDGE,"E76.0");var subQ2=makeQuery(id+"F4.imprint","INTERSECT",VERTEX,{"derivedFrom":[subQ1,subQ0]});Q23=makeQuery(id+"F4.imprint","IMPRINT",FACE,{"disambiguationData":[TD([[makeQuery(id+"F4.imprint","IMPRINT",EDGE,{"disambiguationData":[TD([[subQ2,-1.0]])],"derivedFrom":subQ1}),1.0]])]});}
            var Q24;
            {var subQ0=sQuery(id+"F4.wireOp",EDGE,"E285.trimOffspring");var subQ1=sQuery(id+"F4.wireOp",EDGE,"E209.trimOffspring");var subQ2=makeQuery(id+"F4.imprint","INTERSECT",VERTEX,{"derivedFrom":[subQ1,subQ0]});Q24=makeQuery(id+"F4.imprint","IMPRINT",FACE,{"disambiguationData":[TD([[makeQuery(id+"F4.imprint","IMPRINT",EDGE,{"disambiguationData":[TD([[subQ2,-1.0]])],"derivedFrom":subQ1}),1.0]])]});}
            var Q25;
            {var subQ0=sQuery(id+"F4.wireOp",EDGE,"E285.trimOffspring");var subQ1=sQuery(id+"F4.wireOp",EDGE,"E210.trimOffspring");var subQ2=makeQuery(id+"F4.imprint","INTERSECT",VERTEX,{"derivedFrom":[subQ1,subQ0]});Q25=makeQuery(id+"F4.imprint","IMPRINT",FACE,{"disambiguationData":[TD([[makeQuery(id+"F4.imprint","IMPRINT",EDGE,{"disambiguationData":[TD([[subQ2,-1.0]])],"derivedFrom":subQ1}),1.0]])]});}
            var Q26;
            {var subQ0=sQuery(id+"F4.wireOp",EDGE,"E210.trimOffspring");var subQ1=sQuery(id+"F4.wireOp",EDGE,"E75.0");var subQ2=makeQuery(id+"F4.imprint","INTERSECT",VERTEX,{"derivedFrom":[subQ1,subQ0]});Q26=makeQuery(id+"F4.imprint","IMPRINT",FACE,{"disambiguationData":[TD([[makeQuery(id+"F4.imprint","IMPRINT",EDGE,{"disambiguationData":[TD([[subQ2,1.0]])],"derivedFrom":subQ1}),1.0]])]});}
            var Q27;
            {var subQ0=sQuery(id+"F4.wireOp",EDGE,"E210.trimOffspring");var subQ1=sQuery(id+"F4.wireOp",EDGE,"E76.0");var subQ2=makeQuery(id+"F4.imprint","INTERSECT",VERTEX,{"derivedFrom":[subQ1,subQ0]});Q27=makeQuery(id+"F4.imprint","IMPRINT",FACE,{"disambiguationData":[TD([[makeQuery(id+"F4.imprint","IMPRINT",EDGE,{"disambiguationData":[TD([[subQ2,-1.0]])],"derivedFrom":subQ1}),1.0]])]});}
            var Q28;
            {var subQ0=sQuery(id+"F4.wireOp",EDGE,"E287.trimOffspring");var subQ1=sQuery(id+"F4.wireOp",EDGE,"E77.0");var subQ2=makeQuery(id+"F4.imprint","INTERSECT",VERTEX,{"derivedFrom":[subQ1,subQ0]});Q28=makeQuery(id+"F4.imprint","IMPRINT",FACE,{"disambiguationData":[TD([[makeQuery(id+"F4.imprint","IMPRINT",EDGE,{"disambiguationData":[TD([[subQ2,1.0]])],"derivedFrom":subQ1}),1.0]])]});}
            var Q29;
            {var subQ0=sQuery(id+"F4.wireOp",EDGE,"E287.trimOffspring");var subQ1=sQuery(id+"F4.wireOp",EDGE,"E212.trimOffspring");var subQ2=makeQuery(id+"F4.imprint","INTERSECT",VERTEX,{"derivedFrom":[subQ1,subQ0]});Q29=makeQuery(id+"F4.imprint","IMPRINT",FACE,{"disambiguationData":[TD([[makeQuery(id+"F4.imprint","IMPRINT",EDGE,{"disambiguationData":[TD([[subQ2,-1.0]])],"derivedFrom":subQ1}),-1.0]])]});}
            var Q30;
            {var subQ0=sQuery(id+"F4.wireOp",EDGE,"E212.trimOffspring");var subQ1=sQuery(id+"F4.wireOp",EDGE,"E75.0");var subQ2=makeQuery(id+"F4.imprint","INTERSECT",VERTEX,{"derivedFrom":[subQ1,subQ0]});Q30=makeQuery(id+"F4.imprint","IMPRINT",FACE,{"disambiguationData":[TD([[makeQuery(id+"F4.imprint","IMPRINT",EDGE,{"disambiguationData":[TD([[subQ2,-1.0]])],"derivedFrom":subQ1}),1.0]])]});}
            var Q31;
            {var subQ0=sQuery(id+"F4.wireOp",EDGE,"E212.trimOffspring");var subQ1=sQuery(id+"F4.wireOp",EDGE,"E76.0");var subQ2=makeQuery(id+"F4.imprint","INTERSECT",VERTEX,{"derivedFrom":[subQ1,subQ0]});Q31=makeQuery(id+"F4.imprint","IMPRINT",FACE,{"disambiguationData":[TD([[makeQuery(id+"F4.imprint","IMPRINT",EDGE,{"disambiguationData":[TD([[subQ2,1.0]])],"derivedFrom":subQ1}),1.0]])]});}
            extrude(context, id + "F8", {"entities" : qUnion([Q0, Q1, Q2, Q3, Q4, Q5, Q6, Q7, Q8, Q9, Q10, Q11, Q12, Q13, Q14, Q15, Q16, Q17, Q18, Q19, Q20, Q21, Q22, Q23, Q24, Q25, Q26, Q27, Q28, Q29, Q30, Q31]), "operationType" : NewBodyOperationType.ADD, "depth" : 28.57 * mm, "offsetDistance" : 25.4 * mm});
        }
        {
            var Q0;
            {var subQ2=sQuery(id+"F4.wireOp",EDGE,"E289");Q0=makeQuery(id+"F4.imprint","IMPRINT",FACE,{"disambiguationData":[TD([[makeQuery(id+"F4.imprint","IMPRINT",EDGE,{"derivedFrom":subQ2}),-1.0]])]});}
            var Q1;
            {var subQ0=sQuery(id+"F4.wireOp",EDGE,"E291");Q1=makeQuery(id+"F4.imprint","IMPRINT",FACE,{"disambiguationData":[TD([[makeQuery(id+"F4.imprint","IMPRINT",EDGE,{"derivedFrom":subQ0}),-1.0]])]});}
            var Q2;
            {var subQ0=sQuery(id+"F4.wireOp",EDGE,"E293");Q2=makeQuery(id+"F4.imprint","IMPRINT",FACE,{"disambiguationData":[TD([[makeQuery(id+"F4.imprint","IMPRINT",EDGE,{"derivedFrom":subQ0}),-1.0]])]});}
            var Q3;
            {var subQ0=sQuery(id+"F4.wireOp",EDGE,"E295");Q3=makeQuery(id+"F4.imprint","IMPRINT",FACE,{"disambiguationData":[TD([[makeQuery(id+"F4.imprint","IMPRINT",EDGE,{"derivedFrom":subQ0}),-1.0]])]});}
            var Q4;
            {var subQ2=sQuery(id+"F4.wireOp",EDGE,"E297");Q4=makeQuery(id+"F4.imprint","IMPRINT",FACE,{"disambiguationData":[TD([[makeQuery(id+"F4.imprint","IMPRINT",EDGE,{"derivedFrom":subQ2}),-1.0]])]});}
            var Q5;
            {var subQ0=sQuery(id+"F4.wireOp",EDGE,"E299");Q5=makeQuery(id+"F4.imprint","IMPRINT",FACE,{"disambiguationData":[TD([[makeQuery(id+"F4.imprint","IMPRINT",EDGE,{"derivedFrom":subQ0}),1.0]])]});}
            var Q6;
            {var subQ0=sQuery(id+"F4.wireOp",EDGE,"E301");Q6=makeQuery(id+"F4.imprint","IMPRINT",FACE,{"disambiguationData":[TD([[makeQuery(id+"F4.imprint","IMPRINT",EDGE,{"derivedFrom":subQ0}),-1.0]])]});}
            var Q7;
            {var subQ2=sQuery(id+"F4.wireOp",EDGE,"E304");Q7=makeQuery(id+"F4.imprint","IMPRINT",FACE,{"disambiguationData":[TD([[makeQuery(id+"F4.imprint","IMPRINT",EDGE,{"derivedFrom":subQ2}),1.0]])]});}
            var Q8;
            {var subQ2=sQuery(id+"F4.wireOp",EDGE,"E306");Q8=makeQuery(id+"F4.imprint","IMPRINT",FACE,{"disambiguationData":[TD([[makeQuery(id+"F4.imprint","IMPRINT",EDGE,{"derivedFrom":subQ2}),1.0]])]});}
            var Q9;
            {var subQ2=sQuery(id+"F4.wireOp",EDGE,"E308");Q9=makeQuery(id+"F4.imprint","IMPRINT",FACE,{"disambiguationData":[TD([[makeQuery(id+"F4.imprint","IMPRINT",EDGE,{"derivedFrom":subQ2}),1.0]])]});}
            var Q10;
            {var subQ0=sQuery(id+"F4.wireOp",EDGE,"E310");Q10=makeQuery(id+"F4.imprint","IMPRINT",FACE,{"disambiguationData":[TD([[makeQuery(id+"F4.imprint","IMPRINT",EDGE,{"derivedFrom":subQ0}),1.0]])]});}
            var Q11;
            {var subQ2=sQuery(id+"F4.wireOp",EDGE,"E312");Q11=makeQuery(id+"F4.imprint","IMPRINT",FACE,{"disambiguationData":[TD([[makeQuery(id+"F4.imprint","IMPRINT",EDGE,{"derivedFrom":subQ2}),1.0]])]});}
            var Q12;
            {var subQ0=sQuery(id+"F4.wireOp",EDGE,"E314");Q12=makeQuery(id+"F4.imprint","IMPRINT",FACE,{"disambiguationData":[TD([[makeQuery(id+"F4.imprint","IMPRINT",EDGE,{"derivedFrom":subQ0}),1.0]])]});}
            var Q13;
            {var subQ0=sQuery(id+"F4.wireOp",EDGE,"E316");Q13=makeQuery(id+"F4.imprint","IMPRINT",FACE,{"disambiguationData":[TD([[makeQuery(id+"F4.imprint","IMPRINT",EDGE,{"derivedFrom":subQ0}),1.0]])]});}
            var Q14;
            {var subQ0=sQuery(id+"F4.wireOp",EDGE,"E318");Q14=makeQuery(id+"F4.imprint","IMPRINT",FACE,{"disambiguationData":[TD([[makeQuery(id+"F4.imprint","IMPRINT",EDGE,{"derivedFrom":subQ0}),1.0]])]});}
            var Q15;
            {var subQ2=sQuery(id+"F4.wireOp",EDGE,"E320");Q15=makeQuery(id+"F4.imprint","IMPRINT",FACE,{"disambiguationData":[TD([[makeQuery(id+"F4.imprint","IMPRINT",EDGE,{"derivedFrom":subQ2}),1.0]])]});}
            var Q16;
            {var subQ0=sQuery(id+"F4.wireOp",EDGE,"E324");Q16=makeQuery(id+"F4.imprint","IMPRINT",FACE,{"disambiguationData":[TD([[makeQuery(id+"F4.imprint","IMPRINT",EDGE,{"derivedFrom":subQ0}),1.0]])]});}
            var Q17;
            {var subQ0=sQuery(id+"F4.wireOp",EDGE,"E322");Q17=makeQuery(id+"F4.imprint","IMPRINT",FACE,{"disambiguationData":[TD([[makeQuery(id+"F4.imprint","IMPRINT",EDGE,{"derivedFrom":subQ0}),1.0]])]});}
            var Q18;
            {var subQ0=sQuery(id+"F4.wireOp",EDGE,"E328");Q18=makeQuery(id+"F4.imprint","IMPRINT",FACE,{"disambiguationData":[TD([[makeQuery(id+"F4.imprint","IMPRINT",EDGE,{"derivedFrom":subQ0}),1.0]])]});}
            var Q19;
            {var subQ0=sQuery(id+"F4.wireOp",EDGE,"E330");Q19=makeQuery(id+"F4.imprint","IMPRINT",FACE,{"disambiguationData":[TD([[makeQuery(id+"F4.imprint","IMPRINT",EDGE,{"derivedFrom":subQ0}),1.0]])]});}
            var Q20;
            {var subQ0=sQuery(id+"F4.wireOp",EDGE,"E326");Q20=makeQuery(id+"F4.imprint","IMPRINT",FACE,{"disambiguationData":[TD([[makeQuery(id+"F4.imprint","IMPRINT",EDGE,{"derivedFrom":subQ0}),1.0]])]});}
            var Q21;
            {var subQ0=sQuery(id+"F4.wireOp",EDGE,"E332");Q21=makeQuery(id+"F4.imprint","IMPRINT",FACE,{"disambiguationData":[TD([[makeQuery(id+"F4.imprint","IMPRINT",EDGE,{"derivedFrom":subQ0}),-1.0]])]});}
            var Q22;
            {var subQ0=sQuery(id+"F4.wireOp",EDGE,"E334");Q22=makeQuery(id+"F4.imprint","IMPRINT",FACE,{"disambiguationData":[TD([[makeQuery(id+"F4.imprint","IMPRINT",EDGE,{"derivedFrom":subQ0}),-1.0]])]});}
            var Q23;
            {var subQ0=sQuery(id+"F4.wireOp",EDGE,"E336");Q23=makeQuery(id+"F4.imprint","IMPRINT",FACE,{"disambiguationData":[TD([[makeQuery(id+"F4.imprint","IMPRINT",EDGE,{"derivedFrom":subQ0}),-1.0]])]});}
            var Q24;
            {var subQ0=sQuery(id+"F4.wireOp",EDGE,"E350");Q24=makeQuery(id+"F4.imprint","IMPRINT",FACE,{"disambiguationData":[TD([[makeQuery(id+"F4.imprint","IMPRINT",EDGE,{"derivedFrom":subQ0}),1.0]])]});}
            var Q25;
            {var subQ0=sQuery(id+"F4.wireOp",EDGE,"E348");Q25=makeQuery(id+"F4.imprint","IMPRINT",FACE,{"disambiguationData":[TD([[makeQuery(id+"F4.imprint","IMPRINT",EDGE,{"derivedFrom":subQ0}),-1.0]])]});}
            var Q26;
            {var subQ0=sQuery(id+"F4.wireOp",EDGE,"E346");Q26=makeQuery(id+"F4.imprint","IMPRINT",FACE,{"disambiguationData":[TD([[makeQuery(id+"F4.imprint","IMPRINT",EDGE,{"derivedFrom":subQ0}),-1.0]])]});}
            var Q27;
            {var subQ0=sQuery(id+"F4.wireOp",EDGE,"E344");Q27=makeQuery(id+"F4.imprint","IMPRINT",FACE,{"disambiguationData":[TD([[makeQuery(id+"F4.imprint","IMPRINT",EDGE,{"derivedFrom":subQ0}),-1.0]])]});}
            var Q28;
            {var subQ0=sQuery(id+"F4.wireOp",EDGE,"E342");Q28=makeQuery(id+"F4.imprint","IMPRINT",FACE,{"disambiguationData":[TD([[makeQuery(id+"F4.imprint","IMPRINT",EDGE,{"derivedFrom":subQ0}),-1.0]])]});}
            var Q29;
            {var subQ0=sQuery(id+"F4.wireOp",EDGE,"E340");Q29=makeQuery(id+"F4.imprint","IMPRINT",FACE,{"disambiguationData":[TD([[makeQuery(id+"F4.imprint","IMPRINT",EDGE,{"derivedFrom":subQ0}),-1.0]])]});}
            var Q30;
            {var subQ2=sQuery(id+"F4.wireOp",EDGE,"E338");Q30=makeQuery(id+"F4.imprint","IMPRINT",FACE,{"disambiguationData":[TD([[makeQuery(id+"F4.imprint","IMPRINT",EDGE,{"derivedFrom":subQ2}),-1.0]])]});}
            extrude(context, id + "F9", {"entities" : qUnion([Q0, Q1, Q2, Q3, Q4, Q5, Q6, Q7, Q8, Q9, Q10, Q11, Q12, Q13, Q14, Q15, Q16, Q17, Q18, Q19, Q20, Q21, Q22, Q23, Q24, Q25, Q26, Q27, Q28, Q29, Q30]), "operationType" : NewBodyOperationType.ADD, "depth" : 28.57 * mm, "offsetDistance" : 25.4 * mm});
        }
        {
            var Q0;
            {var subQ0=sQuery(id+"F4.wireOp",EDGE,"E213.trimOffspring");var subQ1=sQuery(id+"F4.wireOp",EDGE,"E211.trimOffspring");var subQ2=sQuery(id+"F4.wireOp",EDGE,"E208.trimOffspring");var subQ3=sQuery(id+"F4.wireOp",EDGE,"E206.trimOffspring");var subQ4=sQuery(id+"F4.wireOp",EDGE,"E204.trimOffspring");var subQ5=sQuery(id+"F4.wireOp",EDGE,"E203.trimOffspring");var subQ6=sQuery(id+"F4.wireOp",EDGE,"E201.trimOffspring");var subQ7=sQuery(id+"F4.wireOp",EDGE,"E198.trimOffspring");var subQ8=sQuery(id+"F4.wireOp",EDGE,"E197.trimOffspring");var subQ9=sQuery(id+"F4.wireOp",EDGE,"E195.trimOffspring");var subQ10=sQuery(id+"F4.wireOp",EDGE,"E192.trimOffspring");var subQ11=sQuery(id+"F4.wireOp",EDGE,"E190.trimOffspring");var subQ12=sQuery(id+"F4.wireOp",EDGE,"E188.trimOffspring");var subQ13=sQuery(id+"F4.wireOp",EDGE,"E187.trimOffspring");var subQ14=sQuery(id+"F4.wireOp",EDGE,"E184.trimOffspring");var subQ15=sQuery(id+"F4.wireOp",EDGE,"E183.trimOffspring");var subQ16=sQuery(id+"F4.wireOp",EDGE,"E180.trimOffspring");var subQ17=sQuery(id+"F4.wireOp",EDGE,"E179.trimOffspring");var subQ18=sQuery(id+"F4.wireOp",EDGE,"E176.trimOffspring");var subQ19=sQuery(id+"F4.wireOp",EDGE,"E175.trimOffspring");var subQ20=sQuery(id+"F4.wireOp",EDGE,"E170.trimOffspring");var subQ21=sQuery(id+"F4.wireOp",EDGE,"E169.trimOffspring");var subQ22=sQuery(id+"F4.wireOp",EDGE,"E166.trimOffspring");var subQ23=sQuery(id+"F4.wireOp",EDGE,"E165.trimOffspring");var subQ24=sQuery(id+"F4.wireOp",EDGE,"E162.trimOffspring");var subQ25=sQuery(id+"F4.wireOp",EDGE,"E160.trimOffspring");var subQ26=sQuery(id+"F4.wireOp",EDGE,"E159.trimOffspring");var subQ27=sQuery(id+"F4.wireOp",EDGE,"E157.trimOffspring");var subQ28=sQuery(id+"F4.wireOp",EDGE,"E154.trimOffspring");var subQ29=sQuery(id+"F4.wireOp",EDGE,"E153.trimOffspring");var subQ30=sQuery(id+"F4.wireOp",EDGE,"E150.trimOffspring");var subQ31=sQuery(id+"F4.wireOp",EDGE,"E149.trimOffspring");var subQ32=sQuery(id+"F4.wireOp",EDGE,"E146.0");var subQ33=sQuery(id+"F4.wireOp",EDGE,"E145.0");var subQ34=sQuery(id+"F4.wireOp",EDGE,"E142.0");var subQ35=sQuery(id+"F4.wireOp",EDGE,"E141.0");var subQ36=sQuery(id+"F4.wireOp",EDGE,"E138.0");var subQ37=sQuery(id+"F4.wireOp",EDGE,"E137.0");var subQ38=sQuery(id+"F4.wireOp",EDGE,"E134.0");var subQ39=sQuery(id+"F4.wireOp",EDGE,"E133.0");var subQ40=sQuery(id+"F4.wireOp",EDGE,"E130.0");var subQ41=sQuery(id+"F4.wireOp",EDGE,"E129.0");var subQ42=sQuery(id+"F4.wireOp",EDGE,"E126.0");var subQ43=sQuery(id+"F4.wireOp",EDGE,"E125.0");var subQ44=sQuery(id+"F4.wireOp",EDGE,"E122.0");var subQ45=sQuery(id+"F4.wireOp",EDGE,"E121.0");var subQ46=sQuery(id+"F4.wireOp",EDGE,"E173.trimOffspring");var subQ47=sQuery(id+"F4.wireOp",EDGE,"E120.trimOffspring");var subQ48=sQuery(id+"F4.wireOp",EDGE,"E302");var subQ49=sQuery(id+"F4.wireOp",EDGE,"E103.0");var subQ50=sQuery(id+"F4.wireOp",EDGE,"E100.0");var subQ51=sQuery(id+"F4.wireOp",EDGE,"E99.0");var subQ52=sQuery(id+"F4.wireOp",EDGE,"E96.0");var subQ53=sQuery(id+"F4.wireOp",EDGE,"E95.0");var subQ54=sQuery(id+"F4.wireOp",EDGE,"E92.0");var subQ55=sQuery(id+"F4.wireOp",EDGE,"E91.0");var subQ56=sQuery(id+"F4.wireOp",EDGE,"E88.0");var subQ57=sQuery(id+"F4.wireOp",EDGE,"E87.0");var subQ58=sQuery(id+"F4.wireOp",EDGE,"E84.0");var subQ59=sQuery(id+"F4.wireOp",EDGE,"E83.0");var subQ60=sQuery(id+"F4.wireOp",EDGE,"E80.0");var subQ61=sQuery(id+"F4.wireOp",EDGE,"E79.0");var subQ62=sQuery(id+"F4.wireOp",EDGE,"E76.0");var subQ63=sQuery(id+"F4.wireOp",EDGE,"E75.0");var subQ64=sQuery(id+"F4.wireOp",EDGE,"E68.0");var subQ65=sQuery(id+"F4.wireOp",EDGE,"E67.0");var subQ66=sQuery(id+"F4.wireOp",EDGE,"E72.0");var subQ67=sQuery(id+"F4.wireOp",EDGE,"E70.0");Q0=makeQuery(id+"F9.boolean.opBoolean","MERGE",FACE,{"derivedFrom":[makeQuery(id+"F8.boolean.opBoolean","MERGE",FACE,{"derivedFrom":[makeQuery(id+"F7.boolean.opBoolean","MERGE",FACE,{"derivedFrom":[makeQuery(id+"F6.boolean.opBoolean","MERGE",FACE,{"derivedFrom":[makeQuery(id+"F5.boolean.opBoolean","MERGE",FACE,{"derivedFrom":[makeQuery(id+"F3.boolean.opBoolean","MERGE",FACE,{"derivedFrom":[makeQuery(id+"F1.opExtrude","CAP_FACE",FACE,{"disambiguationData":[OSD([sQuery(id+"F0.wireOp",EDGE,"E0.top"),sQuery(id+"F0.wireOp",EDGE,"E1.0"),sQuery(id+"F0.wireOp",EDGE,"E2"),sQuery(id+"F0.wireOp",EDGE,"E3"),sQuery(id+"F0.wireOp",EDGE,"E4"),sQuery(id+"F0.wireOp",EDGE,"E5"),sQuery(id+"F0.wireOp",EDGE,"E6"),sQuery(id+"F0.wireOp",EDGE,"E7"),sQuery(id+"F0.wireOp",EDGE,"E8"),sQuery(id+"F0.wireOp",EDGE,"E9"),sQuery(id+"F0.wireOp",EDGE,"E10"),sQuery(id+"F0.wireOp",EDGE,"E11"),sQuery(id+"F0.wireOp",EDGE,"E12"),sQuery(id+"F0.wireOp",EDGE,"E13"),sQuery(id+"F0.wireOp",EDGE,"E14.0"),sQuery(id+"F0.wireOp",EDGE,"E15"),sQuery(id+"F0.wireOp",EDGE,"E16"),sQuery(id+"F0.wireOp",EDGE,"E17"),sQuery(id+"F0.wireOp",EDGE,"E18"),sQuery(id+"F0.wireOp",EDGE,"E19"),sQuery(id+"F0.wireOp",EDGE,"E20"),sQuery(id+"F0.wireOp",EDGE,"E21"),sQuery(id+"F0.wireOp",EDGE,"E22"),sQuery(id+"F0.wireOp",EDGE,"E23"),sQuery(id+"F0.wireOp",EDGE,"E24"),sQuery(id+"F0.wireOp",EDGE,"E25"),sQuery(id+"F0.wireOp",EDGE,"E26"),sQuery(id+"F0.wireOp",EDGE,"E27")])],"isStart":true}),makeQuery(id+"F3.opExtrude","CAP_FACE",FACE,{"disambiguationData":[OSD([sQuery(id+"F2.wireOp",EDGE,"E31.0"),sQuery(id+"F2.wireOp",EDGE,"E32.0"),sQuery(id+"F2.wireOp",EDGE,"E33.0"),sQuery(id+"F2.wireOp",EDGE,"E34.0"),sQuery(id+"F2.wireOp",EDGE,"E42.0"),sQuery(id+"F2.wireOp",EDGE,"E42.1"),sQuery(id+"F2.wireOp",EDGE,"E42.2"),sQuery(id+"F2.wireOp",EDGE,"E42.3")])],"isStart":true}),makeQuery(id+"F3.opExtrude","CAP_FACE",FACE,{"disambiguationData":[OSD([sQuery(id+"F2.wireOp",EDGE,"E37.0"),sQuery(id+"F2.wireOp",EDGE,"E59.0"),sQuery(id+"F2.wireOp",EDGE,"E60.0"),sQuery(id+"F2.wireOp",EDGE,"E61.0"),sQuery(id+"F2.wireOp",EDGE,"E62.0"),sQuery(id+"F2.wireOp",EDGE,"E62.1"),sQuery(id+"F2.wireOp",EDGE,"E62.2"),sQuery(id+"F2.wireOp",EDGE,"E62.3")])],"isStart":true}),makeQuery(id+"F3.opExtrude","CAP_FACE",FACE,{"disambiguationData":[OSD([sQuery(id+"F2.wireOp",EDGE,"E38.0"),sQuery(id+"F2.wireOp",EDGE,"E39.0"),sQuery(id+"F2.wireOp",EDGE,"E40.0"),sQuery(id+"F2.wireOp",EDGE,"E41.0"),sQuery(id+"F2.wireOp",EDGE,"E43.0"),sQuery(id+"F2.wireOp",EDGE,"E43.1"),sQuery(id+"F2.wireOp",EDGE,"E43.2"),sQuery(id+"F2.wireOp",EDGE,"E43.3")])],"isStart":true}),makeQuery(id+"F3.opExtrude","CAP_FACE",FACE,{"disambiguationData":[OSD([sQuery(id+"F2.wireOp",EDGE,"E44.0"),sQuery(id+"F2.wireOp",EDGE,"E45.0"),sQuery(id+"F2.wireOp",EDGE,"E46.0"),sQuery(id+"F2.wireOp",EDGE,"E47.0"),sQuery(id+"F2.wireOp",EDGE,"E56.0"),sQuery(id+"F2.wireOp",EDGE,"E56.1"),sQuery(id+"F2.wireOp",EDGE,"E56.2"),sQuery(id+"F2.wireOp",EDGE,"E56.3")])],"isStart":true}),makeQuery(id+"F3.opExtrude","CAP_FACE",FACE,{"disambiguationData":[OSD([sQuery(id+"F2.wireOp",EDGE,"E48.0"),sQuery(id+"F2.wireOp",EDGE,"E49.0"),sQuery(id+"F2.wireOp",EDGE,"E50.0"),sQuery(id+"F2.wireOp",EDGE,"E51.0"),sQuery(id+"F2.wireOp",EDGE,"E57.0"),sQuery(id+"F2.wireOp",EDGE,"E57.1"),sQuery(id+"F2.wireOp",EDGE,"E57.2"),sQuery(id+"F2.wireOp",EDGE,"E57.3")])],"isStart":true}),makeQuery(id+"F3.opExtrude","CAP_FACE",FACE,{"disambiguationData":[OSD([sQuery(id+"F2.wireOp",EDGE,"E52.0"),sQuery(id+"F2.wireOp",EDGE,"E53.0"),sQuery(id+"F2.wireOp",EDGE,"E54.0"),sQuery(id+"F2.wireOp",EDGE,"E55.0"),sQuery(id+"F2.wireOp",EDGE,"E58.0"),sQuery(id+"F2.wireOp",EDGE,"E58.1"),sQuery(id+"F2.wireOp",EDGE,"E58.2"),sQuery(id+"F2.wireOp",EDGE,"E58.3")])],"isStart":true})]}),makeQuery(id+"F5.opExtrude","CAP_FACE",FACE,{"disambiguationData":[OSD([subQ67,sQuery(id+"F4.wireOp",EDGE,"E71.0"),subQ66,sQuery(id+"F4.wireOp",EDGE,"E104.0"),sQuery(id+"F4.wireOp",EDGE,"E105.0"),sQuery(id+"F4.wireOp",EDGE,"E217.trimOffspring"),sQuery(id+"F4.wireOp",EDGE,"E233.trimOffspring"),subQ48])],"isStart":true}),makeQuery(id+"F5.opExtrude","CAP_FACE",FACE,{"disambiguationData":[OSD([subQ67,subQ66,subQ50,sQuery(id+"F4.wireOp",EDGE,"E101.0"),sQuery(id+"F4.wireOp",EDGE,"E102.0"),subQ49,sQuery(id+"F4.wireOp",EDGE,"E231.trimOffspring"),sQuery(id+"F4.wireOp",EDGE,"E232.trimOffspring")])],"isStart":true}),makeQuery(id+"F5.opExtrude","CAP_FACE",FACE,{"disambiguationData":[OSD([subQ67,subQ66,subQ52,sQuery(id+"F4.wireOp",EDGE,"E97.0"),sQuery(id+"F4.wireOp",EDGE,"E98.0"),subQ51,sQuery(id+"F4.wireOp",EDGE,"E229.trimOffspring"),sQuery(id+"F4.wireOp",EDGE,"E230.trimOffspring")])],"isStart":true}),makeQuery(id+"F5.opExtrude","CAP_FACE",FACE,{"disambiguationData":[OSD([subQ67,subQ66,subQ54,sQuery(id+"F4.wireOp",EDGE,"E93.0"),sQuery(id+"F4.wireOp",EDGE,"E94.0"),subQ53,sQuery(id+"F4.wireOp",EDGE,"E227.trimOffspring"),sQuery(id+"F4.wireOp",EDGE,"E228.trimOffspring")])],"isStart":true}),makeQuery(id+"F5.opExtrude","CAP_FACE",FACE,{"disambiguationData":[OSD([subQ67,subQ66,subQ56,sQuery(id+"F4.wireOp",EDGE,"E89.0"),sQuery(id+"F4.wireOp",EDGE,"E90.0"),subQ55,sQuery(id+"F4.wireOp",EDGE,"E224.trimOffspring"),sQuery(id+"F4.wireOp",EDGE,"E226.trimOffspring")])],"isStart":true}),makeQuery(id+"F5.opExtrude","CAP_FACE",FACE,{"disambiguationData":[OSD([subQ67,subQ66,subQ58,sQuery(id+"F4.wireOp",EDGE,"E85.0"),sQuery(id+"F4.wireOp",EDGE,"E86.0"),subQ57,sQuery(id+"F4.wireOp",EDGE,"E220.trimOffspring"),sQuery(id+"F4.wireOp",EDGE,"E221.trimOffspring")])],"isStart":true}),makeQuery(id+"F5.opExtrude","CAP_FACE",FACE,{"disambiguationData":[OSD([subQ67,subQ66,subQ60,sQuery(id+"F4.wireOp",EDGE,"E81.0"),sQuery(id+"F4.wireOp",EDGE,"E82.0"),subQ59,sQuery(id+"F4.wireOp",EDGE,"E218.trimOffspring"),sQuery(id+"F4.wireOp",EDGE,"E219.trimOffspring"),sQuery(id+"F4.wireOp",EDGE,"E222.trimOffspring")])],"isStart":true}),makeQuery(id+"F5.opExtrude","CAP_FACE",FACE,{"disambiguationData":[OSD([subQ67,subQ66,sQuery(id+"F4.wireOp",EDGE,"E73.0"),sQuery(id+"F4.wireOp",EDGE,"E78"),subQ61,sQuery(id+"F4.wireOp",EDGE,"E215.0"),sQuery(id+"F4.wireOp",EDGE,"E216.0")])],"isStart":true})]}),makeQuery(id+"F6.opExtrude","CAP_FACE",FACE,{"disambiguationData":[OSD([sQuery(id+"F4.wireOp",EDGE,"E66.0"),subQ65,subQ64,subQ32,sQuery(id+"F4.wireOp",EDGE,"E147.0"),sQuery(id+"F4.wireOp",EDGE,"E250.trimOffspring"),sQuery(id+"F4.wireOp",EDGE,"E251.trimOffspring")])],"isStart":true}),makeQuery(id+"F6.opExtrude","CAP_FACE",FACE,{"disambiguationData":[OSD([subQ65,subQ64,subQ34,sQuery(id+"F4.wireOp",EDGE,"E143.0"),sQuery(id+"F4.wireOp",EDGE,"E144.0"),subQ33,sQuery(id+"F4.wireOp",EDGE,"E248.trimOffspring"),sQuery(id+"F4.wireOp",EDGE,"E249.trimOffspring")])],"isStart":true}),makeQuery(id+"F6.opExtrude","CAP_FACE",FACE,{"disambiguationData":[OSD([subQ65,subQ64,subQ36,sQuery(id+"F4.wireOp",EDGE,"E139.0"),sQuery(id+"F4.wireOp",EDGE,"E140.0"),subQ35,sQuery(id+"F4.wireOp",EDGE,"E246.trimOffspring"),sQuery(id+"F4.wireOp",EDGE,"E247.trimOffspring")])],"isStart":true}),makeQuery(id+"F6.opExtrude","CAP_FACE",FACE,{"disambiguationData":[OSD([subQ65,subQ64,subQ38,sQuery(id+"F4.wireOp",EDGE,"E135.0"),sQuery(id+"F4.wireOp",EDGE,"E136.0"),subQ37,sQuery(id+"F4.wireOp",EDGE,"E244.trimOffspring"),sQuery(id+"F4.wireOp",EDGE,"E245.trimOffspring")])],"isStart":true}),makeQuery(id+"F6.opExtrude","CAP_FACE",FACE,{"disambiguationData":[OSD([subQ65,subQ64,subQ40,sQuery(id+"F4.wireOp",EDGE,"E131.0"),sQuery(id+"F4.wireOp",EDGE,"E132.0"),subQ39,sQuery(id+"F4.wireOp",EDGE,"E242.trimOffspring"),sQuery(id+"F4.wireOp",EDGE,"E243.trimOffspring")])],"isStart":true}),makeQuery(id+"F6.opExtrude","CAP_FACE",FACE,{"disambiguationData":[OSD([subQ65,subQ64,subQ42,sQuery(id+"F4.wireOp",EDGE,"E127.0"),sQuery(id+"F4.wireOp",EDGE,"E128.0"),subQ41,sQuery(id+"F4.wireOp",EDGE,"E240.trimOffspring"),sQuery(id+"F4.wireOp",EDGE,"E241.trimOffspring")])],"isStart":true}),makeQuery(id+"F6.opExtrude","CAP_FACE",FACE,{"disambiguationData":[OSD([subQ65,subQ64,subQ44,sQuery(id+"F4.wireOp",EDGE,"E123.0"),sQuery(id+"F4.wireOp",EDGE,"E124.0"),subQ43,sQuery(id+"F4.wireOp",EDGE,"E238.trimOffspring"),sQuery(id+"F4.wireOp",EDGE,"E239.trimOffspring")])],"isStart":true}),makeQuery(id+"F6.opExtrude","CAP_FACE",FACE,{"disambiguationData":[OSD([subQ65,subQ64,sQuery(id+"F4.wireOp",EDGE,"E117.0"),sQuery(id+"F4.wireOp",EDGE,"E118.0"),subQ45,sQuery(id+"F4.wireOp",EDGE,"E236.trimOffspring"),sQuery(id+"F4.wireOp",EDGE,"E237.trimOffspring")])],"isStart":true})]}),makeQuery(id+"F7.opExtrude","CAP_FACE",FACE,{"disambiguationData":[OSD([sQuery(id+"F4.wireOp",EDGE,"E74.0"),subQ63,subQ62,sQuery(id+"F4.wireOp",EDGE,"E148.trimOffspring"),subQ31,sQuery(id+"F4.wireOp",EDGE,"E253.0"),sQuery(id+"F4.wireOp",EDGE,"E254.0")])],"isStart":true}),makeQuery(id+"F7.opExtrude","CAP_FACE",FACE,{"disambiguationData":[OSD([subQ63,subQ62,subQ10,sQuery(id+"F4.wireOp",EDGE,"E193.trimOffspring"),sQuery(id+"F4.wireOp",EDGE,"E194.trimOffspring"),subQ9,sQuery(id+"F4.wireOp",EDGE,"E277.trimOffspring"),sQuery(id+"F4.wireOp",EDGE,"E278.trimOffspring")])],"isStart":true}),makeQuery(id+"F7.opExtrude","CAP_FACE",FACE,{"disambiguationData":[OSD([subQ63,subQ62,subQ12,sQuery(id+"F4.wireOp",EDGE,"E189.trimOffspring"),subQ11,sQuery(id+"F4.wireOp",EDGE,"E191.trimOffspring"),sQuery(id+"F4.wireOp",EDGE,"E275.trimOffspring"),sQuery(id+"F4.wireOp",EDGE,"E276.trimOffspring")])],"isStart":true}),makeQuery(id+"F7.opExtrude","CAP_FACE",FACE,{"disambiguationData":[OSD([subQ63,subQ62,subQ14,sQuery(id+"F4.wireOp",EDGE,"E185.trimOffspring"),sQuery(id+"F4.wireOp",EDGE,"E186.trimOffspring"),subQ13,sQuery(id+"F4.wireOp",EDGE,"E273.trimOffspring"),sQuery(id+"F4.wireOp",EDGE,"E274.trimOffspring")])],"isStart":true}),makeQuery(id+"F7.opExtrude","CAP_FACE",FACE,{"disambiguationData":[OSD([subQ63,subQ62,subQ16,sQuery(id+"F4.wireOp",EDGE,"E181.trimOffspring"),sQuery(id+"F4.wireOp",EDGE,"E182.trimOffspring"),subQ15,sQuery(id+"F4.wireOp",EDGE,"E271.trimOffspring"),sQuery(id+"F4.wireOp",EDGE,"E272.trimOffspring")])],"isStart":true}),makeQuery(id+"F7.opExtrude","CAP_FACE",FACE,{"disambiguationData":[OSD([subQ63,subQ62,subQ18,sQuery(id+"F4.wireOp",EDGE,"E177.trimOffspring"),sQuery(id+"F4.wireOp",EDGE,"E178.trimOffspring"),subQ17,sQuery(id+"F4.wireOp",EDGE,"E269.trimOffspring"),sQuery(id+"F4.wireOp",EDGE,"E270.trimOffspring")])],"isStart":true}),makeQuery(id+"F7.opExtrude","CAP_FACE",FACE,{"disambiguationData":[OSD([subQ63,subQ62,sQuery(id+"F4.wireOp",EDGE,"E119.trimOffspring"),subQ47,sQuery(id+"F4.wireOp",EDGE,"E174.trimOffspring"),subQ19,sQuery(id+"F4.wireOp",EDGE,"E267.trimOffspring"),sQuery(id+"F4.wireOp",EDGE,"E268.trimOffspring")])],"isStart":true}),makeQuery(id+"F7.opExtrude","CAP_FACE",FACE,{"disambiguationData":[OSD([subQ63,subQ62,subQ20,sQuery(id+"F4.wireOp",EDGE,"E171.trimOffspring"),sQuery(id+"F4.wireOp",EDGE,"E172.trimOffspring"),subQ46,sQuery(id+"F4.wireOp",EDGE,"E265.trimOffspring"),sQuery(id+"F4.wireOp",EDGE,"E266.trimOffspring")])],"isStart":true}),makeQuery(id+"F7.opExtrude","CAP_FACE",FACE,{"disambiguationData":[OSD([subQ63,subQ62,subQ22,sQuery(id+"F4.wireOp",EDGE,"E167.trimOffspring"),sQuery(id+"F4.wireOp",EDGE,"E168.trimOffspring"),subQ21,sQuery(id+"F4.wireOp",EDGE,"E263.trimOffspring"),sQuery(id+"F4.wireOp",EDGE,"E264.trimOffspring")])],"isStart":true}),makeQuery(id+"F7.opExtrude","CAP_FACE",FACE,{"disambiguationData":[OSD([subQ63,subQ62,subQ24,sQuery(id+"F4.wireOp",EDGE,"E163.trimOffspring"),sQuery(id+"F4.wireOp",EDGE,"E164.trimOffspring"),subQ23,sQuery(id+"F4.wireOp",EDGE,"E261.trimOffspring"),sQuery(id+"F4.wireOp",EDGE,"E262.trimOffspring")])],"isStart":true}),makeQuery(id+"F7.opExtrude","CAP_FACE",FACE,{"disambiguationData":[OSD([subQ63,subQ62,sQuery(id+"F4.wireOp",EDGE,"E158.trimOffspring"),subQ26,subQ25,sQuery(id+"F4.wireOp",EDGE,"E161.trimOffspring"),sQuery(id+"F4.wireOp",EDGE,"E259.trimOffspring"),sQuery(id+"F4.wireOp",EDGE,"E260.trimOffspring")])],"isStart":true}),makeQuery(id+"F7.opExtrude","CAP_FACE",FACE,{"disambiguationData":[OSD([subQ63,subQ62,subQ28,sQuery(id+"F4.wireOp",EDGE,"E155.trimOffspring"),sQuery(id+"F4.wireOp",EDGE,"E156.trimOffspring"),subQ27,sQuery(id+"F4.wireOp",EDGE,"E257.trimOffspring"),sQuery(id+"F4.wireOp",EDGE,"E258.trimOffspring")])],"isStart":true}),makeQuery(id+"F7.opExtrude","CAP_FACE",FACE,{"disambiguationData":[OSD([subQ63,subQ62,subQ30,sQuery(id+"F4.wireOp",EDGE,"E151.trimOffspring"),sQuery(id+"F4.wireOp",EDGE,"E152.trimOffspring"),subQ29,sQuery(id+"F4.wireOp",EDGE,"E255.trimOffspring"),sQuery(id+"F4.wireOp",EDGE,"E256.trimOffspring")])],"isStart":true})]}),makeQuery(id+"F8.opExtrude","CAP_FACE",FACE,{"disambiguationData":[OSD([subQ63,subQ62,sQuery(id+"F4.wireOp",EDGE,"E77.0"),sQuery(id+"F4.wireOp",EDGE,"E212.trimOffspring"),subQ0,sQuery(id+"F4.wireOp",EDGE,"E287.trimOffspring"),sQuery(id+"F4.wireOp",EDGE,"E288.trimOffspring")])],"isStart":true}),makeQuery(id+"F8.opExtrude","CAP_FACE",FACE,{"disambiguationData":[OSD([subQ63,subQ62,subQ2,sQuery(id+"F4.wireOp",EDGE,"E209.trimOffspring"),sQuery(id+"F4.wireOp",EDGE,"E210.trimOffspring"),subQ1,sQuery(id+"F4.wireOp",EDGE,"E285.trimOffspring"),sQuery(id+"F4.wireOp",EDGE,"E286.trimOffspring")])],"isStart":true}),makeQuery(id+"F8.opExtrude","CAP_FACE",FACE,{"disambiguationData":[OSD([subQ63,subQ62,subQ4,sQuery(id+"F4.wireOp",EDGE,"E205.trimOffspring"),subQ3,sQuery(id+"F4.wireOp",EDGE,"E207.trimOffspring"),sQuery(id+"F4.wireOp",EDGE,"E283.trimOffspring"),sQuery(id+"F4.wireOp",EDGE,"E284.trimOffspring")])],"isStart":true}),makeQuery(id+"F8.opExtrude","CAP_FACE",FACE,{"disambiguationData":[OSD([subQ63,subQ62,sQuery(id+"F4.wireOp",EDGE,"E200.trimOffspring"),subQ6,sQuery(id+"F4.wireOp",EDGE,"E202.trimOffspring"),subQ5,sQuery(id+"F4.wireOp",EDGE,"E281.trimOffspring"),sQuery(id+"F4.wireOp",EDGE,"E282.trimOffspring")])],"isStart":true}),makeQuery(id+"F8.opExtrude","CAP_FACE",FACE,{"disambiguationData":[OSD([subQ63,subQ62,sQuery(id+"F4.wireOp",EDGE,"E196.trimOffspring"),subQ8,subQ7,sQuery(id+"F4.wireOp",EDGE,"E199.trimOffspring"),sQuery(id+"F4.wireOp",EDGE,"E279.trimOffspring"),sQuery(id+"F4.wireOp",EDGE,"E280.trimOffspring")])],"isStart":true})]}),makeQuery(id+"F9.opExtrude","CAP_FACE",FACE,{"disambiguationData":[OSD([subQ61,subQ60,sQuery(id+"F4.wireOp",EDGE,"E289"),sQuery(id+"F4.wireOp",EDGE,"E290")])],"isStart":true}),makeQuery(id+"F9.opExtrude","CAP_FACE",FACE,{"disambiguationData":[OSD([subQ59,subQ58,sQuery(id+"F4.wireOp",EDGE,"E291"),sQuery(id+"F4.wireOp",EDGE,"E292")])],"isStart":true}),makeQuery(id+"F9.opExtrude","CAP_FACE",FACE,{"disambiguationData":[OSD([subQ57,subQ56,sQuery(id+"F4.wireOp",EDGE,"E293"),sQuery(id+"F4.wireOp",EDGE,"E294")])],"isStart":true}),makeQuery(id+"F9.opExtrude","CAP_FACE",FACE,{"disambiguationData":[OSD([subQ55,subQ54,sQuery(id+"F4.wireOp",EDGE,"E295"),sQuery(id+"F4.wireOp",EDGE,"E296")])],"isStart":true}),makeQuery(id+"F9.opExtrude","CAP_FACE",FACE,{"disambiguationData":[OSD([subQ53,subQ52,sQuery(id+"F4.wireOp",EDGE,"E297"),sQuery(id+"F4.wireOp",EDGE,"E298")])],"isStart":true}),makeQuery(id+"F9.opExtrude","CAP_FACE",FACE,{"disambiguationData":[OSD([subQ51,subQ50,sQuery(id+"F4.wireOp",EDGE,"E299"),sQuery(id+"F4.wireOp",EDGE,"E300")])],"isStart":true}),makeQuery(id+"F9.opExtrude","CAP_FACE",FACE,{"disambiguationData":[OSD([subQ49,sQuery(id+"F4.wireOp",EDGE,"E301"),subQ48,sQuery(id+"F4.wireOp",EDGE,"E303")])],"isStart":true}),makeQuery(id+"F9.opExtrude","CAP_FACE",FACE,{"disambiguationData":[OSD([subQ47,subQ46,sQuery(id+"F4.wireOp",EDGE,"E316"),sQuery(id+"F4.wireOp",EDGE,"E317")])],"isStart":true}),makeQuery(id+"F9.opExtrude","CAP_FACE",FACE,{"disambiguationData":[OSD([subQ45,subQ44,sQuery(id+"F4.wireOp",EDGE,"E338"),sQuery(id+"F4.wireOp",EDGE,"E339")])],"isStart":true}),makeQuery(id+"F9.opExtrude","CAP_FACE",FACE,{"disambiguationData":[OSD([subQ43,subQ42,sQuery(id+"F4.wireOp",EDGE,"E340"),sQuery(id+"F4.wireOp",EDGE,"E341")])],"isStart":true}),makeQuery(id+"F9.opExtrude","CAP_FACE",FACE,{"disambiguationData":[OSD([subQ41,subQ40,sQuery(id+"F4.wireOp",EDGE,"E342"),sQuery(id+"F4.wireOp",EDGE,"E343")])],"isStart":true}),makeQuery(id+"F9.opExtrude","CAP_FACE",FACE,{"disambiguationData":[OSD([subQ39,subQ38,sQuery(id+"F4.wireOp",EDGE,"E344"),sQuery(id+"F4.wireOp",EDGE,"E345")])],"isStart":true}),makeQuery(id+"F9.opExtrude","CAP_FACE",FACE,{"disambiguationData":[OSD([subQ37,subQ36,sQuery(id+"F4.wireOp",EDGE,"E346"),sQuery(id+"F4.wireOp",EDGE,"E347")])],"isStart":true}),makeQuery(id+"F9.opExtrude","CAP_FACE",FACE,{"disambiguationData":[OSD([subQ35,subQ34,sQuery(id+"F4.wireOp",EDGE,"E348"),sQuery(id+"F4.wireOp",EDGE,"E349")])],"isStart":true}),makeQuery(id+"F9.opExtrude","CAP_FACE",FACE,{"disambiguationData":[OSD([subQ33,subQ32,sQuery(id+"F4.wireOp",EDGE,"E350"),sQuery(id+"F4.wireOp",EDGE,"E351")])],"isStart":true}),makeQuery(id+"F9.opExtrude","CAP_FACE",FACE,{"disambiguationData":[OSD([subQ31,subQ30,sQuery(id+"F4.wireOp",EDGE,"E304"),sQuery(id+"F4.wireOp",EDGE,"E305")])],"isStart":true}),makeQuery(id+"F9.opExtrude","CAP_FACE",FACE,{"disambiguationData":[OSD([subQ29,subQ28,sQuery(id+"F4.wireOp",EDGE,"E306"),sQuery(id+"F4.wireOp",EDGE,"E307")])],"isStart":true}),makeQuery(id+"F9.opExtrude","CAP_FACE",FACE,{"disambiguationData":[OSD([subQ27,subQ26,sQuery(id+"F4.wireOp",EDGE,"E308"),sQuery(id+"F4.wireOp",EDGE,"E309")])],"isStart":true}),makeQuery(id+"F9.opExtrude","CAP_FACE",FACE,{"disambiguationData":[OSD([subQ25,subQ24,sQuery(id+"F4.wireOp",EDGE,"E310"),sQuery(id+"F4.wireOp",EDGE,"E311")])],"isStart":true}),makeQuery(id+"F9.opExtrude","CAP_FACE",FACE,{"disambiguationData":[OSD([subQ23,subQ22,sQuery(id+"F4.wireOp",EDGE,"E312"),sQuery(id+"F4.wireOp",EDGE,"E313")])],"isStart":true}),makeQuery(id+"F9.opExtrude","CAP_FACE",FACE,{"disambiguationData":[OSD([subQ21,subQ20,sQuery(id+"F4.wireOp",EDGE,"E314"),sQuery(id+"F4.wireOp",EDGE,"E315")])],"isStart":true}),makeQuery(id+"F9.opExtrude","CAP_FACE",FACE,{"disambiguationData":[OSD([subQ19,subQ18,sQuery(id+"F4.wireOp",EDGE,"E318"),sQuery(id+"F4.wireOp",EDGE,"E319")])],"isStart":true}),makeQuery(id+"F9.opExtrude","CAP_FACE",FACE,{"disambiguationData":[OSD([subQ17,subQ16,sQuery(id+"F4.wireOp",EDGE,"E320"),sQuery(id+"F4.wireOp",EDGE,"E321")])],"isStart":true}),makeQuery(id+"F9.opExtrude","CAP_FACE",FACE,{"disambiguationData":[OSD([subQ15,subQ14,sQuery(id+"F4.wireOp",EDGE,"E322"),sQuery(id+"F4.wireOp",EDGE,"E323")])],"isStart":true}),makeQuery(id+"F9.opExtrude","CAP_FACE",FACE,{"disambiguationData":[OSD([subQ13,subQ12,sQuery(id+"F4.wireOp",EDGE,"E324"),sQuery(id+"F4.wireOp",EDGE,"E325")])],"isStart":true}),makeQuery(id+"F9.opExtrude","CAP_FACE",FACE,{"disambiguationData":[OSD([subQ11,subQ10,sQuery(id+"F4.wireOp",EDGE,"E326"),sQuery(id+"F4.wireOp",EDGE,"E327")])],"isStart":true}),makeQuery(id+"F9.opExtrude","CAP_FACE",FACE,{"disambiguationData":[OSD([subQ9,subQ8,sQuery(id+"F4.wireOp",EDGE,"E328"),sQuery(id+"F4.wireOp",EDGE,"E329")])],"isStart":true}),makeQuery(id+"F9.opExtrude","CAP_FACE",FACE,{"disambiguationData":[OSD([subQ7,subQ6,sQuery(id+"F4.wireOp",EDGE,"E330"),sQuery(id+"F4.wireOp",EDGE,"E331")])],"isStart":true}),makeQuery(id+"F9.opExtrude","CAP_FACE",FACE,{"disambiguationData":[OSD([subQ5,subQ4,sQuery(id+"F4.wireOp",EDGE,"E332"),sQuery(id+"F4.wireOp",EDGE,"E333")])],"isStart":true}),makeQuery(id+"F9.opExtrude","CAP_FACE",FACE,{"disambiguationData":[OSD([subQ3,subQ2,sQuery(id+"F4.wireOp",EDGE,"E334"),sQuery(id+"F4.wireOp",EDGE,"E335")])],"isStart":true}),makeQuery(id+"F9.opExtrude","CAP_FACE",FACE,{"disambiguationData":[OSD([subQ1,subQ0,sQuery(id+"F4.wireOp",EDGE,"E336"),sQuery(id+"F4.wireOp",EDGE,"E337")])],"isStart":true})]});}
            var sketch = newSketch(context, id + "F10", { "sketchPlane" : qUnion([Q0])});
            skLineSegment(sketch, "E352", {"start": v(279.4, -812) * mm, "end": v(279.4, -850.1) * mm, "construction": true});
            skLineSegment(sketch, "E353", {"start": v(-279.4, -812) * mm, "end": v(-279.4, -850.1) * mm, "construction": true});
            skLineSegment(sketch, "E354", {"start": v(-279.4, -831.06) * mm, "end": v(279.4, -831.06) * mm, "construction": true});
            skLineSegment(sketch, "E355", {"start": v(-279.4, -1476.38) * mm, "end": v(-317.5, -1476.38) * mm, "construction": true});
            skLineSegment(sketch, "E356", {"start": v(-298.45, -1476.38) * mm, "end": v(-298.45, 479.43) * mm, "construction": true});
            skLineSegment(sketch, "E357", {"start": v(-298.45, -165.9) * mm, "end": v(298.45, -165.9) * mm, "construction": true});
            skLineSegment(sketch, "E358", {"start": v(-438.15, 498.48) * mm, "end": v(434.98, 498.47) * mm, "construction": true});
            skLineSegment(sketch, "E359", {"start": v(298.45, -165.9) * mm, "end": v(298.45, -352.42) * mm, "construction": true});
            skLineSegment(sketch, "E360", {"start": v(298.45, -165.9) * mm, "end": v(298.45, 498.47) * mm, "construction": true});
            skLineSegment(sketch, "E361", {"start": v(-438.15, 498.48) * mm, "end": v(-438.15, -1495.43) * mm, "construction": true});
            skLineSegment(sketch, "E362", {"start": v(-438.15, -1495.43) * mm, "end": v(434.98, -1495.43) * mm, "construction": true});
            skLineSegment(sketch, "E363", {"start": v(434.98, -1495.43) * mm, "end": v(434.98, -644.52) * mm, "construction": true});
            skLineSegment(sketch, "E364", {"start": v(434.98, 498.47) * mm, "end": v(434.98, -352.42) * mm, "construction": true});
            skLineSegment(sketch, "E365", {"start": v(298.45, -1495.43) * mm, "end": v(298.45, -644.52) * mm, "construction": true});
            skCircle(sketch, "E366", {"center": v(-298.45, -831.06) * mm, "radius": 1.59 * mm});
            skCircle(sketch, "E367", {"center": v(0, -831.06) * mm, "radius": 4.76 * mm});
            skCircle(sketch, "E368", {"center": v(298.45, -831.06) * mm, "radius": 4.76 * mm});
            skCircle(sketch, "E369", {"center": v(-298.45, -831.06) * mm, "radius": 4.76 * mm});
            skCircle(sketch, "E370", {"center": v(0, -831.06) * mm, "radius": 1.59 * mm});
            skCircle(sketch, "E371", {"center": v(298.45, -831.06) * mm, "radius": 1.59 * mm});
            skCircle(sketch, "E372", {"center": v(298.45, -644.52) * mm, "radius": 1.59 * mm});
            skCircle(sketch, "E373", {"center": v(298.45, -644.52) * mm, "radius": 4.76 * mm});
            skCircle(sketch, "E374", {"center": v(434.98, -644.52) * mm, "radius": 4.76 * mm});
            skCircle(sketch, "E375", {"center": v(434.98, -644.52) * mm, "radius": 1.59 * mm});
            skCircle(sketch, "E376", {"center": v(-298.45, -1495.43) * mm, "radius": 4.76 * mm});
            skCircle(sketch, "E377", {"center": v(-298.45, -1495.43) * mm, "radius": 1.59 * mm});
            skCircle(sketch, "E378", {"center": v(-1.59, -1495.43) * mm, "radius": 4.76 * mm});
            skCircle(sketch, "E379", {"center": v(-1.59, -1495.43) * mm, "radius": 1.59 * mm});
            skCircle(sketch, "E380", {"center": v(298.45, -1495.43) * mm, "radius": 4.76 * mm});
            skCircle(sketch, "E381", {"center": v(298.45, -1495.43) * mm, "radius": 1.59 * mm});
            skCircle(sketch, "E382", {"center": v(434.98, -1495.43) * mm, "radius": 4.76 * mm});
            skCircle(sketch, "E383", {"center": v(434.98, -1495.43) * mm, "radius": 1.59 * mm});
            skLineSegment(sketch, "E384", {"start": v(-438.15, -1163.24) * mm, "end": v(434.98, -1163.24) * mm, "construction": true});
            skPoint(sketch, "E384.startSnap0", {"position": v(-279.4, -1163.24) * mm});
            skLineSegment(sketch, "E385", {"start": v(-279.4, -498.48) * mm, "end": v(-438.15, -498.48) * mm, "construction": true});
            skLineSegment(sketch, "E386", {"start": v(-438.15, 166.3) * mm, "end": v(434.98, 166.3) * mm, "construction": true});
            skPoint(sketch, "E386.startSnap0", {"position": v(-279.4, 166.3) * mm});
            skCircle(sketch, "E387", {"center": v(298.45, 166.3) * mm, "radius": 4.76 * mm});
            skCircle(sketch, "E388", {"center": v(434.98, 166.3) * mm, "radius": 4.76 * mm});
            skCircle(sketch, "E389", {"center": v(434.98, 166.3) * mm, "radius": 1.59 * mm});
            skCircle(sketch, "E390", {"center": v(298.45, -165.9) * mm, "radius": 4.76 * mm});
            skCircle(sketch, "E391", {"center": v(298.45, -165.9) * mm, "radius": 1.59 * mm});
            skCircle(sketch, "E392", {"center": v(434.98, -165.9) * mm, "radius": 4.76 * mm});
            skCircle(sketch, "E393", {"center": v(434.98, -165.9) * mm, "radius": 1.59 * mm});
            skCircle(sketch, "E394", {"center": v(434.98, -352.42) * mm, "radius": 4.76 * mm});
            skCircle(sketch, "E395", {"center": v(434.98, -352.42) * mm, "radius": 1.59 * mm});
            skCircle(sketch, "E396", {"center": v(298.45, -352.42) * mm, "radius": 4.76 * mm});
            skCircle(sketch, "E397", {"center": v(298.45, -352.42) * mm, "radius": 1.59 * mm});
            skCircle(sketch, "E398", {"center": v(298.45, 498.47) * mm, "radius": 4.76 * mm});
            skCircle(sketch, "E399", {"center": v(298.45, 498.47) * mm, "radius": 1.59 * mm});
            skCircle(sketch, "E400", {"center": v(434.98, 498.47) * mm, "radius": 4.76 * mm});
            skCircle(sketch, "E401", {"center": v(434.98, 498.47) * mm, "radius": 1.59 * mm});
            skCircle(sketch, "E402", {"center": v(-1.59, 498.47) * mm, "radius": 4.76 * mm});
            skCircle(sketch, "E403", {"center": v(-1.59, 498.47) * mm, "radius": 1.59 * mm});
            skCircle(sketch, "E404", {"center": v(-298.45, 498.48) * mm, "radius": 4.76 * mm});
            skCircle(sketch, "E405", {"center": v(-438.15, 498.48) * mm, "radius": 4.76 * mm});
            skCircle(sketch, "E406", {"center": v(-298.45, 498.48) * mm, "radius": 1.59 * mm});
            skCircle(sketch, "E407", {"center": v(-438.15, 498.48) * mm, "radius": 1.59 * mm});
            skCircle(sketch, "E408", {"center": v(-298.45, 166.3) * mm, "radius": 4.76 * mm});
            skCircle(sketch, "E409", {"center": v(-438.15, 166.3) * mm, "radius": 4.76 * mm});
            skCircle(sketch, "E410", {"center": v(-438.15, 166.3) * mm, "radius": 1.59 * mm});
            skCircle(sketch, "E411", {"center": v(-298.45, 166.3) * mm, "radius": 1.59 * mm});
            skCircle(sketch, "E412", {"center": v(-298.45, -165.9) * mm, "radius": 4.76 * mm});
            skCircle(sketch, "E413", {"center": v(-298.45, -165.9) * mm, "radius": 1.59 * mm});
            skCircle(sketch, "E414", {"center": v(0, -165.9) * mm, "radius": 4.76 * mm});
            skCircle(sketch, "E415", {"center": v(0, -165.9) * mm, "radius": 1.59 * mm});
            skCircle(sketch, "E416", {"center": v(-438.15, -165.9) * mm, "radius": 4.76 * mm});
            skCircle(sketch, "E417", {"center": v(-438.15, -165.9) * mm, "radius": 1.59 * mm});
            skCircle(sketch, "E418", {"center": v(-298.45, -498.47) * mm, "radius": 4.76 * mm});
            skCircle(sketch, "E419", {"center": v(-438.15, -498.48) * mm, "radius": 4.76 * mm});
            skCircle(sketch, "E420", {"center": v(-438.15, -498.48) * mm, "radius": 1.59 * mm});
            skCircle(sketch, "E421", {"center": v(-298.45, -498.47) * mm, "radius": 1.59 * mm});
            skCircle(sketch, "E422", {"center": v(-438.15, -831.06) * mm, "radius": 4.76 * mm});
            skCircle(sketch, "E423", {"center": v(-438.15, -831.06) * mm, "radius": 1.59 * mm});
            skCircle(sketch, "E424", {"center": v(434.98, -831.06) * mm, "radius": 4.76 * mm});
            skCircle(sketch, "E425", {"center": v(434.98, -831.06) * mm, "radius": 1.59 * mm});
            skCircle(sketch, "E426", {"center": v(298.45, -1163.24) * mm, "radius": 4.76 * mm});
            skCircle(sketch, "E427", {"center": v(298.45, -1163.24) * mm, "radius": 1.59 * mm});
            skCircle(sketch, "E428", {"center": v(434.98, -1163.24) * mm, "radius": 4.76 * mm});
            skCircle(sketch, "E429", {"center": v(434.98, -1163.24) * mm, "radius": 1.59 * mm});
            skCircle(sketch, "E430", {"center": v(-438.15, -1163.24) * mm, "radius": 4.76 * mm});
            skCircle(sketch, "E431", {"center": v(-438.15, -1163.24) * mm, "radius": 1.59 * mm});
            skCircle(sketch, "E432", {"center": v(-298.45, -1163.24) * mm, "radius": 4.76 * mm});
            skCircle(sketch, "E433", {"center": v(-298.45, -1163.24) * mm, "radius": 1.59 * mm});
            skCircle(sketch, "E434", {"center": v(-438.15, -1495.43) * mm, "radius": 4.76 * mm});
            skCircle(sketch, "E435", {"center": v(-438.15, -1495.43) * mm, "radius": 1.59 * mm});
            skCircle(sketch, "E436", {"center": v(298.45, 166.3) * mm, "radius": 1.59 * mm});
            skSolve(sketch);
        }
        {
            var Q0;
            Q0=makeQuery(id+"F10.imprint","IMPRINT",FACE,{"disambiguationData":[TD([[makeQuery(id+"F10.imprint","IMPRINT",EDGE,{"derivedFrom":sQuery(id+"F10.wireOp",EDGE,"E411")}),1.0]])]});
            var Q1;
            Q1=makeQuery(id+"F10.imprint","IMPRINT",FACE,{"disambiguationData":[TD([[makeQuery(id+"F10.imprint","IMPRINT",EDGE,{"derivedFrom":sQuery(id+"F10.wireOp",EDGE,"E410")}),1.0]])]});
            var Q2;
            Q2=makeQuery(id+"F10.imprint","IMPRINT",FACE,{"disambiguationData":[TD([[makeQuery(id+"F10.imprint","IMPRINT",EDGE,{"derivedFrom":sQuery(id+"F10.wireOp",EDGE,"E413")}),1.0]])]});
            var Q3;
            Q3=makeQuery(id+"F10.imprint","IMPRINT",FACE,{"disambiguationData":[TD([[makeQuery(id+"F10.imprint","IMPRINT",EDGE,{"derivedFrom":sQuery(id+"F10.wireOp",EDGE,"E417")}),1.0]])]});
            var Q4;
            Q4=makeQuery(id+"F10.imprint","IMPRINT",FACE,{"disambiguationData":[TD([[makeQuery(id+"F10.imprint","IMPRINT",EDGE,{"derivedFrom":sQuery(id+"F10.wireOp",EDGE,"E420")}),1.0]])]});
            var Q5;
            Q5=makeQuery(id+"F10.imprint","IMPRINT",FACE,{"disambiguationData":[TD([[makeQuery(id+"F10.imprint","IMPRINT",EDGE,{"derivedFrom":sQuery(id+"F10.wireOp",EDGE,"E421")}),1.0]])]});
            var Q6;
            Q6=makeQuery(id+"F10.imprint","IMPRINT",FACE,{"disambiguationData":[TD([[makeQuery(id+"F10.imprint","IMPRINT",EDGE,{"derivedFrom":sQuery(id+"F10.wireOp",EDGE,"E423")}),1.0]])]});
            var Q7;
            Q7=makeQuery(id+"F10.imprint","IMPRINT",FACE,{"disambiguationData":[TD([[makeQuery(id+"F10.imprint","IMPRINT",EDGE,{"derivedFrom":sQuery(id+"F10.wireOp",EDGE,"E366")}),1.0]])]});
            var Q8;
            Q8=makeQuery(id+"F10.imprint","IMPRINT",FACE,{"disambiguationData":[TD([[makeQuery(id+"F10.imprint","IMPRINT",EDGE,{"derivedFrom":sQuery(id+"F10.wireOp",EDGE,"E431")}),1.0]])]});
            var Q9;
            Q9=makeQuery(id+"F10.imprint","IMPRINT",FACE,{"disambiguationData":[TD([[makeQuery(id+"F10.imprint","IMPRINT",EDGE,{"derivedFrom":sQuery(id+"F10.wireOp",EDGE,"E433")}),1.0]])]});
            var Q10;
            Q10=makeQuery(id+"F10.imprint","IMPRINT",FACE,{"disambiguationData":[TD([[makeQuery(id+"F10.imprint","IMPRINT",EDGE,{"derivedFrom":sQuery(id+"F10.wireOp",EDGE,"E435")}),1.0]])]});
            var Q11;
            Q11=makeQuery(id+"F10.imprint","IMPRINT",FACE,{"disambiguationData":[TD([[makeQuery(id+"F10.imprint","IMPRINT",EDGE,{"derivedFrom":sQuery(id+"F10.wireOp",EDGE,"E377")}),1.0]])]});
            var Q12;
            Q12=makeQuery(id+"F10.imprint","IMPRINT",FACE,{"disambiguationData":[TD([[makeQuery(id+"F10.imprint","IMPRINT",EDGE,{"derivedFrom":sQuery(id+"F10.wireOp",EDGE,"E379")}),1.0]])]});
            var Q13;
            Q13=makeQuery(id+"F10.imprint","IMPRINT",FACE,{"disambiguationData":[TD([[makeQuery(id+"F10.imprint","IMPRINT",EDGE,{"derivedFrom":sQuery(id+"F10.wireOp",EDGE,"E381")}),1.0]])]});
            var Q14;
            Q14=makeQuery(id+"F10.imprint","IMPRINT",FACE,{"disambiguationData":[TD([[makeQuery(id+"F10.imprint","IMPRINT",EDGE,{"derivedFrom":sQuery(id+"F10.wireOp",EDGE,"E383")}),1.0]])]});
            var Q15;
            Q15=makeQuery(id+"F10.imprint","IMPRINT",FACE,{"disambiguationData":[TD([[makeQuery(id+"F10.imprint","IMPRINT",EDGE,{"derivedFrom":sQuery(id+"F10.wireOp",EDGE,"E427")}),1.0]])]});
            var Q16;
            Q16=makeQuery(id+"F10.imprint","IMPRINT",FACE,{"disambiguationData":[TD([[makeQuery(id+"F10.imprint","IMPRINT",EDGE,{"derivedFrom":sQuery(id+"F10.wireOp",EDGE,"E429")}),1.0]])]});
            var Q17;
            Q17=makeQuery(id+"F10.imprint","IMPRINT",FACE,{"disambiguationData":[TD([[makeQuery(id+"F10.imprint","IMPRINT",EDGE,{"derivedFrom":sQuery(id+"F10.wireOp",EDGE,"E371")}),1.0]])]});
            var Q18;
            Q18=makeQuery(id+"F10.imprint","IMPRINT",FACE,{"disambiguationData":[TD([[makeQuery(id+"F10.imprint","IMPRINT",EDGE,{"derivedFrom":sQuery(id+"F10.wireOp",EDGE,"E425")}),1.0]])]});
            var Q19;
            Q19=makeQuery(id+"F10.imprint","IMPRINT",FACE,{"disambiguationData":[TD([[makeQuery(id+"F10.imprint","IMPRINT",EDGE,{"derivedFrom":sQuery(id+"F10.wireOp",EDGE,"E370")}),1.0]])]});
            var Q20;
            Q20=makeQuery(id+"F10.imprint","IMPRINT",FACE,{"disambiguationData":[TD([[makeQuery(id+"F10.imprint","IMPRINT",EDGE,{"derivedFrom":sQuery(id+"F10.wireOp",EDGE,"E372")}),1.0]])]});
            var Q21;
            Q21=makeQuery(id+"F10.imprint","IMPRINT",FACE,{"disambiguationData":[TD([[makeQuery(id+"F10.imprint","IMPRINT",EDGE,{"derivedFrom":sQuery(id+"F10.wireOp",EDGE,"E375")}),1.0]])]});
            var Q22;
            Q22=makeQuery(id+"F10.imprint","IMPRINT",FACE,{"disambiguationData":[TD([[makeQuery(id+"F10.imprint","IMPRINT",EDGE,{"derivedFrom":sQuery(id+"F10.wireOp",EDGE,"E397")}),1.0]])]});
            var Q23;
            Q23=makeQuery(id+"F10.imprint","IMPRINT",FACE,{"disambiguationData":[TD([[makeQuery(id+"F10.imprint","IMPRINT",EDGE,{"derivedFrom":sQuery(id+"F10.wireOp",EDGE,"E395")}),1.0]])]});
            var Q24;
            Q24=makeQuery(id+"F10.imprint","IMPRINT",FACE,{"disambiguationData":[TD([[makeQuery(id+"F10.imprint","IMPRINT",EDGE,{"derivedFrom":sQuery(id+"F10.wireOp",EDGE,"E393")}),1.0]])]});
            var Q25;
            Q25=makeQuery(id+"F10.imprint","IMPRINT",FACE,{"disambiguationData":[TD([[makeQuery(id+"F10.imprint","IMPRINT",EDGE,{"derivedFrom":sQuery(id+"F10.wireOp",EDGE,"E391")}),1.0]])]});
            var Q26;
            Q26=makeQuery(id+"F10.imprint","IMPRINT",FACE,{"disambiguationData":[TD([[makeQuery(id+"F10.imprint","IMPRINT",EDGE,{"derivedFrom":sQuery(id+"F10.wireOp",EDGE,"E415")}),1.0]])]});
            var Q27;
            Q27=makeQuery(id+"F10.imprint","IMPRINT",FACE,{"disambiguationData":[TD([[makeQuery(id+"F10.imprint","IMPRINT",EDGE,{"derivedFrom":sQuery(id+"F10.wireOp",EDGE,"E436")}),1.0]])]});
            var Q28;
            Q28=makeQuery(id+"F10.imprint","IMPRINT",FACE,{"disambiguationData":[TD([[makeQuery(id+"F10.imprint","IMPRINT",EDGE,{"derivedFrom":sQuery(id+"F10.wireOp",EDGE,"E389")}),1.0]])]});
            var Q29;
            Q29=makeQuery(id+"F10.imprint","IMPRINT",FACE,{"disambiguationData":[TD([[makeQuery(id+"F10.imprint","IMPRINT",EDGE,{"derivedFrom":sQuery(id+"F10.wireOp",EDGE,"E399")}),1.0]])]});
            var Q30;
            Q30=makeQuery(id+"F10.imprint","IMPRINT",FACE,{"disambiguationData":[TD([[makeQuery(id+"F10.imprint","IMPRINT",EDGE,{"derivedFrom":sQuery(id+"F10.wireOp",EDGE,"E401")}),1.0]])]});
            var Q31;
            Q31=makeQuery(id+"F10.imprint","IMPRINT",FACE,{"disambiguationData":[TD([[makeQuery(id+"F10.imprint","IMPRINT",EDGE,{"derivedFrom":sQuery(id+"F10.wireOp",EDGE,"E403")}),1.0]])]});
            var Q32;
            Q32=makeQuery(id+"F10.imprint","IMPRINT",FACE,{"disambiguationData":[TD([[makeQuery(id+"F10.imprint","IMPRINT",EDGE,{"derivedFrom":sQuery(id+"F10.wireOp",EDGE,"E406")}),1.0]])]});
            var Q33;
            Q33=makeQuery(id+"F10.imprint","IMPRINT",FACE,{"disambiguationData":[TD([[makeQuery(id+"F10.imprint","IMPRINT",EDGE,{"derivedFrom":sQuery(id+"F10.wireOp",EDGE,"E407")}),1.0]])]});
            extrude(context, id + "F11", {"entities" : qUnion([Q0, Q1, Q2, Q3, Q4, Q5, Q6, Q7, Q8, Q9, Q10, Q11, Q12, Q13, Q14, Q15, Q16, Q17, Q18, Q19, Q20, Q21, Q22, Q23, Q24, Q25, Q26, Q27, Q28, Q29, Q30, Q31, Q32, Q33]), "operationType" : NewBodyOperationType.REMOVE, "oppositeDirection" : true, "depth" : 25.4 * mm, "offsetDistance" : 25.4 * mm});
        }
        {
            var Q0;
            Q0=makeQuery(id+"F10.imprint","IMPRINT",FACE,{"disambiguationData":[TD([[makeQuery(id+"F10.imprint","IMPRINT",EDGE,{"derivedFrom":sQuery(id+"F10.wireOp",EDGE,"E404")}),1.0]])]});
            var Q1;
            Q1=makeQuery(id+"F10.imprint","IMPRINT",FACE,{"disambiguationData":[TD([[makeQuery(id+"F10.imprint","IMPRINT",EDGE,{"derivedFrom":sQuery(id+"F10.wireOp",EDGE,"E402")}),1.0]])]});
            var Q2;
            Q2=makeQuery(id+"F10.imprint","IMPRINT",FACE,{"disambiguationData":[TD([[makeQuery(id+"F10.imprint","IMPRINT",EDGE,{"derivedFrom":sQuery(id+"F10.wireOp",EDGE,"E398")}),1.0]])]});
            var Q3;
            Q3=makeQuery(id+"F10.imprint","IMPRINT",FACE,{"disambiguationData":[TD([[makeQuery(id+"F10.imprint","IMPRINT",EDGE,{"derivedFrom":sQuery(id+"F10.wireOp",EDGE,"E400")}),1.0]])]});
            var Q4;
            Q4=makeQuery(id+"F10.imprint","IMPRINT",FACE,{"disambiguationData":[TD([[makeQuery(id+"F10.imprint","IMPRINT",EDGE,{"derivedFrom":sQuery(id+"F10.wireOp",EDGE,"E387")}),1.0]])]});
            var Q5;
            Q5=makeQuery(id+"F10.imprint","IMPRINT",FACE,{"disambiguationData":[TD([[makeQuery(id+"F10.imprint","IMPRINT",EDGE,{"derivedFrom":sQuery(id+"F10.wireOp",EDGE,"E388")}),1.0]])]});
            var Q6;
            Q6=makeQuery(id+"F10.imprint","IMPRINT",FACE,{"disambiguationData":[TD([[makeQuery(id+"F10.imprint","IMPRINT",EDGE,{"derivedFrom":sQuery(id+"F10.wireOp",EDGE,"E390")}),1.0]])]});
            var Q7;
            Q7=makeQuery(id+"F10.imprint","IMPRINT",FACE,{"disambiguationData":[TD([[makeQuery(id+"F10.imprint","IMPRINT",EDGE,{"derivedFrom":sQuery(id+"F10.wireOp",EDGE,"E392")}),1.0]])]});
            var Q8;
            Q8=makeQuery(id+"F10.imprint","IMPRINT",FACE,{"disambiguationData":[TD([[makeQuery(id+"F10.imprint","IMPRINT",EDGE,{"derivedFrom":sQuery(id+"F10.wireOp",EDGE,"E394")}),1.0]])]});
            var Q9;
            Q9=makeQuery(id+"F10.imprint","IMPRINT",FACE,{"disambiguationData":[TD([[makeQuery(id+"F10.imprint","IMPRINT",EDGE,{"derivedFrom":sQuery(id+"F10.wireOp",EDGE,"E396")}),1.0]])]});
            var Q10;
            Q10=makeQuery(id+"F10.imprint","IMPRINT",FACE,{"disambiguationData":[TD([[makeQuery(id+"F10.imprint","IMPRINT",EDGE,{"derivedFrom":sQuery(id+"F10.wireOp",EDGE,"E414")}),1.0]])]});
            var Q11;
            Q11=makeQuery(id+"F10.imprint","IMPRINT",FACE,{"disambiguationData":[TD([[makeQuery(id+"F10.imprint","IMPRINT",EDGE,{"derivedFrom":sQuery(id+"F10.wireOp",EDGE,"E412")}),1.0]])]});
            var Q12;
            Q12=makeQuery(id+"F10.imprint","IMPRINT",FACE,{"disambiguationData":[TD([[makeQuery(id+"F10.imprint","IMPRINT",EDGE,{"derivedFrom":sQuery(id+"F10.wireOp",EDGE,"E416")}),1.0]])]});
            var Q13;
            Q13=makeQuery(id+"F10.imprint","IMPRINT",FACE,{"disambiguationData":[TD([[makeQuery(id+"F10.imprint","IMPRINT",EDGE,{"derivedFrom":sQuery(id+"F10.wireOp",EDGE,"E409")}),1.0]])]});
            var Q14;
            Q14=makeQuery(id+"F10.imprint","IMPRINT",FACE,{"disambiguationData":[TD([[makeQuery(id+"F10.imprint","IMPRINT",EDGE,{"derivedFrom":sQuery(id+"F10.wireOp",EDGE,"E408")}),1.0]])]});
            var Q15;
            Q15=makeQuery(id+"F10.imprint","IMPRINT",FACE,{"disambiguationData":[TD([[makeQuery(id+"F10.imprint","IMPRINT",EDGE,{"derivedFrom":sQuery(id+"F10.wireOp",EDGE,"E405")}),1.0]])]});
            var Q16;
            Q16=makeQuery(id+"F10.imprint","IMPRINT",FACE,{"disambiguationData":[TD([[makeQuery(id+"F10.imprint","IMPRINT",EDGE,{"derivedFrom":sQuery(id+"F10.wireOp",EDGE,"E418")}),1.0]])]});
            var Q17;
            Q17=makeQuery(id+"F10.imprint","IMPRINT",FACE,{"disambiguationData":[TD([[makeQuery(id+"F10.imprint","IMPRINT",EDGE,{"derivedFrom":sQuery(id+"F10.wireOp",EDGE,"E419")}),1.0]])]});
            var Q18;
            Q18=makeQuery(id+"F10.imprint","IMPRINT",FACE,{"disambiguationData":[TD([[makeQuery(id+"F10.imprint","IMPRINT",EDGE,{"derivedFrom":sQuery(id+"F10.wireOp",EDGE,"E422")}),1.0]])]});
            var Q19;
            Q19=makeQuery(id+"F10.imprint","IMPRINT",FACE,{"disambiguationData":[TD([[makeQuery(id+"F10.imprint","IMPRINT",EDGE,{"derivedFrom":sQuery(id+"F10.wireOp",EDGE,"E366")}),-1.0]])]});
            var Q20;
            Q20=makeQuery(id+"F10.imprint","IMPRINT",FACE,{"disambiguationData":[TD([[makeQuery(id+"F10.imprint","IMPRINT",EDGE,{"derivedFrom":sQuery(id+"F10.wireOp",EDGE,"E432")}),1.0]])]});
            var Q21;
            Q21=makeQuery(id+"F10.imprint","IMPRINT",FACE,{"disambiguationData":[TD([[makeQuery(id+"F10.imprint","IMPRINT",EDGE,{"derivedFrom":sQuery(id+"F10.wireOp",EDGE,"E430")}),1.0]])]});
            var Q22;
            Q22=makeQuery(id+"F10.imprint","IMPRINT",FACE,{"disambiguationData":[TD([[makeQuery(id+"F10.imprint","IMPRINT",EDGE,{"derivedFrom":sQuery(id+"F10.wireOp",EDGE,"E434")}),1.0]])]});
            var Q23;
            Q23=makeQuery(id+"F10.imprint","IMPRINT",FACE,{"disambiguationData":[TD([[makeQuery(id+"F10.imprint","IMPRINT",EDGE,{"derivedFrom":sQuery(id+"F10.wireOp",EDGE,"E376")}),1.0]])]});
            var Q24;
            Q24=makeQuery(id+"F10.imprint","IMPRINT",FACE,{"disambiguationData":[TD([[makeQuery(id+"F10.imprint","IMPRINT",EDGE,{"derivedFrom":sQuery(id+"F10.wireOp",EDGE,"E378")}),1.0]])]});
            var Q25;
            Q25=makeQuery(id+"F10.imprint","IMPRINT",FACE,{"disambiguationData":[TD([[makeQuery(id+"F10.imprint","IMPRINT",EDGE,{"derivedFrom":sQuery(id+"F10.wireOp",EDGE,"E380")}),1.0]])]});
            var Q26;
            Q26=makeQuery(id+"F10.imprint","IMPRINT",FACE,{"disambiguationData":[TD([[makeQuery(id+"F10.imprint","IMPRINT",EDGE,{"derivedFrom":sQuery(id+"F10.wireOp",EDGE,"E382")}),1.0]])]});
            var Q27;
            Q27=makeQuery(id+"F10.imprint","IMPRINT",FACE,{"disambiguationData":[TD([[makeQuery(id+"F10.imprint","IMPRINT",EDGE,{"derivedFrom":sQuery(id+"F10.wireOp",EDGE,"E426")}),1.0]])]});
            var Q28;
            Q28=makeQuery(id+"F10.imprint","IMPRINT",FACE,{"disambiguationData":[TD([[makeQuery(id+"F10.imprint","IMPRINT",EDGE,{"derivedFrom":sQuery(id+"F10.wireOp",EDGE,"E428")}),1.0]])]});
            var Q29;
            Q29=makeQuery(id+"F10.imprint","IMPRINT",FACE,{"disambiguationData":[TD([[makeQuery(id+"F10.imprint","IMPRINT",EDGE,{"derivedFrom":sQuery(id+"F10.wireOp",EDGE,"E367")}),1.0]])]});
            var Q30;
            Q30=makeQuery(id+"F10.imprint","IMPRINT",FACE,{"disambiguationData":[TD([[makeQuery(id+"F10.imprint","IMPRINT",EDGE,{"derivedFrom":sQuery(id+"F10.wireOp",EDGE,"E368")}),1.0]])]});
            var Q31;
            Q31=makeQuery(id+"F10.imprint","IMPRINT",FACE,{"disambiguationData":[TD([[makeQuery(id+"F10.imprint","IMPRINT",EDGE,{"derivedFrom":sQuery(id+"F10.wireOp",EDGE,"E424")}),1.0]])]});
            var Q32;
            Q32=makeQuery(id+"F10.imprint","IMPRINT",FACE,{"disambiguationData":[TD([[makeQuery(id+"F10.imprint","IMPRINT",EDGE,{"derivedFrom":sQuery(id+"F10.wireOp",EDGE,"E372")}),-1.0]])]});
            var Q33;
            Q33=makeQuery(id+"F10.imprint","IMPRINT",FACE,{"disambiguationData":[TD([[makeQuery(id+"F10.imprint","IMPRINT",EDGE,{"derivedFrom":sQuery(id+"F10.wireOp",EDGE,"E374")}),1.0]])]});
            extrude(context, id + "F12", {"entities" : qUnion([Q0, Q1, Q2, Q3, Q4, Q5, Q6, Q7, Q8, Q9, Q10, Q11, Q12, Q13, Q14, Q15, Q16, Q17, Q18, Q19, Q20, Q21, Q22, Q23, Q24, Q25, Q26, Q27, Q28, Q29, Q30, Q31, Q32, Q33]), "operationType" : NewBodyOperationType.REMOVE, "oppositeDirection" : true, "depth" : 1.59 * mm, "offsetDistance" : 25.4 * mm});
        }
        {
            var Q0;
            Q0=makeQuery(id+"F10.imprint","IMPRINT",FACE,{"disambiguationData":[TD([[makeQuery(id+"F10.imprint","IMPRINT",EDGE,{"derivedFrom":sQuery(id+"F10.wireOp",EDGE,"E367")}),-1.0]])]});
            var sketch = newSketch(context, id + "F13", { "sketchPlane" : qUnion([Q0])});
            skPoint(sketch, "E437.0", {"position": v(298.45, -371.48) * mm});
            skLineSegment(sketch, "E438.0", {"start": v(279.4, -184.94) * mm, "end": v(279.4, -812) * mm, "construction": true});
            skPoint(sketch, "E439.0", {"position": v(298.45, -625.48) * mm});
            skLineSegment(sketch, "E440.bottom", {"start": v(298.45, -371.48) * mm, "end": v(279.4, -371.48) * mm});
            skLineSegment(sketch, "E440.top", {"start": v(298.45, -625.48) * mm, "end": v(279.4, -625.48) * mm});
            skLineSegment(sketch, "E440.left", {"start": v(298.45, -371.48) * mm, "end": v(298.45, -625.48) * mm});
            skLineSegment(sketch, "E440.right", {"start": v(279.4, -371.48) * mm, "end": v(279.4, -625.48) * mm});
            skSolve(sketch);
        }
        {
            var Q0;
            Q0 = qSketchRegion(id + "F13", true);
            extrude(context, id + "F14", {"entities" : qUnion([Q0]), "operationType" : NewBodyOperationType.REMOVE, "oppositeDirection" : true, "depth" : 3.17 * mm, "offsetDistance" : 25.4 * mm});
        }
    });
